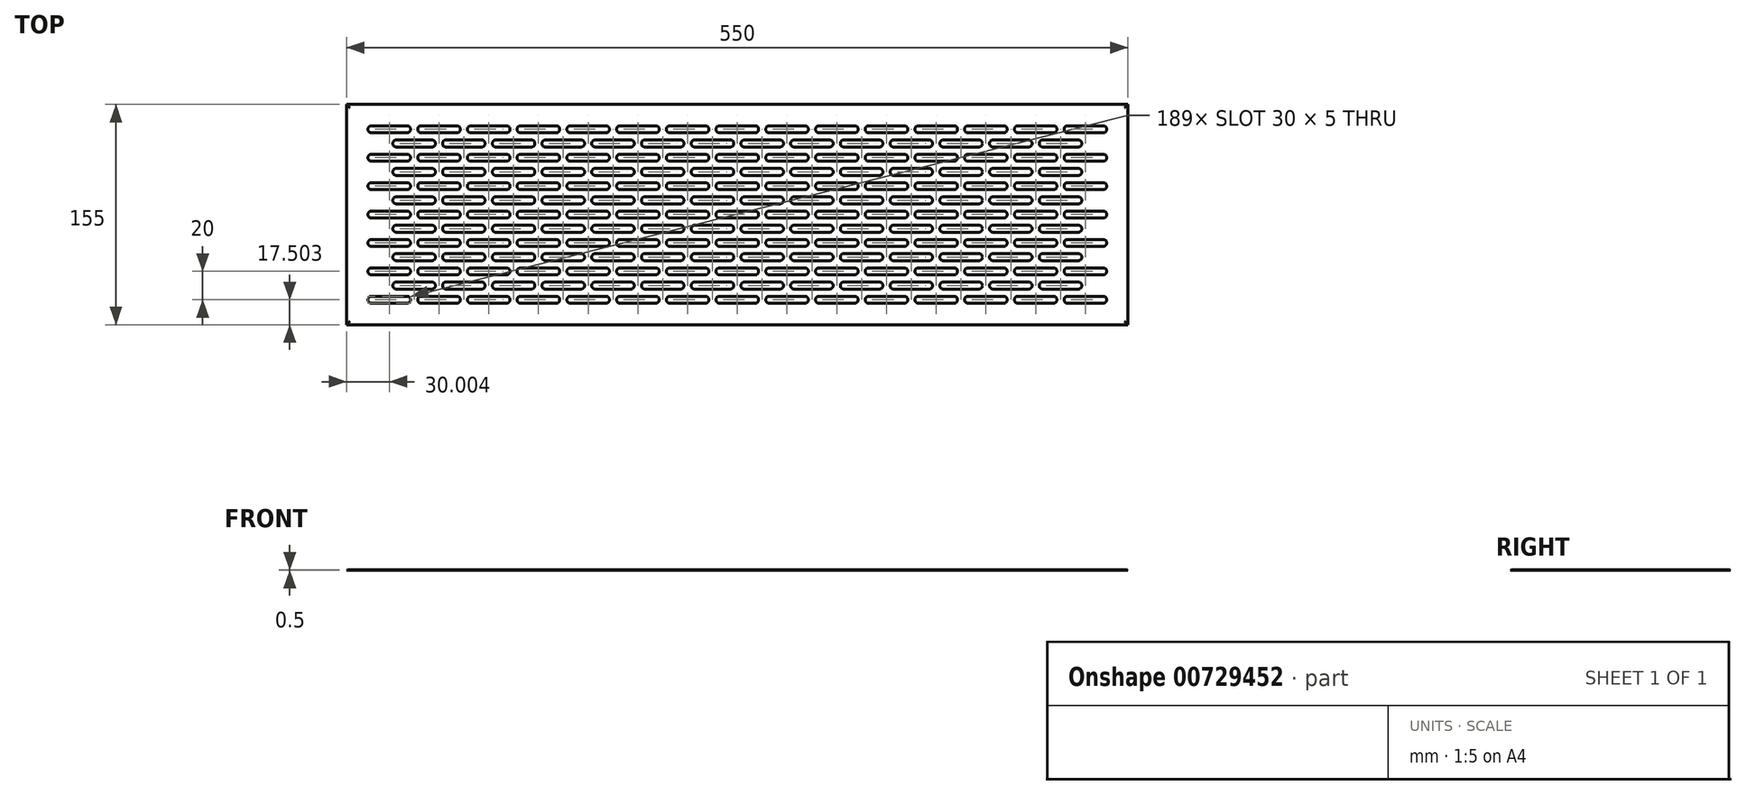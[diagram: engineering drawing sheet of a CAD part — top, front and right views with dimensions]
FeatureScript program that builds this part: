
annotation { "Feature Type Name" : "Feature", "Feature Type Description" : "" }
export const myFeature = defineFeature(function(context is Context, id is Id, definition is map)
    precondition{}
    {
        {
            var Q0;
            Q0=qCreatedBy(makeId("Top.planeOp"),FACE);
            var sketch = newSketch(context, id + "F0", { "sketchPlane" : qUnion([Q0])});
            skLineSegment(sketch, "E0.bottom", {"start": v(-229.5, 79.48) * mm, "end": v(320.5, 79.48) * mm});
            skLineSegment(sketch, "E0.top", {"start": v(-229.5, -75.52) * mm, "end": v(320.5, -75.52) * mm});
            skLineSegment(sketch, "E0.left", {"start": v(-229.5, 79.48) * mm, "end": v(-229.5, -75.52) * mm});
            skLineSegment(sketch, "E0.right", {"start": v(320.5, 79.48) * mm, "end": v(320.5, -75.52) * mm});
            skSolve(sketch);
        }
        {
            var Q0;
            Q0=makeQuery(id+"F0.imprint","IMPRINT",FACE,{"disambiguationData":[TD([[makeQuery(id+"F0.imprint","IMPRINT",EDGE,{"derivedFrom":sQuery(id+"F0.wireOp",EDGE,"E0.bottom")}),-1.0]])]});
            extrude(context, id + "F1", {"entities" : qUnion([Q0]), "depth" : 0.5 * mm, "offsetDistance" : 25 * mm});
        }
        {
            var Q0;
            Q0=makeQuery(id+"F1.opExtrude","CAP_FACE",FACE,{"disambiguationData":[OSD([sQuery(id+"F0.wireOp",EDGE,"E0.bottom"),sQuery(id+"F0.wireOp",EDGE,"E0.top"),sQuery(id+"F0.wireOp",EDGE,"E0.left"),sQuery(id+"F0.wireOp",EDGE,"E0.right")])],"isStart":false});
            var sketch = newSketch(context, id + "F2", { "sketchPlane" : qUnion([Q0])});
            skLineSegment(sketch, "E1.bottom", {"start": v(-212, -55.52) * mm, "end": v(-187, -55.52) * mm});
            skLineSegment(sketch, "E1.top", {"start": v(-212, -60.52) * mm, "end": v(-187, -60.52) * mm});
            skLineSegment(sketch, "E1.left", {"start": v(-214.5, -58.02) * mm, "end": v(-214.5, -58.02) * mm});
            skLineSegment(sketch, "E1.right", {"start": v(-184.5, -58.02) * mm, "end": v(-184.5, -58.02) * mm});
            skPoint(sketch, "E2.visualSharp", {"position": v(-214.5, -60.52) * mm});
            skArc(sketch, "E2.filletArc", {"start": v(-214.5, -58.02) * mm, "mid": v(-213.77, -59.78) * mm, "end": v(-212, -60.52) * mm});
            skPoint(sketch, "E3.visualSharp", {"position": v(-214.5, -55.52) * mm});
            skArc(sketch, "E3.filletArc", {"start": v(-212, -55.52) * mm, "mid": v(-213.77, -56.25) * mm, "end": v(-214.5, -58.02) * mm});
            skPoint(sketch, "E4.visualSharp", {"position": v(-184.5, -55.52) * mm});
            skArc(sketch, "E4.filletArc", {"start": v(-184.5, -58.02) * mm, "mid": v(-185.24, -56.25) * mm, "end": v(-187, -55.52) * mm});
            skPoint(sketch, "E5.visualSharp", {"position": v(-184.5, -60.52) * mm});
            skArc(sketch, "E5.filletArc", {"start": v(-187, -60.52) * mm, "mid": v(-185.24, -59.78) * mm, "end": v(-184.5, -58.02) * mm});
            skLineSegment(sketch, "E6.0.1.0", {"start": v(-212, -35.52) * mm, "end": v(-187, -35.52) * mm});
            skArc(sketch, "E6.0.1.1", {"start": v(-212, -35.52) * mm, "mid": v(-213.77, -36.25) * mm, "end": v(-214.5, -38.02) * mm});
            skArc(sketch, "E6.0.1.2", {"start": v(-214.5, -38.02) * mm, "mid": v(-213.77, -39.78) * mm, "end": v(-212, -40.52) * mm});
            skLineSegment(sketch, "E6.0.1.3", {"start": v(-212, -40.52) * mm, "end": v(-187, -40.52) * mm});
            skArc(sketch, "E6.0.1.4", {"start": v(-187, -40.52) * mm, "mid": v(-185.24, -39.78) * mm, "end": v(-184.5, -38.02) * mm});
            skArc(sketch, "E6.0.1.5", {"start": v(-184.5, -38.02) * mm, "mid": v(-185.24, -36.25) * mm, "end": v(-187, -35.52) * mm});
            skLineSegment(sketch, "E6.0.2.0", {"start": v(-212, -15.52) * mm, "end": v(-187, -15.52) * mm});
            skArc(sketch, "E6.0.2.1", {"start": v(-212, -15.52) * mm, "mid": v(-213.77, -16.25) * mm, "end": v(-214.5, -18.02) * mm});
            skArc(sketch, "E6.0.2.2", {"start": v(-214.5, -18.02) * mm, "mid": v(-213.77, -19.78) * mm, "end": v(-212, -20.52) * mm});
            skLineSegment(sketch, "E6.0.2.3", {"start": v(-212, -20.52) * mm, "end": v(-187, -20.52) * mm});
            skArc(sketch, "E6.0.2.4", {"start": v(-187, -20.52) * mm, "mid": v(-185.24, -19.78) * mm, "end": v(-184.5, -18.02) * mm});
            skArc(sketch, "E6.0.2.5", {"start": v(-184.5, -18.02) * mm, "mid": v(-185.24, -16.25) * mm, "end": v(-187, -15.52) * mm});
            skLineSegment(sketch, "E6.0.3.0", {"start": v(-212, 4.48) * mm, "end": v(-187, 4.48) * mm});
            skArc(sketch, "E6.0.3.1", {"start": v(-212, 4.48) * mm, "mid": v(-213.77, 3.75) * mm, "end": v(-214.5, 1.98) * mm});
            skArc(sketch, "E6.0.3.2", {"start": v(-214.5, 1.98) * mm, "mid": v(-213.77, 0.22) * mm, "end": v(-212, -0.52) * mm});
            skLineSegment(sketch, "E6.0.3.3", {"start": v(-212, -0.52) * mm, "end": v(-187, -0.52) * mm});
            skArc(sketch, "E6.0.3.4", {"start": v(-187, -0.52) * mm, "mid": v(-185.24, 0.22) * mm, "end": v(-184.5, 1.98) * mm});
            skArc(sketch, "E6.0.3.5", {"start": v(-184.5, 1.98) * mm, "mid": v(-185.24, 3.75) * mm, "end": v(-187, 4.48) * mm});
            skLineSegment(sketch, "E6.0.4.0", {"start": v(-212, 24.48) * mm, "end": v(-187, 24.48) * mm});
            skArc(sketch, "E6.0.4.1", {"start": v(-212, 24.48) * mm, "mid": v(-213.77, 23.75) * mm, "end": v(-214.5, 21.98) * mm});
            skArc(sketch, "E6.0.4.2", {"start": v(-214.5, 21.98) * mm, "mid": v(-213.77, 20.22) * mm, "end": v(-212, 19.48) * mm});
            skLineSegment(sketch, "E6.0.4.3", {"start": v(-212, 19.48) * mm, "end": v(-187, 19.48) * mm});
            skArc(sketch, "E6.0.4.4", {"start": v(-187, 19.48) * mm, "mid": v(-185.24, 20.22) * mm, "end": v(-184.5, 21.98) * mm});
            skArc(sketch, "E6.0.4.5", {"start": v(-184.5, 21.98) * mm, "mid": v(-185.24, 23.75) * mm, "end": v(-187, 24.48) * mm});
            skLineSegment(sketch, "E6.0.5.0", {"start": v(-212, 44.48) * mm, "end": v(-187, 44.48) * mm});
            skArc(sketch, "E6.0.5.1", {"start": v(-212, 44.48) * mm, "mid": v(-213.77, 43.75) * mm, "end": v(-214.5, 41.98) * mm});
            skArc(sketch, "E6.0.5.2", {"start": v(-214.5, 41.98) * mm, "mid": v(-213.77, 40.22) * mm, "end": v(-212, 39.48) * mm});
            skLineSegment(sketch, "E6.0.5.3", {"start": v(-212, 39.48) * mm, "end": v(-187, 39.48) * mm});
            skArc(sketch, "E6.0.5.4", {"start": v(-187, 39.48) * mm, "mid": v(-185.24, 40.22) * mm, "end": v(-184.5, 41.98) * mm});
            skArc(sketch, "E6.0.5.5", {"start": v(-184.5, 41.98) * mm, "mid": v(-185.24, 43.75) * mm, "end": v(-187, 44.48) * mm});
            skLineSegment(sketch, "E6.0.6.0", {"start": v(-212, 64.48) * mm, "end": v(-187, 64.48) * mm});
            skArc(sketch, "E6.0.6.1", {"start": v(-212, 64.48) * mm, "mid": v(-213.77, 63.75) * mm, "end": v(-214.5, 61.98) * mm});
            skArc(sketch, "E6.0.6.2", {"start": v(-214.5, 61.98) * mm, "mid": v(-213.77, 60.22) * mm, "end": v(-212, 59.48) * mm});
            skLineSegment(sketch, "E6.0.6.3", {"start": v(-212, 59.48) * mm, "end": v(-187, 59.48) * mm});
            skArc(sketch, "E6.0.6.4", {"start": v(-187, 59.48) * mm, "mid": v(-185.24, 60.22) * mm, "end": v(-184.5, 61.98) * mm});
            skArc(sketch, "E6.0.6.5", {"start": v(-184.5, 61.98) * mm, "mid": v(-185.24, 63.75) * mm, "end": v(-187, 64.48) * mm});
            skLineSegment(sketch, "E6.1.0.0", {"start": v(-177, -55.52) * mm, "end": v(-152, -55.52) * mm});
            skArc(sketch, "E6.1.0.1", {"start": v(-177, -55.52) * mm, "mid": v(-178.77, -56.25) * mm, "end": v(-179.5, -58.02) * mm});
            skArc(sketch, "E6.1.0.2", {"start": v(-179.5, -58.02) * mm, "mid": v(-178.77, -59.78) * mm, "end": v(-177, -60.52) * mm});
            skLineSegment(sketch, "E6.1.0.3", {"start": v(-177, -60.52) * mm, "end": v(-152, -60.52) * mm});
            skArc(sketch, "E6.1.0.4", {"start": v(-152, -60.52) * mm, "mid": v(-150.24, -59.78) * mm, "end": v(-149.5, -58.02) * mm});
            skArc(sketch, "E6.1.0.5", {"start": v(-149.5, -58.02) * mm, "mid": v(-150.24, -56.25) * mm, "end": v(-152, -55.52) * mm});
            skLineSegment(sketch, "E6.1.1.0", {"start": v(-177, -35.52) * mm, "end": v(-152, -35.52) * mm});
            skArc(sketch, "E6.1.1.1", {"start": v(-177, -35.52) * mm, "mid": v(-178.77, -36.25) * mm, "end": v(-179.5, -38.02) * mm});
            skArc(sketch, "E6.1.1.2", {"start": v(-179.5, -38.02) * mm, "mid": v(-178.77, -39.78) * mm, "end": v(-177, -40.52) * mm});
            skLineSegment(sketch, "E6.1.1.3", {"start": v(-177, -40.52) * mm, "end": v(-152, -40.52) * mm});
            skArc(sketch, "E6.1.1.4", {"start": v(-152, -40.52) * mm, "mid": v(-150.24, -39.78) * mm, "end": v(-149.5, -38.02) * mm});
            skArc(sketch, "E6.1.1.5", {"start": v(-149.5, -38.02) * mm, "mid": v(-150.24, -36.25) * mm, "end": v(-152, -35.52) * mm});
            skLineSegment(sketch, "E6.1.2.0", {"start": v(-177, -15.52) * mm, "end": v(-152, -15.52) * mm});
            skArc(sketch, "E6.1.2.1", {"start": v(-177, -15.52) * mm, "mid": v(-178.77, -16.25) * mm, "end": v(-179.5, -18.02) * mm});
            skArc(sketch, "E6.1.2.2", {"start": v(-179.5, -18.02) * mm, "mid": v(-178.77, -19.78) * mm, "end": v(-177, -20.52) * mm});
            skLineSegment(sketch, "E6.1.2.3", {"start": v(-177, -20.52) * mm, "end": v(-152, -20.52) * mm});
            skArc(sketch, "E6.1.2.4", {"start": v(-152, -20.52) * mm, "mid": v(-150.24, -19.78) * mm, "end": v(-149.5, -18.02) * mm});
            skArc(sketch, "E6.1.2.5", {"start": v(-149.5, -18.02) * mm, "mid": v(-150.24, -16.25) * mm, "end": v(-152, -15.52) * mm});
            skLineSegment(sketch, "E6.1.3.0", {"start": v(-177, 4.48) * mm, "end": v(-152, 4.48) * mm});
            skArc(sketch, "E6.1.3.1", {"start": v(-177, 4.48) * mm, "mid": v(-178.77, 3.75) * mm, "end": v(-179.5, 1.98) * mm});
            skArc(sketch, "E6.1.3.2", {"start": v(-179.5, 1.98) * mm, "mid": v(-178.77, 0.22) * mm, "end": v(-177, -0.52) * mm});
            skLineSegment(sketch, "E6.1.3.3", {"start": v(-177, -0.52) * mm, "end": v(-152, -0.52) * mm});
            skArc(sketch, "E6.1.3.4", {"start": v(-152, -0.52) * mm, "mid": v(-150.24, 0.22) * mm, "end": v(-149.5, 1.98) * mm});
            skArc(sketch, "E6.1.3.5", {"start": v(-149.5, 1.98) * mm, "mid": v(-150.24, 3.75) * mm, "end": v(-152, 4.48) * mm});
            skLineSegment(sketch, "E6.1.4.0", {"start": v(-177, 24.48) * mm, "end": v(-152, 24.48) * mm});
            skArc(sketch, "E6.1.4.1", {"start": v(-177, 24.48) * mm, "mid": v(-178.77, 23.75) * mm, "end": v(-179.5, 21.98) * mm});
            skArc(sketch, "E6.1.4.2", {"start": v(-179.5, 21.98) * mm, "mid": v(-178.77, 20.22) * mm, "end": v(-177, 19.48) * mm});
            skLineSegment(sketch, "E6.1.4.3", {"start": v(-177, 19.48) * mm, "end": v(-152, 19.48) * mm});
            skArc(sketch, "E6.1.4.4", {"start": v(-152, 19.48) * mm, "mid": v(-150.24, 20.22) * mm, "end": v(-149.5, 21.98) * mm});
            skArc(sketch, "E6.1.4.5", {"start": v(-149.5, 21.98) * mm, "mid": v(-150.24, 23.75) * mm, "end": v(-152, 24.48) * mm});
            skLineSegment(sketch, "E6.1.5.0", {"start": v(-177, 44.48) * mm, "end": v(-152, 44.48) * mm});
            skArc(sketch, "E6.1.5.1", {"start": v(-177, 44.48) * mm, "mid": v(-178.77, 43.75) * mm, "end": v(-179.5, 41.98) * mm});
            skArc(sketch, "E6.1.5.2", {"start": v(-179.5, 41.98) * mm, "mid": v(-178.77, 40.22) * mm, "end": v(-177, 39.48) * mm});
            skLineSegment(sketch, "E6.1.5.3", {"start": v(-177, 39.48) * mm, "end": v(-152, 39.48) * mm});
            skArc(sketch, "E6.1.5.4", {"start": v(-152, 39.48) * mm, "mid": v(-150.24, 40.22) * mm, "end": v(-149.5, 41.98) * mm});
            skArc(sketch, "E6.1.5.5", {"start": v(-149.5, 41.98) * mm, "mid": v(-150.24, 43.75) * mm, "end": v(-152, 44.48) * mm});
            skLineSegment(sketch, "E6.1.6.0", {"start": v(-177, 64.48) * mm, "end": v(-152, 64.48) * mm});
            skArc(sketch, "E6.1.6.1", {"start": v(-177, 64.48) * mm, "mid": v(-178.77, 63.75) * mm, "end": v(-179.5, 61.98) * mm});
            skArc(sketch, "E6.1.6.2", {"start": v(-179.5, 61.98) * mm, "mid": v(-178.77, 60.22) * mm, "end": v(-177, 59.48) * mm});
            skLineSegment(sketch, "E6.1.6.3", {"start": v(-177, 59.48) * mm, "end": v(-152, 59.48) * mm});
            skArc(sketch, "E6.1.6.4", {"start": v(-152, 59.48) * mm, "mid": v(-150.24, 60.22) * mm, "end": v(-149.5, 61.98) * mm});
            skArc(sketch, "E6.1.6.5", {"start": v(-149.5, 61.98) * mm, "mid": v(-150.24, 63.75) * mm, "end": v(-152, 64.48) * mm});
            skLineSegment(sketch, "E6.2.0.0", {"start": v(-142, -55.52) * mm, "end": v(-117, -55.52) * mm});
            skArc(sketch, "E6.2.0.1", {"start": v(-142, -55.52) * mm, "mid": v(-143.77, -56.25) * mm, "end": v(-144.5, -58.02) * mm});
            skArc(sketch, "E6.2.0.2", {"start": v(-144.5, -58.02) * mm, "mid": v(-143.77, -59.78) * mm, "end": v(-142, -60.52) * mm});
            skLineSegment(sketch, "E6.2.0.3", {"start": v(-142, -60.52) * mm, "end": v(-117, -60.52) * mm});
            skArc(sketch, "E6.2.0.4", {"start": v(-117, -60.52) * mm, "mid": v(-115.24, -59.78) * mm, "end": v(-114.5, -58.02) * mm});
            skArc(sketch, "E6.2.0.5", {"start": v(-114.5, -58.02) * mm, "mid": v(-115.24, -56.25) * mm, "end": v(-117, -55.52) * mm});
            skLineSegment(sketch, "E6.2.1.0", {"start": v(-142, -35.52) * mm, "end": v(-117, -35.52) * mm});
            skArc(sketch, "E6.2.1.1", {"start": v(-142, -35.52) * mm, "mid": v(-143.77, -36.25) * mm, "end": v(-144.5, -38.02) * mm});
            skArc(sketch, "E6.2.1.2", {"start": v(-144.5, -38.02) * mm, "mid": v(-143.77, -39.78) * mm, "end": v(-142, -40.52) * mm});
            skLineSegment(sketch, "E6.2.1.3", {"start": v(-142, -40.52) * mm, "end": v(-117, -40.52) * mm});
            skArc(sketch, "E6.2.1.4", {"start": v(-117, -40.52) * mm, "mid": v(-115.24, -39.78) * mm, "end": v(-114.5, -38.02) * mm});
            skArc(sketch, "E6.2.1.5", {"start": v(-114.5, -38.02) * mm, "mid": v(-115.24, -36.25) * mm, "end": v(-117, -35.52) * mm});
            skLineSegment(sketch, "E6.2.2.0", {"start": v(-142, -15.52) * mm, "end": v(-117, -15.52) * mm});
            skArc(sketch, "E6.2.2.1", {"start": v(-142, -15.52) * mm, "mid": v(-143.77, -16.25) * mm, "end": v(-144.5, -18.02) * mm});
            skArc(sketch, "E6.2.2.2", {"start": v(-144.5, -18.02) * mm, "mid": v(-143.77, -19.78) * mm, "end": v(-142, -20.52) * mm});
            skLineSegment(sketch, "E6.2.2.3", {"start": v(-142, -20.52) * mm, "end": v(-117, -20.52) * mm});
            skArc(sketch, "E6.2.2.4", {"start": v(-117, -20.52) * mm, "mid": v(-115.24, -19.78) * mm, "end": v(-114.5, -18.02) * mm});
            skArc(sketch, "E6.2.2.5", {"start": v(-114.5, -18.02) * mm, "mid": v(-115.24, -16.25) * mm, "end": v(-117, -15.52) * mm});
            skLineSegment(sketch, "E6.2.3.0", {"start": v(-142, 4.48) * mm, "end": v(-117, 4.48) * mm});
            skArc(sketch, "E6.2.3.1", {"start": v(-142, 4.48) * mm, "mid": v(-143.77, 3.75) * mm, "end": v(-144.5, 1.98) * mm});
            skArc(sketch, "E6.2.3.2", {"start": v(-144.5, 1.98) * mm, "mid": v(-143.77, 0.22) * mm, "end": v(-142, -0.52) * mm});
            skLineSegment(sketch, "E6.2.3.3", {"start": v(-142, -0.52) * mm, "end": v(-117, -0.52) * mm});
            skArc(sketch, "E6.2.3.4", {"start": v(-117, -0.52) * mm, "mid": v(-115.24, 0.22) * mm, "end": v(-114.5, 1.98) * mm});
            skArc(sketch, "E6.2.3.5", {"start": v(-114.5, 1.98) * mm, "mid": v(-115.24, 3.75) * mm, "end": v(-117, 4.48) * mm});
            skLineSegment(sketch, "E6.2.4.0", {"start": v(-142, 24.48) * mm, "end": v(-117, 24.48) * mm});
            skArc(sketch, "E6.2.4.1", {"start": v(-142, 24.48) * mm, "mid": v(-143.77, 23.75) * mm, "end": v(-144.5, 21.98) * mm});
            skArc(sketch, "E6.2.4.2", {"start": v(-144.5, 21.98) * mm, "mid": v(-143.77, 20.22) * mm, "end": v(-142, 19.48) * mm});
            skLineSegment(sketch, "E6.2.4.3", {"start": v(-142, 19.48) * mm, "end": v(-117, 19.48) * mm});
            skArc(sketch, "E6.2.4.4", {"start": v(-117, 19.48) * mm, "mid": v(-115.24, 20.22) * mm, "end": v(-114.5, 21.98) * mm});
            skArc(sketch, "E6.2.4.5", {"start": v(-114.5, 21.98) * mm, "mid": v(-115.24, 23.75) * mm, "end": v(-117, 24.48) * mm});
            skLineSegment(sketch, "E6.2.5.0", {"start": v(-142, 44.48) * mm, "end": v(-117, 44.48) * mm});
            skArc(sketch, "E6.2.5.1", {"start": v(-142, 44.48) * mm, "mid": v(-143.77, 43.75) * mm, "end": v(-144.5, 41.98) * mm});
            skArc(sketch, "E6.2.5.2", {"start": v(-144.5, 41.98) * mm, "mid": v(-143.77, 40.22) * mm, "end": v(-142, 39.48) * mm});
            skLineSegment(sketch, "E6.2.5.3", {"start": v(-142, 39.48) * mm, "end": v(-117, 39.48) * mm});
            skArc(sketch, "E6.2.5.4", {"start": v(-117, 39.48) * mm, "mid": v(-115.24, 40.22) * mm, "end": v(-114.5, 41.98) * mm});
            skArc(sketch, "E6.2.5.5", {"start": v(-114.5, 41.98) * mm, "mid": v(-115.24, 43.75) * mm, "end": v(-117, 44.48) * mm});
            skLineSegment(sketch, "E6.2.6.0", {"start": v(-142, 64.48) * mm, "end": v(-117, 64.48) * mm});
            skArc(sketch, "E6.2.6.1", {"start": v(-142, 64.48) * mm, "mid": v(-143.77, 63.75) * mm, "end": v(-144.5, 61.98) * mm});
            skArc(sketch, "E6.2.6.2", {"start": v(-144.5, 61.98) * mm, "mid": v(-143.77, 60.22) * mm, "end": v(-142, 59.48) * mm});
            skLineSegment(sketch, "E6.2.6.3", {"start": v(-142, 59.48) * mm, "end": v(-117, 59.48) * mm});
            skArc(sketch, "E6.2.6.4", {"start": v(-117, 59.48) * mm, "mid": v(-115.24, 60.22) * mm, "end": v(-114.5, 61.98) * mm});
            skArc(sketch, "E6.2.6.5", {"start": v(-114.5, 61.98) * mm, "mid": v(-115.24, 63.75) * mm, "end": v(-117, 64.48) * mm});
            skLineSegment(sketch, "E6.3.0.0", {"start": v(-107, -55.52) * mm, "end": v(-82, -55.52) * mm});
            skArc(sketch, "E6.3.0.1", {"start": v(-107, -55.52) * mm, "mid": v(-108.77, -56.25) * mm, "end": v(-109.5, -58.02) * mm});
            skArc(sketch, "E6.3.0.2", {"start": v(-109.5, -58.02) * mm, "mid": v(-108.77, -59.78) * mm, "end": v(-107, -60.52) * mm});
            skLineSegment(sketch, "E6.3.0.3", {"start": v(-107, -60.52) * mm, "end": v(-82, -60.52) * mm});
            skArc(sketch, "E6.3.0.4", {"start": v(-82, -60.52) * mm, "mid": v(-80.24, -59.78) * mm, "end": v(-79.5, -58.02) * mm});
            skArc(sketch, "E6.3.0.5", {"start": v(-79.5, -58.02) * mm, "mid": v(-80.24, -56.25) * mm, "end": v(-82, -55.52) * mm});
            skLineSegment(sketch, "E6.3.1.0", {"start": v(-107, -35.52) * mm, "end": v(-82, -35.52) * mm});
            skArc(sketch, "E6.3.1.1", {"start": v(-107, -35.52) * mm, "mid": v(-108.77, -36.25) * mm, "end": v(-109.5, -38.02) * mm});
            skArc(sketch, "E6.3.1.2", {"start": v(-109.5, -38.02) * mm, "mid": v(-108.77, -39.78) * mm, "end": v(-107, -40.52) * mm});
            skLineSegment(sketch, "E6.3.1.3", {"start": v(-107, -40.52) * mm, "end": v(-82, -40.52) * mm});
            skArc(sketch, "E6.3.1.4", {"start": v(-82, -40.52) * mm, "mid": v(-80.24, -39.78) * mm, "end": v(-79.5, -38.02) * mm});
            skArc(sketch, "E6.3.1.5", {"start": v(-79.5, -38.02) * mm, "mid": v(-80.24, -36.25) * mm, "end": v(-82, -35.52) * mm});
            skLineSegment(sketch, "E6.3.2.0", {"start": v(-107, -15.52) * mm, "end": v(-82, -15.52) * mm});
            skArc(sketch, "E6.3.2.1", {"start": v(-107, -15.52) * mm, "mid": v(-108.77, -16.25) * mm, "end": v(-109.5, -18.02) * mm});
            skArc(sketch, "E6.3.2.2", {"start": v(-109.5, -18.02) * mm, "mid": v(-108.77, -19.78) * mm, "end": v(-107, -20.52) * mm});
            skLineSegment(sketch, "E6.3.2.3", {"start": v(-107, -20.52) * mm, "end": v(-82, -20.52) * mm});
            skArc(sketch, "E6.3.2.4", {"start": v(-82, -20.52) * mm, "mid": v(-80.24, -19.78) * mm, "end": v(-79.5, -18.02) * mm});
            skArc(sketch, "E6.3.2.5", {"start": v(-79.5, -18.02) * mm, "mid": v(-80.24, -16.25) * mm, "end": v(-82, -15.52) * mm});
            skLineSegment(sketch, "E6.3.3.0", {"start": v(-107, 4.48) * mm, "end": v(-82, 4.48) * mm});
            skArc(sketch, "E6.3.3.1", {"start": v(-107, 4.48) * mm, "mid": v(-108.77, 3.75) * mm, "end": v(-109.5, 1.98) * mm});
            skArc(sketch, "E6.3.3.2", {"start": v(-109.5, 1.98) * mm, "mid": v(-108.77, 0.22) * mm, "end": v(-107, -0.52) * mm});
            skLineSegment(sketch, "E6.3.3.3", {"start": v(-107, -0.52) * mm, "end": v(-82, -0.52) * mm});
            skArc(sketch, "E6.3.3.4", {"start": v(-82, -0.52) * mm, "mid": v(-80.24, 0.22) * mm, "end": v(-79.5, 1.98) * mm});
            skArc(sketch, "E6.3.3.5", {"start": v(-79.5, 1.98) * mm, "mid": v(-80.24, 3.75) * mm, "end": v(-82, 4.48) * mm});
            skLineSegment(sketch, "E6.3.4.0", {"start": v(-107, 24.48) * mm, "end": v(-82, 24.48) * mm});
            skArc(sketch, "E6.3.4.1", {"start": v(-107, 24.48) * mm, "mid": v(-108.77, 23.75) * mm, "end": v(-109.5, 21.98) * mm});
            skArc(sketch, "E6.3.4.2", {"start": v(-109.5, 21.98) * mm, "mid": v(-108.77, 20.22) * mm, "end": v(-107, 19.48) * mm});
            skLineSegment(sketch, "E6.3.4.3", {"start": v(-107, 19.48) * mm, "end": v(-82, 19.48) * mm});
            skArc(sketch, "E6.3.4.4", {"start": v(-82, 19.48) * mm, "mid": v(-80.24, 20.22) * mm, "end": v(-79.5, 21.98) * mm});
            skArc(sketch, "E6.3.4.5", {"start": v(-79.5, 21.98) * mm, "mid": v(-80.24, 23.75) * mm, "end": v(-82, 24.48) * mm});
            skLineSegment(sketch, "E6.3.5.0", {"start": v(-107, 44.48) * mm, "end": v(-82, 44.48) * mm});
            skArc(sketch, "E6.3.5.1", {"start": v(-107, 44.48) * mm, "mid": v(-108.77, 43.75) * mm, "end": v(-109.5, 41.98) * mm});
            skArc(sketch, "E6.3.5.2", {"start": v(-109.5, 41.98) * mm, "mid": v(-108.77, 40.22) * mm, "end": v(-107, 39.48) * mm});
            skLineSegment(sketch, "E6.3.5.3", {"start": v(-107, 39.48) * mm, "end": v(-82, 39.48) * mm});
            skArc(sketch, "E6.3.5.4", {"start": v(-82, 39.48) * mm, "mid": v(-80.24, 40.22) * mm, "end": v(-79.5, 41.98) * mm});
            skArc(sketch, "E6.3.5.5", {"start": v(-79.5, 41.98) * mm, "mid": v(-80.24, 43.75) * mm, "end": v(-82, 44.48) * mm});
            skLineSegment(sketch, "E6.3.6.0", {"start": v(-107, 64.48) * mm, "end": v(-82, 64.48) * mm});
            skArc(sketch, "E6.3.6.1", {"start": v(-107, 64.48) * mm, "mid": v(-108.77, 63.75) * mm, "end": v(-109.5, 61.98) * mm});
            skArc(sketch, "E6.3.6.2", {"start": v(-109.5, 61.98) * mm, "mid": v(-108.77, 60.22) * mm, "end": v(-107, 59.48) * mm});
            skLineSegment(sketch, "E6.3.6.3", {"start": v(-107, 59.48) * mm, "end": v(-82, 59.48) * mm});
            skArc(sketch, "E6.3.6.4", {"start": v(-82, 59.48) * mm, "mid": v(-80.24, 60.22) * mm, "end": v(-79.5, 61.98) * mm});
            skArc(sketch, "E6.3.6.5", {"start": v(-79.5, 61.98) * mm, "mid": v(-80.24, 63.75) * mm, "end": v(-82, 64.48) * mm});
            skLineSegment(sketch, "E6.4.0.0", {"start": v(-72, -55.52) * mm, "end": v(-47, -55.52) * mm});
            skArc(sketch, "E6.4.0.1", {"start": v(-72, -55.52) * mm, "mid": v(-73.77, -56.25) * mm, "end": v(-74.5, -58.02) * mm});
            skArc(sketch, "E6.4.0.2", {"start": v(-74.5, -58.02) * mm, "mid": v(-73.77, -59.78) * mm, "end": v(-72, -60.52) * mm});
            skLineSegment(sketch, "E6.4.0.3", {"start": v(-72, -60.52) * mm, "end": v(-47, -60.52) * mm});
            skArc(sketch, "E6.4.0.4", {"start": v(-47, -60.52) * mm, "mid": v(-45.24, -59.78) * mm, "end": v(-44.5, -58.02) * mm});
            skArc(sketch, "E6.4.0.5", {"start": v(-44.5, -58.02) * mm, "mid": v(-45.24, -56.25) * mm, "end": v(-47, -55.52) * mm});
            skLineSegment(sketch, "E6.4.1.0", {"start": v(-72, -35.52) * mm, "end": v(-47, -35.52) * mm});
            skArc(sketch, "E6.4.1.1", {"start": v(-72, -35.52) * mm, "mid": v(-73.77, -36.25) * mm, "end": v(-74.5, -38.02) * mm});
            skArc(sketch, "E6.4.1.2", {"start": v(-74.5, -38.02) * mm, "mid": v(-73.77, -39.78) * mm, "end": v(-72, -40.52) * mm});
            skLineSegment(sketch, "E6.4.1.3", {"start": v(-72, -40.52) * mm, "end": v(-47, -40.52) * mm});
            skArc(sketch, "E6.4.1.4", {"start": v(-47, -40.52) * mm, "mid": v(-45.24, -39.78) * mm, "end": v(-44.5, -38.02) * mm});
            skArc(sketch, "E6.4.1.5", {"start": v(-44.5, -38.02) * mm, "mid": v(-45.24, -36.25) * mm, "end": v(-47, -35.52) * mm});
            skLineSegment(sketch, "E6.4.2.0", {"start": v(-72, -15.52) * mm, "end": v(-47, -15.52) * mm});
            skArc(sketch, "E6.4.2.1", {"start": v(-72, -15.52) * mm, "mid": v(-73.77, -16.25) * mm, "end": v(-74.5, -18.02) * mm});
            skArc(sketch, "E6.4.2.2", {"start": v(-74.5, -18.02) * mm, "mid": v(-73.77, -19.78) * mm, "end": v(-72, -20.52) * mm});
            skLineSegment(sketch, "E6.4.2.3", {"start": v(-72, -20.52) * mm, "end": v(-47, -20.52) * mm});
            skArc(sketch, "E6.4.2.4", {"start": v(-47, -20.52) * mm, "mid": v(-45.24, -19.78) * mm, "end": v(-44.5, -18.02) * mm});
            skArc(sketch, "E6.4.2.5", {"start": v(-44.5, -18.02) * mm, "mid": v(-45.24, -16.25) * mm, "end": v(-47, -15.52) * mm});
            skLineSegment(sketch, "E6.4.3.0", {"start": v(-72, 4.48) * mm, "end": v(-47, 4.48) * mm});
            skArc(sketch, "E6.4.3.1", {"start": v(-72, 4.48) * mm, "mid": v(-73.77, 3.75) * mm, "end": v(-74.5, 1.98) * mm});
            skArc(sketch, "E6.4.3.2", {"start": v(-74.5, 1.98) * mm, "mid": v(-73.77, 0.22) * mm, "end": v(-72, -0.52) * mm});
            skLineSegment(sketch, "E6.4.3.3", {"start": v(-72, -0.52) * mm, "end": v(-47, -0.52) * mm});
            skArc(sketch, "E6.4.3.4", {"start": v(-47, -0.52) * mm, "mid": v(-45.24, 0.22) * mm, "end": v(-44.5, 1.98) * mm});
            skArc(sketch, "E6.4.3.5", {"start": v(-44.5, 1.98) * mm, "mid": v(-45.24, 3.75) * mm, "end": v(-47, 4.48) * mm});
            skLineSegment(sketch, "E6.4.4.0", {"start": v(-72, 24.48) * mm, "end": v(-47, 24.48) * mm});
            skArc(sketch, "E6.4.4.1", {"start": v(-72, 24.48) * mm, "mid": v(-73.77, 23.75) * mm, "end": v(-74.5, 21.98) * mm});
            skArc(sketch, "E6.4.4.2", {"start": v(-74.5, 21.98) * mm, "mid": v(-73.77, 20.22) * mm, "end": v(-72, 19.48) * mm});
            skLineSegment(sketch, "E6.4.4.3", {"start": v(-72, 19.48) * mm, "end": v(-47, 19.48) * mm});
            skArc(sketch, "E6.4.4.4", {"start": v(-47, 19.48) * mm, "mid": v(-45.24, 20.22) * mm, "end": v(-44.5, 21.98) * mm});
            skArc(sketch, "E6.4.4.5", {"start": v(-44.5, 21.98) * mm, "mid": v(-45.24, 23.75) * mm, "end": v(-47, 24.48) * mm});
            skLineSegment(sketch, "E6.4.5.0", {"start": v(-72, 44.48) * mm, "end": v(-47, 44.48) * mm});
            skArc(sketch, "E6.4.5.1", {"start": v(-72, 44.48) * mm, "mid": v(-73.77, 43.75) * mm, "end": v(-74.5, 41.98) * mm});
            skArc(sketch, "E6.4.5.2", {"start": v(-74.5, 41.98) * mm, "mid": v(-73.77, 40.22) * mm, "end": v(-72, 39.48) * mm});
            skLineSegment(sketch, "E6.4.5.3", {"start": v(-72, 39.48) * mm, "end": v(-47, 39.48) * mm});
            skArc(sketch, "E6.4.5.4", {"start": v(-47, 39.48) * mm, "mid": v(-45.24, 40.22) * mm, "end": v(-44.5, 41.98) * mm});
            skArc(sketch, "E6.4.5.5", {"start": v(-44.5, 41.98) * mm, "mid": v(-45.24, 43.75) * mm, "end": v(-47, 44.48) * mm});
            skLineSegment(sketch, "E6.4.6.0", {"start": v(-72, 64.48) * mm, "end": v(-47, 64.48) * mm});
            skArc(sketch, "E6.4.6.1", {"start": v(-72, 64.48) * mm, "mid": v(-73.77, 63.75) * mm, "end": v(-74.5, 61.98) * mm});
            skArc(sketch, "E6.4.6.2", {"start": v(-74.5, 61.98) * mm, "mid": v(-73.77, 60.22) * mm, "end": v(-72, 59.48) * mm});
            skLineSegment(sketch, "E6.4.6.3", {"start": v(-72, 59.48) * mm, "end": v(-47, 59.48) * mm});
            skArc(sketch, "E6.4.6.4", {"start": v(-47, 59.48) * mm, "mid": v(-45.24, 60.22) * mm, "end": v(-44.5, 61.98) * mm});
            skArc(sketch, "E6.4.6.5", {"start": v(-44.5, 61.98) * mm, "mid": v(-45.24, 63.75) * mm, "end": v(-47, 64.48) * mm});
            skLineSegment(sketch, "E6.5.0.0", {"start": v(-37, -55.52) * mm, "end": v(-12, -55.52) * mm});
            skArc(sketch, "E6.5.0.1", {"start": v(-37, -55.52) * mm, "mid": v(-38.77, -56.25) * mm, "end": v(-39.5, -58.02) * mm});
            skArc(sketch, "E6.5.0.2", {"start": v(-39.5, -58.02) * mm, "mid": v(-38.77, -59.78) * mm, "end": v(-37, -60.52) * mm});
            skLineSegment(sketch, "E6.5.0.3", {"start": v(-37, -60.52) * mm, "end": v(-12, -60.52) * mm});
            skArc(sketch, "E6.5.0.4", {"start": v(-12, -60.52) * mm, "mid": v(-10.24, -59.78) * mm, "end": v(-9.5, -58.02) * mm});
            skArc(sketch, "E6.5.0.5", {"start": v(-9.5, -58.02) * mm, "mid": v(-10.24, -56.25) * mm, "end": v(-12, -55.52) * mm});
            skLineSegment(sketch, "E6.5.1.0", {"start": v(-37, -35.52) * mm, "end": v(-12, -35.52) * mm});
            skArc(sketch, "E6.5.1.1", {"start": v(-37, -35.52) * mm, "mid": v(-38.77, -36.25) * mm, "end": v(-39.5, -38.02) * mm});
            skArc(sketch, "E6.5.1.2", {"start": v(-39.5, -38.02) * mm, "mid": v(-38.77, -39.78) * mm, "end": v(-37, -40.52) * mm});
            skLineSegment(sketch, "E6.5.1.3", {"start": v(-37, -40.52) * mm, "end": v(-12, -40.52) * mm});
            skArc(sketch, "E6.5.1.4", {"start": v(-12, -40.52) * mm, "mid": v(-10.24, -39.78) * mm, "end": v(-9.5, -38.02) * mm});
            skArc(sketch, "E6.5.1.5", {"start": v(-9.5, -38.02) * mm, "mid": v(-10.24, -36.25) * mm, "end": v(-12, -35.52) * mm});
            skLineSegment(sketch, "E6.5.2.0", {"start": v(-37, -15.52) * mm, "end": v(-12, -15.52) * mm});
            skArc(sketch, "E6.5.2.1", {"start": v(-37, -15.52) * mm, "mid": v(-38.77, -16.25) * mm, "end": v(-39.5, -18.02) * mm});
            skArc(sketch, "E6.5.2.2", {"start": v(-39.5, -18.02) * mm, "mid": v(-38.77, -19.78) * mm, "end": v(-37, -20.52) * mm});
            skLineSegment(sketch, "E6.5.2.3", {"start": v(-37, -20.52) * mm, "end": v(-12, -20.52) * mm});
            skArc(sketch, "E6.5.2.4", {"start": v(-12, -20.52) * mm, "mid": v(-10.24, -19.78) * mm, "end": v(-9.5, -18.02) * mm});
            skArc(sketch, "E6.5.2.5", {"start": v(-9.5, -18.02) * mm, "mid": v(-10.24, -16.25) * mm, "end": v(-12, -15.52) * mm});
            skLineSegment(sketch, "E6.5.3.0", {"start": v(-37, 4.48) * mm, "end": v(-12, 4.48) * mm});
            skArc(sketch, "E6.5.3.1", {"start": v(-37, 4.48) * mm, "mid": v(-38.77, 3.75) * mm, "end": v(-39.5, 1.98) * mm});
            skArc(sketch, "E6.5.3.2", {"start": v(-39.5, 1.98) * mm, "mid": v(-38.77, 0.22) * mm, "end": v(-37, -0.52) * mm});
            skLineSegment(sketch, "E6.5.3.3", {"start": v(-37, -0.52) * mm, "end": v(-12, -0.52) * mm});
            skArc(sketch, "E6.5.3.4", {"start": v(-12, -0.52) * mm, "mid": v(-10.24, 0.22) * mm, "end": v(-9.5, 1.98) * mm});
            skArc(sketch, "E6.5.3.5", {"start": v(-9.5, 1.98) * mm, "mid": v(-10.24, 3.75) * mm, "end": v(-12, 4.48) * mm});
            skLineSegment(sketch, "E6.5.4.0", {"start": v(-37, 24.48) * mm, "end": v(-12, 24.48) * mm});
            skArc(sketch, "E6.5.4.1", {"start": v(-37, 24.48) * mm, "mid": v(-38.77, 23.75) * mm, "end": v(-39.5, 21.98) * mm});
            skArc(sketch, "E6.5.4.2", {"start": v(-39.5, 21.98) * mm, "mid": v(-38.77, 20.22) * mm, "end": v(-37, 19.48) * mm});
            skLineSegment(sketch, "E6.5.4.3", {"start": v(-37, 19.48) * mm, "end": v(-12, 19.48) * mm});
            skArc(sketch, "E6.5.4.4", {"start": v(-12, 19.48) * mm, "mid": v(-10.24, 20.22) * mm, "end": v(-9.5, 21.98) * mm});
            skArc(sketch, "E6.5.4.5", {"start": v(-9.5, 21.98) * mm, "mid": v(-10.24, 23.75) * mm, "end": v(-12, 24.48) * mm});
            skLineSegment(sketch, "E6.5.5.0", {"start": v(-37, 44.48) * mm, "end": v(-12, 44.48) * mm});
            skArc(sketch, "E6.5.5.1", {"start": v(-37, 44.48) * mm, "mid": v(-38.77, 43.75) * mm, "end": v(-39.5, 41.98) * mm});
            skArc(sketch, "E6.5.5.2", {"start": v(-39.5, 41.98) * mm, "mid": v(-38.77, 40.22) * mm, "end": v(-37, 39.48) * mm});
            skLineSegment(sketch, "E6.5.5.3", {"start": v(-37, 39.48) * mm, "end": v(-12, 39.48) * mm});
            skArc(sketch, "E6.5.5.4", {"start": v(-12, 39.48) * mm, "mid": v(-10.24, 40.22) * mm, "end": v(-9.5, 41.98) * mm});
            skArc(sketch, "E6.5.5.5", {"start": v(-9.5, 41.98) * mm, "mid": v(-10.24, 43.75) * mm, "end": v(-12, 44.48) * mm});
            skLineSegment(sketch, "E6.5.6.0", {"start": v(-37, 64.48) * mm, "end": v(-12, 64.48) * mm});
            skArc(sketch, "E6.5.6.1", {"start": v(-37, 64.48) * mm, "mid": v(-38.77, 63.75) * mm, "end": v(-39.5, 61.98) * mm});
            skArc(sketch, "E6.5.6.2", {"start": v(-39.5, 61.98) * mm, "mid": v(-38.77, 60.22) * mm, "end": v(-37, 59.48) * mm});
            skLineSegment(sketch, "E6.5.6.3", {"start": v(-37, 59.48) * mm, "end": v(-12, 59.48) * mm});
            skArc(sketch, "E6.5.6.4", {"start": v(-12, 59.48) * mm, "mid": v(-10.24, 60.22) * mm, "end": v(-9.5, 61.98) * mm});
            skArc(sketch, "E6.5.6.5", {"start": v(-9.5, 61.98) * mm, "mid": v(-10.24, 63.75) * mm, "end": v(-12, 64.48) * mm});
            skLineSegment(sketch, "E6.6.0.0", {"start": v(-2, -55.52) * mm, "end": v(23, -55.52) * mm});
            skArc(sketch, "E6.6.0.1", {"start": v(-2, -55.52) * mm, "mid": v(-3.77, -56.25) * mm, "end": v(-4.5, -58.02) * mm});
            skArc(sketch, "E6.6.0.2", {"start": v(-4.5, -58.02) * mm, "mid": v(-3.77, -59.78) * mm, "end": v(-2, -60.52) * mm});
            skLineSegment(sketch, "E6.6.0.3", {"start": v(-2, -60.52) * mm, "end": v(23, -60.52) * mm});
            skArc(sketch, "E6.6.0.4", {"start": v(23, -60.52) * mm, "mid": v(24.76, -59.78) * mm, "end": v(25.5, -58.02) * mm});
            skArc(sketch, "E6.6.0.5", {"start": v(25.5, -58.02) * mm, "mid": v(24.76, -56.25) * mm, "end": v(23, -55.52) * mm});
            skLineSegment(sketch, "E6.6.1.0", {"start": v(-2, -35.52) * mm, "end": v(23, -35.52) * mm});
            skArc(sketch, "E6.6.1.1", {"start": v(-2, -35.52) * mm, "mid": v(-3.77, -36.25) * mm, "end": v(-4.5, -38.02) * mm});
            skArc(sketch, "E6.6.1.2", {"start": v(-4.5, -38.02) * mm, "mid": v(-3.77, -39.78) * mm, "end": v(-2, -40.52) * mm});
            skLineSegment(sketch, "E6.6.1.3", {"start": v(-2, -40.52) * mm, "end": v(23, -40.52) * mm});
            skArc(sketch, "E6.6.1.4", {"start": v(23, -40.52) * mm, "mid": v(24.76, -39.78) * mm, "end": v(25.5, -38.02) * mm});
            skArc(sketch, "E6.6.1.5", {"start": v(25.5, -38.02) * mm, "mid": v(24.76, -36.25) * mm, "end": v(23, -35.52) * mm});
            skLineSegment(sketch, "E6.6.2.0", {"start": v(-2, -15.52) * mm, "end": v(23, -15.52) * mm});
            skArc(sketch, "E6.6.2.1", {"start": v(-2, -15.52) * mm, "mid": v(-3.77, -16.25) * mm, "end": v(-4.5, -18.02) * mm});
            skArc(sketch, "E6.6.2.2", {"start": v(-4.5, -18.02) * mm, "mid": v(-3.77, -19.78) * mm, "end": v(-2, -20.52) * mm});
            skLineSegment(sketch, "E6.6.2.3", {"start": v(-2, -20.52) * mm, "end": v(23, -20.52) * mm});
            skArc(sketch, "E6.6.2.4", {"start": v(23, -20.52) * mm, "mid": v(24.76, -19.78) * mm, "end": v(25.5, -18.02) * mm});
            skArc(sketch, "E6.6.2.5", {"start": v(25.5, -18.02) * mm, "mid": v(24.76, -16.25) * mm, "end": v(23, -15.52) * mm});
            skLineSegment(sketch, "E6.6.3.0", {"start": v(-2, 4.48) * mm, "end": v(23, 4.48) * mm});
            skArc(sketch, "E6.6.3.1", {"start": v(-2, 4.48) * mm, "mid": v(-3.77, 3.75) * mm, "end": v(-4.5, 1.98) * mm});
            skArc(sketch, "E6.6.3.2", {"start": v(-4.5, 1.98) * mm, "mid": v(-3.77, 0.22) * mm, "end": v(-2, -0.52) * mm});
            skLineSegment(sketch, "E6.6.3.3", {"start": v(-2, -0.52) * mm, "end": v(23, -0.52) * mm});
            skArc(sketch, "E6.6.3.4", {"start": v(23, -0.52) * mm, "mid": v(24.76, 0.22) * mm, "end": v(25.5, 1.98) * mm});
            skArc(sketch, "E6.6.3.5", {"start": v(25.5, 1.98) * mm, "mid": v(24.76, 3.75) * mm, "end": v(23, 4.48) * mm});
            skLineSegment(sketch, "E6.6.4.0", {"start": v(-2, 24.48) * mm, "end": v(23, 24.48) * mm});
            skArc(sketch, "E6.6.4.1", {"start": v(-2, 24.48) * mm, "mid": v(-3.77, 23.75) * mm, "end": v(-4.5, 21.98) * mm});
            skArc(sketch, "E6.6.4.2", {"start": v(-4.5, 21.98) * mm, "mid": v(-3.77, 20.22) * mm, "end": v(-2, 19.48) * mm});
            skLineSegment(sketch, "E6.6.4.3", {"start": v(-2, 19.48) * mm, "end": v(23, 19.48) * mm});
            skArc(sketch, "E6.6.4.4", {"start": v(23, 19.48) * mm, "mid": v(24.76, 20.22) * mm, "end": v(25.5, 21.98) * mm});
            skArc(sketch, "E6.6.4.5", {"start": v(25.5, 21.98) * mm, "mid": v(24.76, 23.75) * mm, "end": v(23, 24.48) * mm});
            skLineSegment(sketch, "E6.6.5.0", {"start": v(-2, 44.48) * mm, "end": v(23, 44.48) * mm});
            skArc(sketch, "E6.6.5.1", {"start": v(-2, 44.48) * mm, "mid": v(-3.77, 43.75) * mm, "end": v(-4.5, 41.98) * mm});
            skArc(sketch, "E6.6.5.2", {"start": v(-4.5, 41.98) * mm, "mid": v(-3.77, 40.22) * mm, "end": v(-2, 39.48) * mm});
            skLineSegment(sketch, "E6.6.5.3", {"start": v(-2, 39.48) * mm, "end": v(23, 39.48) * mm});
            skArc(sketch, "E6.6.5.4", {"start": v(23, 39.48) * mm, "mid": v(24.76, 40.22) * mm, "end": v(25.5, 41.98) * mm});
            skArc(sketch, "E6.6.5.5", {"start": v(25.5, 41.98) * mm, "mid": v(24.76, 43.75) * mm, "end": v(23, 44.48) * mm});
            skLineSegment(sketch, "E6.6.6.0", {"start": v(-2, 64.48) * mm, "end": v(23, 64.48) * mm});
            skArc(sketch, "E6.6.6.1", {"start": v(-2, 64.48) * mm, "mid": v(-3.77, 63.75) * mm, "end": v(-4.5, 61.98) * mm});
            skArc(sketch, "E6.6.6.2", {"start": v(-4.5, 61.98) * mm, "mid": v(-3.77, 60.22) * mm, "end": v(-2, 59.48) * mm});
            skLineSegment(sketch, "E6.6.6.3", {"start": v(-2, 59.48) * mm, "end": v(23, 59.48) * mm});
            skArc(sketch, "E6.6.6.4", {"start": v(23, 59.48) * mm, "mid": v(24.76, 60.22) * mm, "end": v(25.5, 61.98) * mm});
            skArc(sketch, "E6.6.6.5", {"start": v(25.5, 61.98) * mm, "mid": v(24.76, 63.75) * mm, "end": v(23, 64.48) * mm});
            skLineSegment(sketch, "E6.7.0.0", {"start": v(33, -55.52) * mm, "end": v(58, -55.52) * mm});
            skArc(sketch, "E6.7.0.1", {"start": v(33, -55.52) * mm, "mid": v(31.23, -56.25) * mm, "end": v(30.5, -58.02) * mm});
            skArc(sketch, "E6.7.0.2", {"start": v(30.5, -58.02) * mm, "mid": v(31.23, -59.78) * mm, "end": v(33, -60.52) * mm});
            skLineSegment(sketch, "E6.7.0.3", {"start": v(33, -60.52) * mm, "end": v(58, -60.52) * mm});
            skArc(sketch, "E6.7.0.4", {"start": v(58, -60.52) * mm, "mid": v(59.76, -59.78) * mm, "end": v(60.5, -58.02) * mm});
            skArc(sketch, "E6.7.0.5", {"start": v(60.5, -58.02) * mm, "mid": v(59.76, -56.25) * mm, "end": v(58, -55.52) * mm});
            skLineSegment(sketch, "E6.7.1.0", {"start": v(33, -35.52) * mm, "end": v(58, -35.52) * mm});
            skArc(sketch, "E6.7.1.1", {"start": v(33, -35.52) * mm, "mid": v(31.23, -36.25) * mm, "end": v(30.5, -38.02) * mm});
            skArc(sketch, "E6.7.1.2", {"start": v(30.5, -38.02) * mm, "mid": v(31.23, -39.78) * mm, "end": v(33, -40.52) * mm});
            skLineSegment(sketch, "E6.7.1.3", {"start": v(33, -40.52) * mm, "end": v(58, -40.52) * mm});
            skArc(sketch, "E6.7.1.4", {"start": v(58, -40.52) * mm, "mid": v(59.76, -39.78) * mm, "end": v(60.5, -38.02) * mm});
            skArc(sketch, "E6.7.1.5", {"start": v(60.5, -38.02) * mm, "mid": v(59.76, -36.25) * mm, "end": v(58, -35.52) * mm});
            skLineSegment(sketch, "E6.7.2.0", {"start": v(33, -15.52) * mm, "end": v(58, -15.52) * mm});
            skArc(sketch, "E6.7.2.1", {"start": v(33, -15.52) * mm, "mid": v(31.23, -16.25) * mm, "end": v(30.5, -18.02) * mm});
            skArc(sketch, "E6.7.2.2", {"start": v(30.5, -18.02) * mm, "mid": v(31.23, -19.78) * mm, "end": v(33, -20.52) * mm});
            skLineSegment(sketch, "E6.7.2.3", {"start": v(33, -20.52) * mm, "end": v(58, -20.52) * mm});
            skArc(sketch, "E6.7.2.4", {"start": v(58, -20.52) * mm, "mid": v(59.76, -19.78) * mm, "end": v(60.5, -18.02) * mm});
            skArc(sketch, "E6.7.2.5", {"start": v(60.5, -18.02) * mm, "mid": v(59.76, -16.25) * mm, "end": v(58, -15.52) * mm});
            skLineSegment(sketch, "E6.7.3.0", {"start": v(33, 4.48) * mm, "end": v(58, 4.48) * mm});
            skArc(sketch, "E6.7.3.1", {"start": v(33, 4.48) * mm, "mid": v(31.23, 3.75) * mm, "end": v(30.5, 1.98) * mm});
            skArc(sketch, "E6.7.3.2", {"start": v(30.5, 1.98) * mm, "mid": v(31.23, 0.22) * mm, "end": v(33, -0.52) * mm});
            skLineSegment(sketch, "E6.7.3.3", {"start": v(33, -0.52) * mm, "end": v(58, -0.52) * mm});
            skArc(sketch, "E6.7.3.4", {"start": v(58, -0.52) * mm, "mid": v(59.76, 0.22) * mm, "end": v(60.5, 1.98) * mm});
            skArc(sketch, "E6.7.3.5", {"start": v(60.5, 1.98) * mm, "mid": v(59.76, 3.75) * mm, "end": v(58, 4.48) * mm});
            skLineSegment(sketch, "E6.7.4.0", {"start": v(33, 24.48) * mm, "end": v(58, 24.48) * mm});
            skArc(sketch, "E6.7.4.1", {"start": v(33, 24.48) * mm, "mid": v(31.23, 23.75) * mm, "end": v(30.5, 21.98) * mm});
            skArc(sketch, "E6.7.4.2", {"start": v(30.5, 21.98) * mm, "mid": v(31.23, 20.22) * mm, "end": v(33, 19.48) * mm});
            skLineSegment(sketch, "E6.7.4.3", {"start": v(33, 19.48) * mm, "end": v(58, 19.48) * mm});
            skArc(sketch, "E6.7.4.4", {"start": v(58, 19.48) * mm, "mid": v(59.76, 20.22) * mm, "end": v(60.5, 21.98) * mm});
            skArc(sketch, "E6.7.4.5", {"start": v(60.5, 21.98) * mm, "mid": v(59.76, 23.75) * mm, "end": v(58, 24.48) * mm});
            skLineSegment(sketch, "E6.7.5.0", {"start": v(33, 44.48) * mm, "end": v(58, 44.48) * mm});
            skArc(sketch, "E6.7.5.1", {"start": v(33, 44.48) * mm, "mid": v(31.23, 43.75) * mm, "end": v(30.5, 41.98) * mm});
            skArc(sketch, "E6.7.5.2", {"start": v(30.5, 41.98) * mm, "mid": v(31.23, 40.22) * mm, "end": v(33, 39.48) * mm});
            skLineSegment(sketch, "E6.7.5.3", {"start": v(33, 39.48) * mm, "end": v(58, 39.48) * mm});
            skArc(sketch, "E6.7.5.4", {"start": v(58, 39.48) * mm, "mid": v(59.76, 40.22) * mm, "end": v(60.5, 41.98) * mm});
            skArc(sketch, "E6.7.5.5", {"start": v(60.5, 41.98) * mm, "mid": v(59.76, 43.75) * mm, "end": v(58, 44.48) * mm});
            skLineSegment(sketch, "E6.7.6.0", {"start": v(33, 64.48) * mm, "end": v(58, 64.48) * mm});
            skArc(sketch, "E6.7.6.1", {"start": v(33, 64.48) * mm, "mid": v(31.23, 63.75) * mm, "end": v(30.5, 61.98) * mm});
            skArc(sketch, "E6.7.6.2", {"start": v(30.5, 61.98) * mm, "mid": v(31.23, 60.22) * mm, "end": v(33, 59.48) * mm});
            skLineSegment(sketch, "E6.7.6.3", {"start": v(33, 59.48) * mm, "end": v(58, 59.48) * mm});
            skArc(sketch, "E6.7.6.4", {"start": v(58, 59.48) * mm, "mid": v(59.76, 60.22) * mm, "end": v(60.5, 61.98) * mm});
            skArc(sketch, "E6.7.6.5", {"start": v(60.5, 61.98) * mm, "mid": v(59.76, 63.75) * mm, "end": v(58, 64.48) * mm});
            skLineSegment(sketch, "E6.8.0.0", {"start": v(68, -55.52) * mm, "end": v(93, -55.52) * mm});
            skArc(sketch, "E6.8.0.1", {"start": v(68, -55.52) * mm, "mid": v(66.23, -56.25) * mm, "end": v(65.5, -58.02) * mm});
            skArc(sketch, "E6.8.0.2", {"start": v(65.5, -58.02) * mm, "mid": v(66.23, -59.78) * mm, "end": v(68, -60.52) * mm});
            skLineSegment(sketch, "E6.8.0.3", {"start": v(68, -60.52) * mm, "end": v(93, -60.52) * mm});
            skArc(sketch, "E6.8.0.4", {"start": v(93, -60.52) * mm, "mid": v(94.76, -59.78) * mm, "end": v(95.5, -58.02) * mm});
            skArc(sketch, "E6.8.0.5", {"start": v(95.5, -58.02) * mm, "mid": v(94.76, -56.25) * mm, "end": v(93, -55.52) * mm});
            skLineSegment(sketch, "E6.8.1.0", {"start": v(68, -35.52) * mm, "end": v(93, -35.52) * mm});
            skArc(sketch, "E6.8.1.1", {"start": v(68, -35.52) * mm, "mid": v(66.23, -36.25) * mm, "end": v(65.5, -38.02) * mm});
            skArc(sketch, "E6.8.1.2", {"start": v(65.5, -38.02) * mm, "mid": v(66.23, -39.78) * mm, "end": v(68, -40.52) * mm});
            skLineSegment(sketch, "E6.8.1.3", {"start": v(68, -40.52) * mm, "end": v(93, -40.52) * mm});
            skArc(sketch, "E6.8.1.4", {"start": v(93, -40.52) * mm, "mid": v(94.76, -39.78) * mm, "end": v(95.5, -38.02) * mm});
            skArc(sketch, "E6.8.1.5", {"start": v(95.5, -38.02) * mm, "mid": v(94.76, -36.25) * mm, "end": v(93, -35.52) * mm});
            skLineSegment(sketch, "E6.8.2.0", {"start": v(68, -15.52) * mm, "end": v(93, -15.52) * mm});
            skArc(sketch, "E6.8.2.1", {"start": v(68, -15.52) * mm, "mid": v(66.23, -16.25) * mm, "end": v(65.5, -18.02) * mm});
            skArc(sketch, "E6.8.2.2", {"start": v(65.5, -18.02) * mm, "mid": v(66.23, -19.78) * mm, "end": v(68, -20.52) * mm});
            skLineSegment(sketch, "E6.8.2.3", {"start": v(68, -20.52) * mm, "end": v(93, -20.52) * mm});
            skArc(sketch, "E6.8.2.4", {"start": v(93, -20.52) * mm, "mid": v(94.76, -19.78) * mm, "end": v(95.5, -18.02) * mm});
            skArc(sketch, "E6.8.2.5", {"start": v(95.5, -18.02) * mm, "mid": v(94.76, -16.25) * mm, "end": v(93, -15.52) * mm});
            skLineSegment(sketch, "E6.8.3.0", {"start": v(68, 4.48) * mm, "end": v(93, 4.48) * mm});
            skArc(sketch, "E6.8.3.1", {"start": v(68, 4.48) * mm, "mid": v(66.23, 3.75) * mm, "end": v(65.5, 1.98) * mm});
            skArc(sketch, "E6.8.3.2", {"start": v(65.5, 1.98) * mm, "mid": v(66.23, 0.22) * mm, "end": v(68, -0.52) * mm});
            skLineSegment(sketch, "E6.8.3.3", {"start": v(68, -0.52) * mm, "end": v(93, -0.52) * mm});
            skArc(sketch, "E6.8.3.4", {"start": v(93, -0.52) * mm, "mid": v(94.76, 0.22) * mm, "end": v(95.5, 1.98) * mm});
            skArc(sketch, "E6.8.3.5", {"start": v(95.5, 1.98) * mm, "mid": v(94.76, 3.75) * mm, "end": v(93, 4.48) * mm});
            skLineSegment(sketch, "E6.8.4.0", {"start": v(68, 24.48) * mm, "end": v(93, 24.48) * mm});
            skArc(sketch, "E6.8.4.1", {"start": v(68, 24.48) * mm, "mid": v(66.23, 23.75) * mm, "end": v(65.5, 21.98) * mm});
            skArc(sketch, "E6.8.4.2", {"start": v(65.5, 21.98) * mm, "mid": v(66.23, 20.22) * mm, "end": v(68, 19.48) * mm});
            skLineSegment(sketch, "E6.8.4.3", {"start": v(68, 19.48) * mm, "end": v(93, 19.48) * mm});
            skArc(sketch, "E6.8.4.4", {"start": v(93, 19.48) * mm, "mid": v(94.76, 20.22) * mm, "end": v(95.5, 21.98) * mm});
            skArc(sketch, "E6.8.4.5", {"start": v(95.5, 21.98) * mm, "mid": v(94.76, 23.75) * mm, "end": v(93, 24.48) * mm});
            skLineSegment(sketch, "E6.8.5.0", {"start": v(68, 44.48) * mm, "end": v(93, 44.48) * mm});
            skArc(sketch, "E6.8.5.1", {"start": v(68, 44.48) * mm, "mid": v(66.23, 43.75) * mm, "end": v(65.5, 41.98) * mm});
            skArc(sketch, "E6.8.5.2", {"start": v(65.5, 41.98) * mm, "mid": v(66.23, 40.22) * mm, "end": v(68, 39.48) * mm});
            skLineSegment(sketch, "E6.8.5.3", {"start": v(68, 39.48) * mm, "end": v(93, 39.48) * mm});
            skArc(sketch, "E6.8.5.4", {"start": v(93, 39.48) * mm, "mid": v(94.76, 40.22) * mm, "end": v(95.5, 41.98) * mm});
            skArc(sketch, "E6.8.5.5", {"start": v(95.5, 41.98) * mm, "mid": v(94.76, 43.75) * mm, "end": v(93, 44.48) * mm});
            skLineSegment(sketch, "E6.8.6.0", {"start": v(68, 64.48) * mm, "end": v(93, 64.48) * mm});
            skArc(sketch, "E6.8.6.1", {"start": v(68, 64.48) * mm, "mid": v(66.23, 63.75) * mm, "end": v(65.5, 61.98) * mm});
            skArc(sketch, "E6.8.6.2", {"start": v(65.5, 61.98) * mm, "mid": v(66.23, 60.22) * mm, "end": v(68, 59.48) * mm});
            skLineSegment(sketch, "E6.8.6.3", {"start": v(68, 59.48) * mm, "end": v(93, 59.48) * mm});
            skArc(sketch, "E6.8.6.4", {"start": v(93, 59.48) * mm, "mid": v(94.76, 60.22) * mm, "end": v(95.5, 61.98) * mm});
            skArc(sketch, "E6.8.6.5", {"start": v(95.5, 61.98) * mm, "mid": v(94.76, 63.75) * mm, "end": v(93, 64.48) * mm});
            skLineSegment(sketch, "E6.9.0.0", {"start": v(103, -55.52) * mm, "end": v(128, -55.52) * mm});
            skArc(sketch, "E6.9.0.1", {"start": v(103, -55.52) * mm, "mid": v(101.23, -56.25) * mm, "end": v(100.5, -58.02) * mm});
            skArc(sketch, "E6.9.0.2", {"start": v(100.5, -58.02) * mm, "mid": v(101.23, -59.78) * mm, "end": v(103, -60.52) * mm});
            skLineSegment(sketch, "E6.9.0.3", {"start": v(103, -60.52) * mm, "end": v(128, -60.52) * mm});
            skArc(sketch, "E6.9.0.4", {"start": v(128, -60.52) * mm, "mid": v(129.76, -59.78) * mm, "end": v(130.5, -58.02) * mm});
            skArc(sketch, "E6.9.0.5", {"start": v(130.5, -58.02) * mm, "mid": v(129.76, -56.25) * mm, "end": v(128, -55.52) * mm});
            skLineSegment(sketch, "E6.9.1.0", {"start": v(103, -35.52) * mm, "end": v(128, -35.52) * mm});
            skArc(sketch, "E6.9.1.1", {"start": v(103, -35.52) * mm, "mid": v(101.23, -36.25) * mm, "end": v(100.5, -38.02) * mm});
            skArc(sketch, "E6.9.1.2", {"start": v(100.5, -38.02) * mm, "mid": v(101.23, -39.78) * mm, "end": v(103, -40.52) * mm});
            skLineSegment(sketch, "E6.9.1.3", {"start": v(103, -40.52) * mm, "end": v(128, -40.52) * mm});
            skArc(sketch, "E6.9.1.4", {"start": v(128, -40.52) * mm, "mid": v(129.76, -39.78) * mm, "end": v(130.5, -38.02) * mm});
            skArc(sketch, "E6.9.1.5", {"start": v(130.5, -38.02) * mm, "mid": v(129.76, -36.25) * mm, "end": v(128, -35.52) * mm});
            skLineSegment(sketch, "E6.9.2.0", {"start": v(103, -15.52) * mm, "end": v(128, -15.52) * mm});
            skArc(sketch, "E6.9.2.1", {"start": v(103, -15.52) * mm, "mid": v(101.23, -16.25) * mm, "end": v(100.5, -18.02) * mm});
            skArc(sketch, "E6.9.2.2", {"start": v(100.5, -18.02) * mm, "mid": v(101.23, -19.78) * mm, "end": v(103, -20.52) * mm});
            skLineSegment(sketch, "E6.9.2.3", {"start": v(103, -20.52) * mm, "end": v(128, -20.52) * mm});
            skArc(sketch, "E6.9.2.4", {"start": v(128, -20.52) * mm, "mid": v(129.76, -19.78) * mm, "end": v(130.5, -18.02) * mm});
            skArc(sketch, "E6.9.2.5", {"start": v(130.5, -18.02) * mm, "mid": v(129.76, -16.25) * mm, "end": v(128, -15.52) * mm});
            skLineSegment(sketch, "E6.9.3.0", {"start": v(103, 4.48) * mm, "end": v(128, 4.48) * mm});
            skArc(sketch, "E6.9.3.1", {"start": v(103, 4.48) * mm, "mid": v(101.23, 3.75) * mm, "end": v(100.5, 1.98) * mm});
            skArc(sketch, "E6.9.3.2", {"start": v(100.5, 1.98) * mm, "mid": v(101.23, 0.22) * mm, "end": v(103, -0.52) * mm});
            skLineSegment(sketch, "E6.9.3.3", {"start": v(103, -0.52) * mm, "end": v(128, -0.52) * mm});
            skArc(sketch, "E6.9.3.4", {"start": v(128, -0.52) * mm, "mid": v(129.76, 0.22) * mm, "end": v(130.5, 1.98) * mm});
            skArc(sketch, "E6.9.3.5", {"start": v(130.5, 1.98) * mm, "mid": v(129.76, 3.75) * mm, "end": v(128, 4.48) * mm});
            skLineSegment(sketch, "E6.9.4.0", {"start": v(103, 24.48) * mm, "end": v(128, 24.48) * mm});
            skArc(sketch, "E6.9.4.1", {"start": v(103, 24.48) * mm, "mid": v(101.23, 23.75) * mm, "end": v(100.5, 21.98) * mm});
            skArc(sketch, "E6.9.4.2", {"start": v(100.5, 21.98) * mm, "mid": v(101.23, 20.22) * mm, "end": v(103, 19.48) * mm});
            skLineSegment(sketch, "E6.9.4.3", {"start": v(103, 19.48) * mm, "end": v(128, 19.48) * mm});
            skArc(sketch, "E6.9.4.4", {"start": v(128, 19.48) * mm, "mid": v(129.76, 20.22) * mm, "end": v(130.5, 21.98) * mm});
            skArc(sketch, "E6.9.4.5", {"start": v(130.5, 21.98) * mm, "mid": v(129.76, 23.75) * mm, "end": v(128, 24.48) * mm});
            skLineSegment(sketch, "E6.9.5.0", {"start": v(103, 44.48) * mm, "end": v(128, 44.48) * mm});
            skArc(sketch, "E6.9.5.1", {"start": v(103, 44.48) * mm, "mid": v(101.23, 43.75) * mm, "end": v(100.5, 41.98) * mm});
            skArc(sketch, "E6.9.5.2", {"start": v(100.5, 41.98) * mm, "mid": v(101.23, 40.22) * mm, "end": v(103, 39.48) * mm});
            skLineSegment(sketch, "E6.9.5.3", {"start": v(103, 39.48) * mm, "end": v(128, 39.48) * mm});
            skArc(sketch, "E6.9.5.4", {"start": v(128, 39.48) * mm, "mid": v(129.76, 40.22) * mm, "end": v(130.5, 41.98) * mm});
            skArc(sketch, "E6.9.5.5", {"start": v(130.5, 41.98) * mm, "mid": v(129.76, 43.75) * mm, "end": v(128, 44.48) * mm});
            skLineSegment(sketch, "E6.9.6.0", {"start": v(103, 64.48) * mm, "end": v(128, 64.48) * mm});
            skArc(sketch, "E6.9.6.1", {"start": v(103, 64.48) * mm, "mid": v(101.23, 63.75) * mm, "end": v(100.5, 61.98) * mm});
            skArc(sketch, "E6.9.6.2", {"start": v(100.5, 61.98) * mm, "mid": v(101.23, 60.22) * mm, "end": v(103, 59.48) * mm});
            skLineSegment(sketch, "E6.9.6.3", {"start": v(103, 59.48) * mm, "end": v(128, 59.48) * mm});
            skArc(sketch, "E6.9.6.4", {"start": v(128, 59.48) * mm, "mid": v(129.76, 60.22) * mm, "end": v(130.5, 61.98) * mm});
            skArc(sketch, "E6.9.6.5", {"start": v(130.5, 61.98) * mm, "mid": v(129.76, 63.75) * mm, "end": v(128, 64.48) * mm});
            skLineSegment(sketch, "E6.10.0.0", {"start": v(138, -55.52) * mm, "end": v(163, -55.52) * mm});
            skArc(sketch, "E6.10.0.1", {"start": v(138, -55.52) * mm, "mid": v(136.23, -56.25) * mm, "end": v(135.5, -58.02) * mm});
            skArc(sketch, "E6.10.0.2", {"start": v(135.5, -58.02) * mm, "mid": v(136.23, -59.78) * mm, "end": v(138, -60.52) * mm});
            skLineSegment(sketch, "E6.10.0.3", {"start": v(138, -60.52) * mm, "end": v(163, -60.52) * mm});
            skArc(sketch, "E6.10.0.4", {"start": v(163, -60.52) * mm, "mid": v(164.76, -59.78) * mm, "end": v(165.5, -58.02) * mm});
            skArc(sketch, "E6.10.0.5", {"start": v(165.5, -58.02) * mm, "mid": v(164.76, -56.25) * mm, "end": v(163, -55.52) * mm});
            skLineSegment(sketch, "E6.10.1.0", {"start": v(138, -35.52) * mm, "end": v(163, -35.52) * mm});
            skArc(sketch, "E6.10.1.1", {"start": v(138, -35.52) * mm, "mid": v(136.23, -36.25) * mm, "end": v(135.5, -38.02) * mm});
            skArc(sketch, "E6.10.1.2", {"start": v(135.5, -38.02) * mm, "mid": v(136.23, -39.78) * mm, "end": v(138, -40.52) * mm});
            skLineSegment(sketch, "E6.10.1.3", {"start": v(138, -40.52) * mm, "end": v(163, -40.52) * mm});
            skArc(sketch, "E6.10.1.4", {"start": v(163, -40.52) * mm, "mid": v(164.76, -39.78) * mm, "end": v(165.5, -38.02) * mm});
            skArc(sketch, "E6.10.1.5", {"start": v(165.5, -38.02) * mm, "mid": v(164.76, -36.25) * mm, "end": v(163, -35.52) * mm});
            skLineSegment(sketch, "E6.10.2.0", {"start": v(138, -15.52) * mm, "end": v(163, -15.52) * mm});
            skArc(sketch, "E6.10.2.1", {"start": v(138, -15.52) * mm, "mid": v(136.23, -16.25) * mm, "end": v(135.5, -18.02) * mm});
            skArc(sketch, "E6.10.2.2", {"start": v(135.5, -18.02) * mm, "mid": v(136.23, -19.78) * mm, "end": v(138, -20.52) * mm});
            skLineSegment(sketch, "E6.10.2.3", {"start": v(138, -20.52) * mm, "end": v(163, -20.52) * mm});
            skArc(sketch, "E6.10.2.4", {"start": v(163, -20.52) * mm, "mid": v(164.76, -19.78) * mm, "end": v(165.5, -18.02) * mm});
            skArc(sketch, "E6.10.2.5", {"start": v(165.5, -18.02) * mm, "mid": v(164.76, -16.25) * mm, "end": v(163, -15.52) * mm});
            skLineSegment(sketch, "E6.10.3.0", {"start": v(138, 4.48) * mm, "end": v(163, 4.48) * mm});
            skArc(sketch, "E6.10.3.1", {"start": v(138, 4.48) * mm, "mid": v(136.23, 3.75) * mm, "end": v(135.5, 1.98) * mm});
            skArc(sketch, "E6.10.3.2", {"start": v(135.5, 1.98) * mm, "mid": v(136.23, 0.22) * mm, "end": v(138, -0.52) * mm});
            skLineSegment(sketch, "E6.10.3.3", {"start": v(138, -0.52) * mm, "end": v(163, -0.52) * mm});
            skArc(sketch, "E6.10.3.4", {"start": v(163, -0.52) * mm, "mid": v(164.76, 0.22) * mm, "end": v(165.5, 1.98) * mm});
            skArc(sketch, "E6.10.3.5", {"start": v(165.5, 1.98) * mm, "mid": v(164.76, 3.75) * mm, "end": v(163, 4.48) * mm});
            skLineSegment(sketch, "E6.10.4.0", {"start": v(138, 24.48) * mm, "end": v(163, 24.48) * mm});
            skArc(sketch, "E6.10.4.1", {"start": v(138, 24.48) * mm, "mid": v(136.23, 23.75) * mm, "end": v(135.5, 21.98) * mm});
            skArc(sketch, "E6.10.4.2", {"start": v(135.5, 21.98) * mm, "mid": v(136.23, 20.22) * mm, "end": v(138, 19.48) * mm});
            skLineSegment(sketch, "E6.10.4.3", {"start": v(138, 19.48) * mm, "end": v(163, 19.48) * mm});
            skArc(sketch, "E6.10.4.4", {"start": v(163, 19.48) * mm, "mid": v(164.76, 20.22) * mm, "end": v(165.5, 21.98) * mm});
            skArc(sketch, "E6.10.4.5", {"start": v(165.5, 21.98) * mm, "mid": v(164.76, 23.75) * mm, "end": v(163, 24.48) * mm});
            skLineSegment(sketch, "E6.10.5.0", {"start": v(138, 44.48) * mm, "end": v(163, 44.48) * mm});
            skArc(sketch, "E6.10.5.1", {"start": v(138, 44.48) * mm, "mid": v(136.23, 43.75) * mm, "end": v(135.5, 41.98) * mm});
            skArc(sketch, "E6.10.5.2", {"start": v(135.5, 41.98) * mm, "mid": v(136.23, 40.22) * mm, "end": v(138, 39.48) * mm});
            skLineSegment(sketch, "E6.10.5.3", {"start": v(138, 39.48) * mm, "end": v(163, 39.48) * mm});
            skArc(sketch, "E6.10.5.4", {"start": v(163, 39.48) * mm, "mid": v(164.76, 40.22) * mm, "end": v(165.5, 41.98) * mm});
            skArc(sketch, "E6.10.5.5", {"start": v(165.5, 41.98) * mm, "mid": v(164.76, 43.75) * mm, "end": v(163, 44.48) * mm});
            skLineSegment(sketch, "E6.10.6.0", {"start": v(138, 64.48) * mm, "end": v(163, 64.48) * mm});
            skArc(sketch, "E6.10.6.1", {"start": v(138, 64.48) * mm, "mid": v(136.23, 63.75) * mm, "end": v(135.5, 61.98) * mm});
            skArc(sketch, "E6.10.6.2", {"start": v(135.5, 61.98) * mm, "mid": v(136.23, 60.22) * mm, "end": v(138, 59.48) * mm});
            skLineSegment(sketch, "E6.10.6.3", {"start": v(138, 59.48) * mm, "end": v(163, 59.48) * mm});
            skArc(sketch, "E6.10.6.4", {"start": v(163, 59.48) * mm, "mid": v(164.76, 60.22) * mm, "end": v(165.5, 61.98) * mm});
            skArc(sketch, "E6.10.6.5", {"start": v(165.5, 61.98) * mm, "mid": v(164.76, 63.75) * mm, "end": v(163, 64.48) * mm});
            skLineSegment(sketch, "E6.11.0.0", {"start": v(173, -55.52) * mm, "end": v(198, -55.52) * mm});
            skArc(sketch, "E6.11.0.1", {"start": v(173, -55.52) * mm, "mid": v(171.23, -56.25) * mm, "end": v(170.5, -58.02) * mm});
            skArc(sketch, "E6.11.0.2", {"start": v(170.5, -58.02) * mm, "mid": v(171.23, -59.78) * mm, "end": v(173, -60.52) * mm});
            skLineSegment(sketch, "E6.11.0.3", {"start": v(173, -60.52) * mm, "end": v(198, -60.52) * mm});
            skArc(sketch, "E6.11.0.4", {"start": v(198, -60.52) * mm, "mid": v(199.76, -59.78) * mm, "end": v(200.5, -58.02) * mm});
            skArc(sketch, "E6.11.0.5", {"start": v(200.5, -58.02) * mm, "mid": v(199.76, -56.25) * mm, "end": v(198, -55.52) * mm});
            skLineSegment(sketch, "E6.11.1.0", {"start": v(173, -35.52) * mm, "end": v(198, -35.52) * mm});
            skArc(sketch, "E6.11.1.1", {"start": v(173, -35.52) * mm, "mid": v(171.23, -36.25) * mm, "end": v(170.5, -38.02) * mm});
            skArc(sketch, "E6.11.1.2", {"start": v(170.5, -38.02) * mm, "mid": v(171.23, -39.78) * mm, "end": v(173, -40.52) * mm});
            skLineSegment(sketch, "E6.11.1.3", {"start": v(173, -40.52) * mm, "end": v(198, -40.52) * mm});
            skArc(sketch, "E6.11.1.4", {"start": v(198, -40.52) * mm, "mid": v(199.76, -39.78) * mm, "end": v(200.5, -38.02) * mm});
            skArc(sketch, "E6.11.1.5", {"start": v(200.5, -38.02) * mm, "mid": v(199.76, -36.25) * mm, "end": v(198, -35.52) * mm});
            skLineSegment(sketch, "E6.11.2.0", {"start": v(173, -15.52) * mm, "end": v(198, -15.52) * mm});
            skArc(sketch, "E6.11.2.1", {"start": v(173, -15.52) * mm, "mid": v(171.23, -16.25) * mm, "end": v(170.5, -18.02) * mm});
            skArc(sketch, "E6.11.2.2", {"start": v(170.5, -18.02) * mm, "mid": v(171.23, -19.78) * mm, "end": v(173, -20.52) * mm});
            skLineSegment(sketch, "E6.11.2.3", {"start": v(173, -20.52) * mm, "end": v(198, -20.52) * mm});
            skArc(sketch, "E6.11.2.4", {"start": v(198, -20.52) * mm, "mid": v(199.76, -19.78) * mm, "end": v(200.5, -18.02) * mm});
            skArc(sketch, "E6.11.2.5", {"start": v(200.5, -18.02) * mm, "mid": v(199.76, -16.25) * mm, "end": v(198, -15.52) * mm});
            skLineSegment(sketch, "E6.11.3.0", {"start": v(173, 4.48) * mm, "end": v(198, 4.48) * mm});
            skArc(sketch, "E6.11.3.1", {"start": v(173, 4.48) * mm, "mid": v(171.23, 3.75) * mm, "end": v(170.5, 1.98) * mm});
            skArc(sketch, "E6.11.3.2", {"start": v(170.5, 1.98) * mm, "mid": v(171.23, 0.22) * mm, "end": v(173, -0.52) * mm});
            skLineSegment(sketch, "E6.11.3.3", {"start": v(173, -0.52) * mm, "end": v(198, -0.52) * mm});
            skArc(sketch, "E6.11.3.4", {"start": v(198, -0.52) * mm, "mid": v(199.76, 0.22) * mm, "end": v(200.5, 1.98) * mm});
            skArc(sketch, "E6.11.3.5", {"start": v(200.5, 1.98) * mm, "mid": v(199.76, 3.75) * mm, "end": v(198, 4.48) * mm});
            skLineSegment(sketch, "E6.11.4.0", {"start": v(173, 24.48) * mm, "end": v(198, 24.48) * mm});
            skArc(sketch, "E6.11.4.1", {"start": v(173, 24.48) * mm, "mid": v(171.23, 23.75) * mm, "end": v(170.5, 21.98) * mm});
            skArc(sketch, "E6.11.4.2", {"start": v(170.5, 21.98) * mm, "mid": v(171.23, 20.22) * mm, "end": v(173, 19.48) * mm});
            skLineSegment(sketch, "E6.11.4.3", {"start": v(173, 19.48) * mm, "end": v(198, 19.48) * mm});
            skArc(sketch, "E6.11.4.4", {"start": v(198, 19.48) * mm, "mid": v(199.76, 20.22) * mm, "end": v(200.5, 21.98) * mm});
            skArc(sketch, "E6.11.4.5", {"start": v(200.5, 21.98) * mm, "mid": v(199.76, 23.75) * mm, "end": v(198, 24.48) * mm});
            skLineSegment(sketch, "E6.11.5.0", {"start": v(173, 44.48) * mm, "end": v(198, 44.48) * mm});
            skArc(sketch, "E6.11.5.1", {"start": v(173, 44.48) * mm, "mid": v(171.23, 43.75) * mm, "end": v(170.5, 41.98) * mm});
            skArc(sketch, "E6.11.5.2", {"start": v(170.5, 41.98) * mm, "mid": v(171.23, 40.22) * mm, "end": v(173, 39.48) * mm});
            skLineSegment(sketch, "E6.11.5.3", {"start": v(173, 39.48) * mm, "end": v(198, 39.48) * mm});
            skArc(sketch, "E6.11.5.4", {"start": v(198, 39.48) * mm, "mid": v(199.76, 40.22) * mm, "end": v(200.5, 41.98) * mm});
            skArc(sketch, "E6.11.5.5", {"start": v(200.5, 41.98) * mm, "mid": v(199.76, 43.75) * mm, "end": v(198, 44.48) * mm});
            skLineSegment(sketch, "E6.11.6.0", {"start": v(173, 64.48) * mm, "end": v(198, 64.48) * mm});
            skArc(sketch, "E6.11.6.1", {"start": v(173, 64.48) * mm, "mid": v(171.23, 63.75) * mm, "end": v(170.5, 61.98) * mm});
            skArc(sketch, "E6.11.6.2", {"start": v(170.5, 61.98) * mm, "mid": v(171.23, 60.22) * mm, "end": v(173, 59.48) * mm});
            skLineSegment(sketch, "E6.11.6.3", {"start": v(173, 59.48) * mm, "end": v(198, 59.48) * mm});
            skArc(sketch, "E6.11.6.4", {"start": v(198, 59.48) * mm, "mid": v(199.76, 60.22) * mm, "end": v(200.5, 61.98) * mm});
            skArc(sketch, "E6.11.6.5", {"start": v(200.5, 61.98) * mm, "mid": v(199.76, 63.75) * mm, "end": v(198, 64.48) * mm});
            skLineSegment(sketch, "E6.12.0.0", {"start": v(208, -55.52) * mm, "end": v(233, -55.52) * mm});
            skArc(sketch, "E6.12.0.1", {"start": v(208, -55.52) * mm, "mid": v(206.23, -56.25) * mm, "end": v(205.5, -58.02) * mm});
            skArc(sketch, "E6.12.0.2", {"start": v(205.5, -58.02) * mm, "mid": v(206.23, -59.78) * mm, "end": v(208, -60.52) * mm});
            skLineSegment(sketch, "E6.12.0.3", {"start": v(208, -60.52) * mm, "end": v(233, -60.52) * mm});
            skArc(sketch, "E6.12.0.4", {"start": v(233, -60.52) * mm, "mid": v(234.76, -59.78) * mm, "end": v(235.5, -58.02) * mm});
            skArc(sketch, "E6.12.0.5", {"start": v(235.5, -58.02) * mm, "mid": v(234.76, -56.25) * mm, "end": v(233, -55.52) * mm});
            skLineSegment(sketch, "E6.12.1.0", {"start": v(208, -35.52) * mm, "end": v(233, -35.52) * mm});
            skArc(sketch, "E6.12.1.1", {"start": v(208, -35.52) * mm, "mid": v(206.23, -36.25) * mm, "end": v(205.5, -38.02) * mm});
            skArc(sketch, "E6.12.1.2", {"start": v(205.5, -38.02) * mm, "mid": v(206.23, -39.78) * mm, "end": v(208, -40.52) * mm});
            skLineSegment(sketch, "E6.12.1.3", {"start": v(208, -40.52) * mm, "end": v(233, -40.52) * mm});
            skArc(sketch, "E6.12.1.4", {"start": v(233, -40.52) * mm, "mid": v(234.76, -39.78) * mm, "end": v(235.5, -38.02) * mm});
            skArc(sketch, "E6.12.1.5", {"start": v(235.5, -38.02) * mm, "mid": v(234.76, -36.25) * mm, "end": v(233, -35.52) * mm});
            skLineSegment(sketch, "E6.12.2.0", {"start": v(208, -15.52) * mm, "end": v(233, -15.52) * mm});
            skArc(sketch, "E6.12.2.1", {"start": v(208, -15.52) * mm, "mid": v(206.23, -16.25) * mm, "end": v(205.5, -18.02) * mm});
            skArc(sketch, "E6.12.2.2", {"start": v(205.5, -18.02) * mm, "mid": v(206.23, -19.78) * mm, "end": v(208, -20.52) * mm});
            skLineSegment(sketch, "E6.12.2.3", {"start": v(208, -20.52) * mm, "end": v(233, -20.52) * mm});
            skArc(sketch, "E6.12.2.4", {"start": v(233, -20.52) * mm, "mid": v(234.76, -19.78) * mm, "end": v(235.5, -18.02) * mm});
            skArc(sketch, "E6.12.2.5", {"start": v(235.5, -18.02) * mm, "mid": v(234.76, -16.25) * mm, "end": v(233, -15.52) * mm});
            skLineSegment(sketch, "E6.12.3.0", {"start": v(208, 4.48) * mm, "end": v(233, 4.48) * mm});
            skArc(sketch, "E6.12.3.1", {"start": v(208, 4.48) * mm, "mid": v(206.23, 3.75) * mm, "end": v(205.5, 1.98) * mm});
            skArc(sketch, "E6.12.3.2", {"start": v(205.5, 1.98) * mm, "mid": v(206.23, 0.22) * mm, "end": v(208, -0.52) * mm});
            skLineSegment(sketch, "E6.12.3.3", {"start": v(208, -0.52) * mm, "end": v(233, -0.52) * mm});
            skArc(sketch, "E6.12.3.4", {"start": v(233, -0.52) * mm, "mid": v(234.76, 0.22) * mm, "end": v(235.5, 1.98) * mm});
            skArc(sketch, "E6.12.3.5", {"start": v(235.5, 1.98) * mm, "mid": v(234.76, 3.75) * mm, "end": v(233, 4.48) * mm});
            skLineSegment(sketch, "E6.12.4.0", {"start": v(208, 24.48) * mm, "end": v(233, 24.48) * mm});
            skArc(sketch, "E6.12.4.1", {"start": v(208, 24.48) * mm, "mid": v(206.23, 23.75) * mm, "end": v(205.5, 21.98) * mm});
            skArc(sketch, "E6.12.4.2", {"start": v(205.5, 21.98) * mm, "mid": v(206.23, 20.22) * mm, "end": v(208, 19.48) * mm});
            skLineSegment(sketch, "E6.12.4.3", {"start": v(208, 19.48) * mm, "end": v(233, 19.48) * mm});
            skArc(sketch, "E6.12.4.4", {"start": v(233, 19.48) * mm, "mid": v(234.76, 20.22) * mm, "end": v(235.5, 21.98) * mm});
            skArc(sketch, "E6.12.4.5", {"start": v(235.5, 21.98) * mm, "mid": v(234.76, 23.75) * mm, "end": v(233, 24.48) * mm});
            skLineSegment(sketch, "E6.12.5.0", {"start": v(208, 44.48) * mm, "end": v(233, 44.48) * mm});
            skArc(sketch, "E6.12.5.1", {"start": v(208, 44.48) * mm, "mid": v(206.23, 43.75) * mm, "end": v(205.5, 41.98) * mm});
            skArc(sketch, "E6.12.5.2", {"start": v(205.5, 41.98) * mm, "mid": v(206.23, 40.22) * mm, "end": v(208, 39.48) * mm});
            skLineSegment(sketch, "E6.12.5.3", {"start": v(208, 39.48) * mm, "end": v(233, 39.48) * mm});
            skArc(sketch, "E6.12.5.4", {"start": v(233, 39.48) * mm, "mid": v(234.76, 40.22) * mm, "end": v(235.5, 41.98) * mm});
            skArc(sketch, "E6.12.5.5", {"start": v(235.5, 41.98) * mm, "mid": v(234.76, 43.75) * mm, "end": v(233, 44.48) * mm});
            skLineSegment(sketch, "E6.12.6.0", {"start": v(208, 64.48) * mm, "end": v(233, 64.48) * mm});
            skArc(sketch, "E6.12.6.1", {"start": v(208, 64.48) * mm, "mid": v(206.23, 63.75) * mm, "end": v(205.5, 61.98) * mm});
            skArc(sketch, "E6.12.6.2", {"start": v(205.5, 61.98) * mm, "mid": v(206.23, 60.22) * mm, "end": v(208, 59.48) * mm});
            skLineSegment(sketch, "E6.12.6.3", {"start": v(208, 59.48) * mm, "end": v(233, 59.48) * mm});
            skArc(sketch, "E6.12.6.4", {"start": v(233, 59.48) * mm, "mid": v(234.76, 60.22) * mm, "end": v(235.5, 61.98) * mm});
            skArc(sketch, "E6.12.6.5", {"start": v(235.5, 61.98) * mm, "mid": v(234.76, 63.75) * mm, "end": v(233, 64.48) * mm});
            skLineSegment(sketch, "E6.13.0.0", {"start": v(243, -55.52) * mm, "end": v(268, -55.52) * mm});
            skArc(sketch, "E6.13.0.1", {"start": v(243, -55.52) * mm, "mid": v(241.23, -56.25) * mm, "end": v(240.5, -58.02) * mm});
            skArc(sketch, "E6.13.0.2", {"start": v(240.5, -58.02) * mm, "mid": v(241.23, -59.78) * mm, "end": v(243, -60.52) * mm});
            skLineSegment(sketch, "E6.13.0.3", {"start": v(243, -60.52) * mm, "end": v(268, -60.52) * mm});
            skArc(sketch, "E6.13.0.4", {"start": v(268, -60.52) * mm, "mid": v(269.76, -59.78) * mm, "end": v(270.5, -58.02) * mm});
            skArc(sketch, "E6.13.0.5", {"start": v(270.5, -58.02) * mm, "mid": v(269.76, -56.25) * mm, "end": v(268, -55.52) * mm});
            skLineSegment(sketch, "E6.13.1.0", {"start": v(243, -35.52) * mm, "end": v(268, -35.52) * mm});
            skArc(sketch, "E6.13.1.1", {"start": v(243, -35.52) * mm, "mid": v(241.23, -36.25) * mm, "end": v(240.5, -38.02) * mm});
            skArc(sketch, "E6.13.1.2", {"start": v(240.5, -38.02) * mm, "mid": v(241.23, -39.78) * mm, "end": v(243, -40.52) * mm});
            skLineSegment(sketch, "E6.13.1.3", {"start": v(243, -40.52) * mm, "end": v(268, -40.52) * mm});
            skArc(sketch, "E6.13.1.4", {"start": v(268, -40.52) * mm, "mid": v(269.76, -39.78) * mm, "end": v(270.5, -38.02) * mm});
            skArc(sketch, "E6.13.1.5", {"start": v(270.5, -38.02) * mm, "mid": v(269.76, -36.25) * mm, "end": v(268, -35.52) * mm});
            skLineSegment(sketch, "E6.13.2.0", {"start": v(243, -15.52) * mm, "end": v(268, -15.52) * mm});
            skArc(sketch, "E6.13.2.1", {"start": v(243, -15.52) * mm, "mid": v(241.23, -16.25) * mm, "end": v(240.5, -18.02) * mm});
            skArc(sketch, "E6.13.2.2", {"start": v(240.5, -18.02) * mm, "mid": v(241.23, -19.78) * mm, "end": v(243, -20.52) * mm});
            skLineSegment(sketch, "E6.13.2.3", {"start": v(243, -20.52) * mm, "end": v(268, -20.52) * mm});
            skArc(sketch, "E6.13.2.4", {"start": v(268, -20.52) * mm, "mid": v(269.76, -19.78) * mm, "end": v(270.5, -18.02) * mm});
            skArc(sketch, "E6.13.2.5", {"start": v(270.5, -18.02) * mm, "mid": v(269.76, -16.25) * mm, "end": v(268, -15.52) * mm});
            skLineSegment(sketch, "E6.13.3.0", {"start": v(243, 4.48) * mm, "end": v(268, 4.48) * mm});
            skArc(sketch, "E6.13.3.1", {"start": v(243, 4.48) * mm, "mid": v(241.23, 3.75) * mm, "end": v(240.5, 1.98) * mm});
            skArc(sketch, "E6.13.3.2", {"start": v(240.5, 1.98) * mm, "mid": v(241.23, 0.22) * mm, "end": v(243, -0.52) * mm});
            skLineSegment(sketch, "E6.13.3.3", {"start": v(243, -0.52) * mm, "end": v(268, -0.52) * mm});
            skArc(sketch, "E6.13.3.4", {"start": v(268, -0.52) * mm, "mid": v(269.76, 0.22) * mm, "end": v(270.5, 1.98) * mm});
            skArc(sketch, "E6.13.3.5", {"start": v(270.5, 1.98) * mm, "mid": v(269.76, 3.75) * mm, "end": v(268, 4.48) * mm});
            skLineSegment(sketch, "E6.13.4.0", {"start": v(243, 24.48) * mm, "end": v(268, 24.48) * mm});
            skArc(sketch, "E6.13.4.1", {"start": v(243, 24.48) * mm, "mid": v(241.23, 23.75) * mm, "end": v(240.5, 21.98) * mm});
            skArc(sketch, "E6.13.4.2", {"start": v(240.5, 21.98) * mm, "mid": v(241.23, 20.22) * mm, "end": v(243, 19.48) * mm});
            skLineSegment(sketch, "E6.13.4.3", {"start": v(243, 19.48) * mm, "end": v(268, 19.48) * mm});
            skArc(sketch, "E6.13.4.4", {"start": v(268, 19.48) * mm, "mid": v(269.76, 20.22) * mm, "end": v(270.5, 21.98) * mm});
            skArc(sketch, "E6.13.4.5", {"start": v(270.5, 21.98) * mm, "mid": v(269.76, 23.75) * mm, "end": v(268, 24.48) * mm});
            skLineSegment(sketch, "E6.13.5.0", {"start": v(243, 44.48) * mm, "end": v(268, 44.48) * mm});
            skArc(sketch, "E6.13.5.1", {"start": v(243, 44.48) * mm, "mid": v(241.23, 43.75) * mm, "end": v(240.5, 41.98) * mm});
            skArc(sketch, "E6.13.5.2", {"start": v(240.5, 41.98) * mm, "mid": v(241.23, 40.22) * mm, "end": v(243, 39.48) * mm});
            skLineSegment(sketch, "E6.13.5.3", {"start": v(243, 39.48) * mm, "end": v(268, 39.48) * mm});
            skArc(sketch, "E6.13.5.4", {"start": v(268, 39.48) * mm, "mid": v(269.76, 40.22) * mm, "end": v(270.5, 41.98) * mm});
            skArc(sketch, "E6.13.5.5", {"start": v(270.5, 41.98) * mm, "mid": v(269.76, 43.75) * mm, "end": v(268, 44.48) * mm});
            skLineSegment(sketch, "E6.13.6.0", {"start": v(243, 64.48) * mm, "end": v(268, 64.48) * mm});
            skArc(sketch, "E6.13.6.1", {"start": v(243, 64.48) * mm, "mid": v(241.23, 63.75) * mm, "end": v(240.5, 61.98) * mm});
            skArc(sketch, "E6.13.6.2", {"start": v(240.5, 61.98) * mm, "mid": v(241.23, 60.22) * mm, "end": v(243, 59.48) * mm});
            skLineSegment(sketch, "E6.13.6.3", {"start": v(243, 59.48) * mm, "end": v(268, 59.48) * mm});
            skArc(sketch, "E6.13.6.4", {"start": v(268, 59.48) * mm, "mid": v(269.76, 60.22) * mm, "end": v(270.5, 61.98) * mm});
            skArc(sketch, "E6.13.6.5", {"start": v(270.5, 61.98) * mm, "mid": v(269.76, 63.75) * mm, "end": v(268, 64.48) * mm});
            skLineSegment(sketch, "E6.14.0.0", {"start": v(278, -55.52) * mm, "end": v(303, -55.52) * mm});
            skArc(sketch, "E6.14.0.1", {"start": v(278, -55.52) * mm, "mid": v(276.23, -56.25) * mm, "end": v(275.5, -58.02) * mm});
            skArc(sketch, "E6.14.0.2", {"start": v(275.5, -58.02) * mm, "mid": v(276.23, -59.78) * mm, "end": v(278, -60.52) * mm});
            skLineSegment(sketch, "E6.14.0.3", {"start": v(278, -60.52) * mm, "end": v(303, -60.52) * mm});
            skArc(sketch, "E6.14.0.4", {"start": v(303, -60.52) * mm, "mid": v(304.76, -59.78) * mm, "end": v(305.5, -58.02) * mm});
            skArc(sketch, "E6.14.0.5", {"start": v(305.5, -58.02) * mm, "mid": v(304.76, -56.25) * mm, "end": v(303, -55.52) * mm});
            skLineSegment(sketch, "E6.14.1.0", {"start": v(278, -35.52) * mm, "end": v(303, -35.52) * mm});
            skArc(sketch, "E6.14.1.1", {"start": v(278, -35.52) * mm, "mid": v(276.23, -36.25) * mm, "end": v(275.5, -38.02) * mm});
            skArc(sketch, "E6.14.1.2", {"start": v(275.5, -38.02) * mm, "mid": v(276.23, -39.78) * mm, "end": v(278, -40.52) * mm});
            skLineSegment(sketch, "E6.14.1.3", {"start": v(278, -40.52) * mm, "end": v(303, -40.52) * mm});
            skArc(sketch, "E6.14.1.4", {"start": v(303, -40.52) * mm, "mid": v(304.76, -39.78) * mm, "end": v(305.5, -38.02) * mm});
            skArc(sketch, "E6.14.1.5", {"start": v(305.5, -38.02) * mm, "mid": v(304.76, -36.25) * mm, "end": v(303, -35.52) * mm});
            skLineSegment(sketch, "E6.14.2.0", {"start": v(278, -15.52) * mm, "end": v(303, -15.52) * mm});
            skArc(sketch, "E6.14.2.1", {"start": v(278, -15.52) * mm, "mid": v(276.23, -16.25) * mm, "end": v(275.5, -18.02) * mm});
            skArc(sketch, "E6.14.2.2", {"start": v(275.5, -18.02) * mm, "mid": v(276.23, -19.78) * mm, "end": v(278, -20.52) * mm});
            skLineSegment(sketch, "E6.14.2.3", {"start": v(278, -20.52) * mm, "end": v(303, -20.52) * mm});
            skArc(sketch, "E6.14.2.4", {"start": v(303, -20.52) * mm, "mid": v(304.76, -19.78) * mm, "end": v(305.5, -18.02) * mm});
            skArc(sketch, "E6.14.2.5", {"start": v(305.5, -18.02) * mm, "mid": v(304.76, -16.25) * mm, "end": v(303, -15.52) * mm});
            skLineSegment(sketch, "E6.14.3.0", {"start": v(278, 4.48) * mm, "end": v(303, 4.48) * mm});
            skArc(sketch, "E6.14.3.1", {"start": v(278, 4.48) * mm, "mid": v(276.23, 3.75) * mm, "end": v(275.5, 1.98) * mm});
            skArc(sketch, "E6.14.3.2", {"start": v(275.5, 1.98) * mm, "mid": v(276.23, 0.22) * mm, "end": v(278, -0.52) * mm});
            skLineSegment(sketch, "E6.14.3.3", {"start": v(278, -0.52) * mm, "end": v(303, -0.52) * mm});
            skArc(sketch, "E6.14.3.4", {"start": v(303, -0.52) * mm, "mid": v(304.76, 0.22) * mm, "end": v(305.5, 1.98) * mm});
            skArc(sketch, "E6.14.3.5", {"start": v(305.5, 1.98) * mm, "mid": v(304.76, 3.75) * mm, "end": v(303, 4.48) * mm});
            skLineSegment(sketch, "E6.14.4.0", {"start": v(278, 24.48) * mm, "end": v(303, 24.48) * mm});
            skArc(sketch, "E6.14.4.1", {"start": v(278, 24.48) * mm, "mid": v(276.23, 23.75) * mm, "end": v(275.5, 21.98) * mm});
            skArc(sketch, "E6.14.4.2", {"start": v(275.5, 21.98) * mm, "mid": v(276.23, 20.22) * mm, "end": v(278, 19.48) * mm});
            skLineSegment(sketch, "E6.14.4.3", {"start": v(278, 19.48) * mm, "end": v(303, 19.48) * mm});
            skArc(sketch, "E6.14.4.4", {"start": v(303, 19.48) * mm, "mid": v(304.76, 20.22) * mm, "end": v(305.5, 21.98) * mm});
            skArc(sketch, "E6.14.4.5", {"start": v(305.5, 21.98) * mm, "mid": v(304.76, 23.75) * mm, "end": v(303, 24.48) * mm});
            skLineSegment(sketch, "E6.14.5.0", {"start": v(278, 44.48) * mm, "end": v(303, 44.48) * mm});
            skArc(sketch, "E6.14.5.1", {"start": v(278, 44.48) * mm, "mid": v(276.23, 43.75) * mm, "end": v(275.5, 41.98) * mm});
            skArc(sketch, "E6.14.5.2", {"start": v(275.5, 41.98) * mm, "mid": v(276.23, 40.22) * mm, "end": v(278, 39.48) * mm});
            skLineSegment(sketch, "E6.14.5.3", {"start": v(278, 39.48) * mm, "end": v(303, 39.48) * mm});
            skArc(sketch, "E6.14.5.4", {"start": v(303, 39.48) * mm, "mid": v(304.76, 40.22) * mm, "end": v(305.5, 41.98) * mm});
            skArc(sketch, "E6.14.5.5", {"start": v(305.5, 41.98) * mm, "mid": v(304.76, 43.75) * mm, "end": v(303, 44.48) * mm});
            skLineSegment(sketch, "E6.14.6.0", {"start": v(278, 64.48) * mm, "end": v(303, 64.48) * mm});
            skArc(sketch, "E6.14.6.1", {"start": v(278, 64.48) * mm, "mid": v(276.23, 63.75) * mm, "end": v(275.5, 61.98) * mm});
            skArc(sketch, "E6.14.6.2", {"start": v(275.5, 61.98) * mm, "mid": v(276.23, 60.22) * mm, "end": v(278, 59.48) * mm});
            skLineSegment(sketch, "E6.14.6.3", {"start": v(278, 59.48) * mm, "end": v(303, 59.48) * mm});
            skArc(sketch, "E6.14.6.4", {"start": v(303, 59.48) * mm, "mid": v(304.76, 60.22) * mm, "end": v(305.5, 61.98) * mm});
            skArc(sketch, "E6.14.6.5", {"start": v(305.5, 61.98) * mm, "mid": v(304.76, 63.75) * mm, "end": v(303, 64.48) * mm});
            skLineSegment(sketch, "E6.direction1", {"start": v(-212, -55.52) * mm, "end": v(-177, -55.52) * mm, "construction": true});
            skLineSegment(sketch, "E6.direction2", {"start": v(-212, -55.52) * mm, "end": v(-212, -35.52) * mm, "construction": true});
            skSolve(sketch);
        }
        {
            var Q0;
            Q0=makeQuery(id+"F2.imprint","IMPRINT",FACE,{"disambiguationData":[TD([[makeQuery(id+"F2.imprint","IMPRINT",EDGE,{"derivedFrom":sQuery(id+"F2.wireOp",EDGE,"E6.0.5.0")}),-1.0]])]});
            var Q1;
            Q1=makeQuery(id+"F2.imprint","IMPRINT",FACE,{"disambiguationData":[TD([[makeQuery(id+"F2.imprint","IMPRINT",EDGE,{"derivedFrom":sQuery(id+"F2.wireOp",EDGE,"E6.0.6.0")}),-1.0]])]});
            var Q2;
            Q2=makeQuery(id+"F2.imprint","IMPRINT",FACE,{"disambiguationData":[TD([[makeQuery(id+"F2.imprint","IMPRINT",EDGE,{"derivedFrom":sQuery(id+"F2.wireOp",EDGE,"E6.1.0.0")}),-1.0]])]});
            var Q3;
            Q3=makeQuery(id+"F2.imprint","IMPRINT",FACE,{"disambiguationData":[TD([[makeQuery(id+"F2.imprint","IMPRINT",EDGE,{"derivedFrom":sQuery(id+"F2.wireOp",EDGE,"E6.1.2.0")}),-1.0]])]});
            var Q4;
            Q4=makeQuery(id+"F2.imprint","IMPRINT",FACE,{"disambiguationData":[TD([[makeQuery(id+"F2.imprint","IMPRINT",EDGE,{"derivedFrom":sQuery(id+"F2.wireOp",EDGE,"E6.1.4.0")}),-1.0]])]});
            var Q5;
            Q5=makeQuery(id+"F2.imprint","IMPRINT",FACE,{"disambiguationData":[TD([[makeQuery(id+"F2.imprint","IMPRINT",EDGE,{"derivedFrom":sQuery(id+"F2.wireOp",EDGE,"E6.1.3.0")}),-1.0]])]});
            var Q6;
            Q6=makeQuery(id+"F2.imprint","IMPRINT",FACE,{"disambiguationData":[TD([[makeQuery(id+"F2.imprint","IMPRINT",EDGE,{"derivedFrom":sQuery(id+"F2.wireOp",EDGE,"E6.1.5.0")}),-1.0]])]});
            var Q7;
            Q7=makeQuery(id+"F2.imprint","IMPRINT",FACE,{"disambiguationData":[TD([[makeQuery(id+"F2.imprint","IMPRINT",EDGE,{"derivedFrom":sQuery(id+"F2.wireOp",EDGE,"E6.0.4.0")}),-1.0]])]});
            var Q8;
            Q8=makeQuery(id+"F2.imprint","IMPRINT",FACE,{"disambiguationData":[TD([[makeQuery(id+"F2.imprint","IMPRINT",EDGE,{"derivedFrom":sQuery(id+"F2.wireOp",EDGE,"E6.0.3.0")}),-1.0]])]});
            var Q9;
            Q9=makeQuery(id+"F2.imprint","IMPRINT",FACE,{"disambiguationData":[TD([[makeQuery(id+"F2.imprint","IMPRINT",EDGE,{"derivedFrom":sQuery(id+"F2.wireOp",EDGE,"E6.0.2.0")}),-1.0]])]});
            var Q10;
            Q10=makeQuery(id+"F2.imprint","IMPRINT",FACE,{"disambiguationData":[TD([[makeQuery(id+"F2.imprint","IMPRINT",EDGE,{"derivedFrom":sQuery(id+"F2.wireOp",EDGE,"E6.0.1.0")}),-1.0]])]});
            var Q11;
            Q11=makeQuery(id+"F2.imprint","IMPRINT",FACE,{"disambiguationData":[TD([[makeQuery(id+"F2.imprint","IMPRINT",EDGE,{"derivedFrom":sQuery(id+"F2.wireOp",EDGE,"E1.bottom")}),-1.0]])]});
            var Q12;
            Q12=makeQuery(id+"F2.imprint","IMPRINT",FACE,{"disambiguationData":[TD([[makeQuery(id+"F2.imprint","IMPRINT",EDGE,{"derivedFrom":sQuery(id+"F2.wireOp",EDGE,"E6.2.0.0")}),-1.0]])]});
            var Q13;
            Q13=makeQuery(id+"F2.imprint","IMPRINT",FACE,{"disambiguationData":[TD([[makeQuery(id+"F2.imprint","IMPRINT",EDGE,{"derivedFrom":sQuery(id+"F2.wireOp",EDGE,"E6.1.6.0")}),-1.0]])]});
            var Q14;
            Q14=makeQuery(id+"F2.imprint","IMPRINT",FACE,{"disambiguationData":[TD([[makeQuery(id+"F2.imprint","IMPRINT",EDGE,{"derivedFrom":sQuery(id+"F2.wireOp",EDGE,"E6.2.1.0")}),-1.0]])]});
            var Q15;
            Q15=makeQuery(id+"F2.imprint","IMPRINT",FACE,{"disambiguationData":[TD([[makeQuery(id+"F2.imprint","IMPRINT",EDGE,{"derivedFrom":sQuery(id+"F2.wireOp",EDGE,"E6.1.1.0")}),-1.0]])]});
            var Q16;
            Q16=makeQuery(id+"F2.imprint","IMPRINT",FACE,{"disambiguationData":[TD([[makeQuery(id+"F2.imprint","IMPRINT",EDGE,{"derivedFrom":sQuery(id+"F2.wireOp",EDGE,"E6.13.1.0")}),-1.0]])]});
            var Q17;
            Q17=makeQuery(id+"F2.imprint","IMPRINT",FACE,{"disambiguationData":[TD([[makeQuery(id+"F2.imprint","IMPRINT",EDGE,{"derivedFrom":sQuery(id+"F2.wireOp",EDGE,"E6.4.0.0")}),-1.0]])]});
            var Q18;
            Q18=makeQuery(id+"F2.imprint","IMPRINT",FACE,{"disambiguationData":[TD([[makeQuery(id+"F2.imprint","IMPRINT",EDGE,{"derivedFrom":sQuery(id+"F2.wireOp",EDGE,"E6.6.2.0")}),-1.0]])]});
            var Q19;
            Q19=makeQuery(id+"F2.imprint","IMPRINT",FACE,{"disambiguationData":[TD([[makeQuery(id+"F2.imprint","IMPRINT",EDGE,{"derivedFrom":sQuery(id+"F2.wireOp",EDGE,"E6.8.4.0")}),-1.0]])]});
            var Q20;
            Q20=makeQuery(id+"F2.imprint","IMPRINT",FACE,{"disambiguationData":[TD([[makeQuery(id+"F2.imprint","IMPRINT",EDGE,{"derivedFrom":sQuery(id+"F2.wireOp",EDGE,"E6.10.6.0")}),-1.0]])]});
            var Q21;
            Q21=makeQuery(id+"F2.imprint","IMPRINT",FACE,{"disambiguationData":[TD([[makeQuery(id+"F2.imprint","IMPRINT",EDGE,{"derivedFrom":sQuery(id+"F2.wireOp",EDGE,"E6.13.0.0")}),-1.0]])]});
            var Q22;
            Q22=makeQuery(id+"F2.imprint","IMPRINT",FACE,{"disambiguationData":[TD([[makeQuery(id+"F2.imprint","IMPRINT",EDGE,{"derivedFrom":sQuery(id+"F2.wireOp",EDGE,"E6.3.6.0")}),-1.0]])]});
            var Q23;
            Q23=makeQuery(id+"F2.imprint","IMPRINT",FACE,{"disambiguationData":[TD([[makeQuery(id+"F2.imprint","IMPRINT",EDGE,{"derivedFrom":sQuery(id+"F2.wireOp",EDGE,"E6.6.1.0")}),-1.0]])]});
            var Q24;
            Q24=makeQuery(id+"F2.imprint","IMPRINT",FACE,{"disambiguationData":[TD([[makeQuery(id+"F2.imprint","IMPRINT",EDGE,{"derivedFrom":sQuery(id+"F2.wireOp",EDGE,"E6.8.3.0")}),-1.0]])]});
            var Q25;
            Q25=makeQuery(id+"F2.imprint","IMPRINT",FACE,{"disambiguationData":[TD([[makeQuery(id+"F2.imprint","IMPRINT",EDGE,{"derivedFrom":sQuery(id+"F2.wireOp",EDGE,"E6.10.5.0")}),-1.0]])]});
            var Q26;
            Q26=makeQuery(id+"F2.imprint","IMPRINT",FACE,{"disambiguationData":[TD([[makeQuery(id+"F2.imprint","IMPRINT",EDGE,{"derivedFrom":sQuery(id+"F2.wireOp",EDGE,"E6.12.6.0")}),-1.0]])]});
            var Q27;
            Q27=makeQuery(id+"F2.imprint","IMPRINT",FACE,{"disambiguationData":[TD([[makeQuery(id+"F2.imprint","IMPRINT",EDGE,{"derivedFrom":sQuery(id+"F2.wireOp",EDGE,"E6.3.5.0")}),-1.0]])]});
            var Q28;
            Q28=makeQuery(id+"F2.imprint","IMPRINT",FACE,{"disambiguationData":[TD([[makeQuery(id+"F2.imprint","IMPRINT",EDGE,{"derivedFrom":sQuery(id+"F2.wireOp",EDGE,"E6.6.0.0")}),-1.0]])]});
            var Q29;
            Q29=makeQuery(id+"F2.imprint","IMPRINT",FACE,{"disambiguationData":[TD([[makeQuery(id+"F2.imprint","IMPRINT",EDGE,{"derivedFrom":sQuery(id+"F2.wireOp",EDGE,"E6.8.2.0")}),-1.0]])]});
            var Q30;
            Q30=makeQuery(id+"F2.imprint","IMPRINT",FACE,{"disambiguationData":[TD([[makeQuery(id+"F2.imprint","IMPRINT",EDGE,{"derivedFrom":sQuery(id+"F2.wireOp",EDGE,"E6.10.4.0")}),-1.0]])]});
            var Q31;
            Q31=makeQuery(id+"F2.imprint","IMPRINT",FACE,{"disambiguationData":[TD([[makeQuery(id+"F2.imprint","IMPRINT",EDGE,{"derivedFrom":sQuery(id+"F2.wireOp",EDGE,"E6.12.5.0")}),-1.0]])]});
            var Q32;
            Q32=makeQuery(id+"F2.imprint","IMPRINT",FACE,{"disambiguationData":[TD([[makeQuery(id+"F2.imprint","IMPRINT",EDGE,{"derivedFrom":sQuery(id+"F2.wireOp",EDGE,"E6.3.4.0")}),-1.0]])]});
            var Q33;
            Q33=makeQuery(id+"F2.imprint","IMPRINT",FACE,{"disambiguationData":[TD([[makeQuery(id+"F2.imprint","IMPRINT",EDGE,{"derivedFrom":sQuery(id+"F2.wireOp",EDGE,"E6.5.6.0")}),-1.0]])]});
            var Q34;
            Q34=makeQuery(id+"F2.imprint","IMPRINT",FACE,{"disambiguationData":[TD([[makeQuery(id+"F2.imprint","IMPRINT",EDGE,{"derivedFrom":sQuery(id+"F2.wireOp",EDGE,"E6.8.1.0")}),-1.0]])]});
            var Q35;
            Q35=makeQuery(id+"F2.imprint","IMPRINT",FACE,{"disambiguationData":[TD([[makeQuery(id+"F2.imprint","IMPRINT",EDGE,{"derivedFrom":sQuery(id+"F2.wireOp",EDGE,"E6.10.3.0")}),-1.0]])]});
            var Q36;
            Q36=makeQuery(id+"F2.imprint","IMPRINT",FACE,{"disambiguationData":[TD([[makeQuery(id+"F2.imprint","IMPRINT",EDGE,{"derivedFrom":sQuery(id+"F2.wireOp",EDGE,"E6.12.4.0")}),-1.0]])]});
            var Q37;
            Q37=makeQuery(id+"F2.imprint","IMPRINT",FACE,{"disambiguationData":[TD([[makeQuery(id+"F2.imprint","IMPRINT",EDGE,{"derivedFrom":sQuery(id+"F2.wireOp",EDGE,"E6.14.6.0")}),-1.0]])]});
            var Q38;
            Q38=makeQuery(id+"F2.imprint","IMPRINT",FACE,{"disambiguationData":[TD([[makeQuery(id+"F2.imprint","IMPRINT",EDGE,{"derivedFrom":sQuery(id+"F2.wireOp",EDGE,"E6.3.3.0")}),-1.0]])]});
            var Q39;
            Q39=makeQuery(id+"F2.imprint","IMPRINT",FACE,{"disambiguationData":[TD([[makeQuery(id+"F2.imprint","IMPRINT",EDGE,{"derivedFrom":sQuery(id+"F2.wireOp",EDGE,"E6.5.5.0")}),-1.0]])]});
            var Q40;
            Q40=makeQuery(id+"F2.imprint","IMPRINT",FACE,{"disambiguationData":[TD([[makeQuery(id+"F2.imprint","IMPRINT",EDGE,{"derivedFrom":sQuery(id+"F2.wireOp",EDGE,"E6.8.0.0")}),-1.0]])]});
            var Q41;
            Q41=makeQuery(id+"F2.imprint","IMPRINT",FACE,{"disambiguationData":[TD([[makeQuery(id+"F2.imprint","IMPRINT",EDGE,{"derivedFrom":sQuery(id+"F2.wireOp",EDGE,"E6.10.2.0")}),-1.0]])]});
            var Q42;
            Q42=makeQuery(id+"F2.imprint","IMPRINT",FACE,{"disambiguationData":[TD([[makeQuery(id+"F2.imprint","IMPRINT",EDGE,{"derivedFrom":sQuery(id+"F2.wireOp",EDGE,"E6.3.2.0")}),-1.0]])]});
            var Q43;
            Q43=makeQuery(id+"F2.imprint","IMPRINT",FACE,{"disambiguationData":[TD([[makeQuery(id+"F2.imprint","IMPRINT",EDGE,{"derivedFrom":sQuery(id+"F2.wireOp",EDGE,"E6.5.4.0")}),-1.0]])]});
            var Q44;
            Q44=makeQuery(id+"F2.imprint","IMPRINT",FACE,{"disambiguationData":[TD([[makeQuery(id+"F2.imprint","IMPRINT",EDGE,{"derivedFrom":sQuery(id+"F2.wireOp",EDGE,"E6.7.6.0")}),-1.0]])]});
            var Q45;
            Q45=makeQuery(id+"F2.imprint","IMPRINT",FACE,{"disambiguationData":[TD([[makeQuery(id+"F2.imprint","IMPRINT",EDGE,{"derivedFrom":sQuery(id+"F2.wireOp",EDGE,"E6.10.1.0")}),-1.0]])]});
            var Q46;
            Q46=makeQuery(id+"F2.imprint","IMPRINT",FACE,{"disambiguationData":[TD([[makeQuery(id+"F2.imprint","IMPRINT",EDGE,{"derivedFrom":sQuery(id+"F2.wireOp",EDGE,"E6.12.3.0")}),-1.0]])]});
            var Q47;
            Q47=makeQuery(id+"F2.imprint","IMPRINT",FACE,{"disambiguationData":[TD([[makeQuery(id+"F2.imprint","IMPRINT",EDGE,{"derivedFrom":sQuery(id+"F2.wireOp",EDGE,"E6.14.5.0")}),-1.0]])]});
            var Q48;
            Q48=makeQuery(id+"F2.imprint","IMPRINT",FACE,{"disambiguationData":[TD([[makeQuery(id+"F2.imprint","IMPRINT",EDGE,{"derivedFrom":sQuery(id+"F2.wireOp",EDGE,"E6.12.2.0")}),-1.0]])]});
            var Q49;
            Q49=makeQuery(id+"F2.imprint","IMPRINT",FACE,{"disambiguationData":[TD([[makeQuery(id+"F2.imprint","IMPRINT",EDGE,{"derivedFrom":sQuery(id+"F2.wireOp",EDGE,"E6.14.4.0")}),-1.0]])]});
            var Q50;
            Q50=makeQuery(id+"F2.imprint","IMPRINT",FACE,{"disambiguationData":[TD([[makeQuery(id+"F2.imprint","IMPRINT",EDGE,{"derivedFrom":sQuery(id+"F2.wireOp",EDGE,"E6.3.1.0")}),-1.0]])]});
            var Q51;
            Q51=makeQuery(id+"F2.imprint","IMPRINT",FACE,{"disambiguationData":[TD([[makeQuery(id+"F2.imprint","IMPRINT",EDGE,{"derivedFrom":sQuery(id+"F2.wireOp",EDGE,"E6.5.3.0")}),-1.0]])]});
            var Q52;
            Q52=makeQuery(id+"F2.imprint","IMPRINT",FACE,{"disambiguationData":[TD([[makeQuery(id+"F2.imprint","IMPRINT",EDGE,{"derivedFrom":sQuery(id+"F2.wireOp",EDGE,"E6.7.5.0")}),-1.0]])]});
            var Q53;
            Q53=makeQuery(id+"F2.imprint","IMPRINT",FACE,{"disambiguationData":[TD([[makeQuery(id+"F2.imprint","IMPRINT",EDGE,{"derivedFrom":sQuery(id+"F2.wireOp",EDGE,"E6.10.0.0")}),-1.0]])]});
            var Q54;
            Q54=makeQuery(id+"F2.imprint","IMPRINT",FACE,{"disambiguationData":[TD([[makeQuery(id+"F2.imprint","IMPRINT",EDGE,{"derivedFrom":sQuery(id+"F2.wireOp",EDGE,"E6.7.4.0")}),-1.0]])]});
            var Q55;
            Q55=makeQuery(id+"F2.imprint","IMPRINT",FACE,{"disambiguationData":[TD([[makeQuery(id+"F2.imprint","IMPRINT",EDGE,{"derivedFrom":sQuery(id+"F2.wireOp",EDGE,"E6.9.6.0")}),-1.0]])]});
            var Q56;
            Q56=makeQuery(id+"F2.imprint","IMPRINT",FACE,{"disambiguationData":[TD([[makeQuery(id+"F2.imprint","IMPRINT",EDGE,{"derivedFrom":sQuery(id+"F2.wireOp",EDGE,"E6.12.1.0")}),-1.0]])]});
            var Q57;
            Q57=makeQuery(id+"F2.imprint","IMPRINT",FACE,{"disambiguationData":[TD([[makeQuery(id+"F2.imprint","IMPRINT",EDGE,{"derivedFrom":sQuery(id+"F2.wireOp",EDGE,"E6.14.3.0")}),-1.0]])]});
            var Q58;
            Q58=makeQuery(id+"F2.imprint","IMPRINT",FACE,{"disambiguationData":[TD([[makeQuery(id+"F2.imprint","IMPRINT",EDGE,{"derivedFrom":sQuery(id+"F2.wireOp",EDGE,"E6.3.0.0")}),-1.0]])]});
            var Q59;
            Q59=makeQuery(id+"F2.imprint","IMPRINT",FACE,{"disambiguationData":[TD([[makeQuery(id+"F2.imprint","IMPRINT",EDGE,{"derivedFrom":sQuery(id+"F2.wireOp",EDGE,"E6.5.2.0")}),-1.0]])]});
            var Q60;
            Q60=makeQuery(id+"F2.imprint","IMPRINT",FACE,{"disambiguationData":[TD([[makeQuery(id+"F2.imprint","IMPRINT",EDGE,{"derivedFrom":sQuery(id+"F2.wireOp",EDGE,"E6.7.3.0")}),-1.0]])]});
            var Q61;
            Q61=makeQuery(id+"F2.imprint","IMPRINT",FACE,{"disambiguationData":[TD([[makeQuery(id+"F2.imprint","IMPRINT",EDGE,{"derivedFrom":sQuery(id+"F2.wireOp",EDGE,"E6.9.5.0")}),-1.0]])]});
            var Q62;
            Q62=makeQuery(id+"F2.imprint","IMPRINT",FACE,{"disambiguationData":[TD([[makeQuery(id+"F2.imprint","IMPRINT",EDGE,{"derivedFrom":sQuery(id+"F2.wireOp",EDGE,"E6.12.0.0")}),-1.0]])]});
            var Q63;
            Q63=makeQuery(id+"F2.imprint","IMPRINT",FACE,{"disambiguationData":[TD([[makeQuery(id+"F2.imprint","IMPRINT",EDGE,{"derivedFrom":sQuery(id+"F2.wireOp",EDGE,"E6.14.2.0")}),-1.0]])]});
            var Q64;
            Q64=makeQuery(id+"F2.imprint","IMPRINT",FACE,{"disambiguationData":[TD([[makeQuery(id+"F2.imprint","IMPRINT",EDGE,{"derivedFrom":sQuery(id+"F2.wireOp",EDGE,"E6.2.6.0")}),-1.0]])]});
            var Q65;
            Q65=makeQuery(id+"F2.imprint","IMPRINT",FACE,{"disambiguationData":[TD([[makeQuery(id+"F2.imprint","IMPRINT",EDGE,{"derivedFrom":sQuery(id+"F2.wireOp",EDGE,"E6.5.1.0")}),-1.0]])]});
            var Q66;
            Q66=makeQuery(id+"F2.imprint","IMPRINT",FACE,{"disambiguationData":[TD([[makeQuery(id+"F2.imprint","IMPRINT",EDGE,{"derivedFrom":sQuery(id+"F2.wireOp",EDGE,"E6.7.2.0")}),-1.0]])]});
            var Q67;
            Q67=makeQuery(id+"F2.imprint","IMPRINT",FACE,{"disambiguationData":[TD([[makeQuery(id+"F2.imprint","IMPRINT",EDGE,{"derivedFrom":sQuery(id+"F2.wireOp",EDGE,"E6.9.4.0")}),-1.0]])]});
            var Q68;
            Q68=makeQuery(id+"F2.imprint","IMPRINT",FACE,{"disambiguationData":[TD([[makeQuery(id+"F2.imprint","IMPRINT",EDGE,{"derivedFrom":sQuery(id+"F2.wireOp",EDGE,"E6.11.6.0")}),-1.0]])]});
            var Q69;
            Q69=makeQuery(id+"F2.imprint","IMPRINT",FACE,{"disambiguationData":[TD([[makeQuery(id+"F2.imprint","IMPRINT",EDGE,{"derivedFrom":sQuery(id+"F2.wireOp",EDGE,"E6.14.1.0")}),-1.0]])]});
            var Q70;
            Q70=makeQuery(id+"F2.imprint","IMPRINT",FACE,{"disambiguationData":[TD([[makeQuery(id+"F2.imprint","IMPRINT",EDGE,{"derivedFrom":sQuery(id+"F2.wireOp",EDGE,"E6.2.5.0")}),-1.0]])]});
            var Q71;
            Q71=makeQuery(id+"F2.imprint","IMPRINT",FACE,{"disambiguationData":[TD([[makeQuery(id+"F2.imprint","IMPRINT",EDGE,{"derivedFrom":sQuery(id+"F2.wireOp",EDGE,"E6.5.0.0")}),-1.0]])]});
            var Q72;
            Q72=makeQuery(id+"F2.imprint","IMPRINT",FACE,{"disambiguationData":[TD([[makeQuery(id+"F2.imprint","IMPRINT",EDGE,{"derivedFrom":sQuery(id+"F2.wireOp",EDGE,"E6.7.1.0")}),-1.0]])]});
            var Q73;
            Q73=makeQuery(id+"F2.imprint","IMPRINT",FACE,{"disambiguationData":[TD([[makeQuery(id+"F2.imprint","IMPRINT",EDGE,{"derivedFrom":sQuery(id+"F2.wireOp",EDGE,"E6.9.3.0")}),-1.0]])]});
            var Q74;
            Q74=makeQuery(id+"F2.imprint","IMPRINT",FACE,{"disambiguationData":[TD([[makeQuery(id+"F2.imprint","IMPRINT",EDGE,{"derivedFrom":sQuery(id+"F2.wireOp",EDGE,"E6.11.5.0")}),-1.0]])]});
            var Q75;
            Q75=makeQuery(id+"F2.imprint","IMPRINT",FACE,{"disambiguationData":[TD([[makeQuery(id+"F2.imprint","IMPRINT",EDGE,{"derivedFrom":sQuery(id+"F2.wireOp",EDGE,"E6.14.0.0")}),-1.0]])]});
            var Q76;
            Q76=makeQuery(id+"F2.imprint","IMPRINT",FACE,{"disambiguationData":[TD([[makeQuery(id+"F2.imprint","IMPRINT",EDGE,{"derivedFrom":sQuery(id+"F2.wireOp",EDGE,"E6.2.4.0")}),-1.0]])]});
            var Q77;
            Q77=makeQuery(id+"F2.imprint","IMPRINT",FACE,{"disambiguationData":[TD([[makeQuery(id+"F2.imprint","IMPRINT",EDGE,{"derivedFrom":sQuery(id+"F2.wireOp",EDGE,"E6.4.6.0")}),-1.0]])]});
            var Q78;
            Q78=makeQuery(id+"F2.imprint","IMPRINT",FACE,{"disambiguationData":[TD([[makeQuery(id+"F2.imprint","IMPRINT",EDGE,{"derivedFrom":sQuery(id+"F2.wireOp",EDGE,"E6.7.0.0")}),-1.0]])]});
            var Q79;
            Q79=makeQuery(id+"F2.imprint","IMPRINT",FACE,{"disambiguationData":[TD([[makeQuery(id+"F2.imprint","IMPRINT",EDGE,{"derivedFrom":sQuery(id+"F2.wireOp",EDGE,"E6.9.2.0")}),-1.0]])]});
            var Q80;
            Q80=makeQuery(id+"F2.imprint","IMPRINT",FACE,{"disambiguationData":[TD([[makeQuery(id+"F2.imprint","IMPRINT",EDGE,{"derivedFrom":sQuery(id+"F2.wireOp",EDGE,"E6.11.4.0")}),-1.0]])]});
            var Q81;
            Q81=makeQuery(id+"F2.imprint","IMPRINT",FACE,{"disambiguationData":[TD([[makeQuery(id+"F2.imprint","IMPRINT",EDGE,{"derivedFrom":sQuery(id+"F2.wireOp",EDGE,"E6.13.6.0")}),-1.0]])]});
            var Q82;
            Q82=makeQuery(id+"F2.imprint","IMPRINT",FACE,{"disambiguationData":[TD([[makeQuery(id+"F2.imprint","IMPRINT",EDGE,{"derivedFrom":sQuery(id+"F2.wireOp",EDGE,"E6.2.3.0")}),-1.0]])]});
            var Q83;
            Q83=makeQuery(id+"F2.imprint","IMPRINT",FACE,{"disambiguationData":[TD([[makeQuery(id+"F2.imprint","IMPRINT",EDGE,{"derivedFrom":sQuery(id+"F2.wireOp",EDGE,"E6.4.5.0")}),-1.0]])]});
            var Q84;
            Q84=makeQuery(id+"F2.imprint","IMPRINT",FACE,{"disambiguationData":[TD([[makeQuery(id+"F2.imprint","IMPRINT",EDGE,{"derivedFrom":sQuery(id+"F2.wireOp",EDGE,"E6.6.6.0")}),-1.0]])]});
            var Q85;
            Q85=makeQuery(id+"F2.imprint","IMPRINT",FACE,{"disambiguationData":[TD([[makeQuery(id+"F2.imprint","IMPRINT",EDGE,{"derivedFrom":sQuery(id+"F2.wireOp",EDGE,"E6.11.3.0")}),-1.0]])]});
            var Q86;
            Q86=makeQuery(id+"F2.imprint","IMPRINT",FACE,{"disambiguationData":[TD([[makeQuery(id+"F2.imprint","IMPRINT",EDGE,{"derivedFrom":sQuery(id+"F2.wireOp",EDGE,"E6.9.1.0")}),-1.0]])]});
            var Q87;
            Q87=makeQuery(id+"F2.imprint","IMPRINT",FACE,{"disambiguationData":[TD([[makeQuery(id+"F2.imprint","IMPRINT",EDGE,{"derivedFrom":sQuery(id+"F2.wireOp",EDGE,"E6.13.5.0")}),-1.0]])]});
            var Q88;
            Q88=makeQuery(id+"F2.imprint","IMPRINT",FACE,{"disambiguationData":[TD([[makeQuery(id+"F2.imprint","IMPRINT",EDGE,{"derivedFrom":sQuery(id+"F2.wireOp",EDGE,"E6.2.2.0")}),-1.0]])]});
            var Q89;
            Q89=makeQuery(id+"F2.imprint","IMPRINT",FACE,{"disambiguationData":[TD([[makeQuery(id+"F2.imprint","IMPRINT",EDGE,{"derivedFrom":sQuery(id+"F2.wireOp",EDGE,"E6.4.4.0")}),-1.0]])]});
            var Q90;
            Q90=makeQuery(id+"F2.imprint","IMPRINT",FACE,{"disambiguationData":[TD([[makeQuery(id+"F2.imprint","IMPRINT",EDGE,{"derivedFrom":sQuery(id+"F2.wireOp",EDGE,"E6.6.4.0")}),-1.0]])]});
            var Q91;
            Q91=makeQuery(id+"F2.imprint","IMPRINT",FACE,{"disambiguationData":[TD([[makeQuery(id+"F2.imprint","IMPRINT",EDGE,{"derivedFrom":sQuery(id+"F2.wireOp",EDGE,"E6.8.6.0")}),-1.0]])]});
            var Q92;
            Q92=makeQuery(id+"F2.imprint","IMPRINT",FACE,{"disambiguationData":[TD([[makeQuery(id+"F2.imprint","IMPRINT",EDGE,{"derivedFrom":sQuery(id+"F2.wireOp",EDGE,"E6.11.1.0")}),-1.0]])]});
            var Q93;
            Q93=makeQuery(id+"F2.imprint","IMPRINT",FACE,{"disambiguationData":[TD([[makeQuery(id+"F2.imprint","IMPRINT",EDGE,{"derivedFrom":sQuery(id+"F2.wireOp",EDGE,"E6.13.3.0")}),-1.0]])]});
            var Q94;
            Q94=makeQuery(id+"F2.imprint","IMPRINT",FACE,{"disambiguationData":[TD([[makeQuery(id+"F2.imprint","IMPRINT",EDGE,{"derivedFrom":sQuery(id+"F2.wireOp",EDGE,"E6.4.2.0")}),-1.0]])]});
            var Q95;
            Q95=makeQuery(id+"F2.imprint","IMPRINT",FACE,{"disambiguationData":[TD([[makeQuery(id+"F2.imprint","IMPRINT",EDGE,{"derivedFrom":sQuery(id+"F2.wireOp",EDGE,"E6.6.3.0")}),-1.0]])]});
            var Q96;
            Q96=makeQuery(id+"F2.imprint","IMPRINT",FACE,{"disambiguationData":[TD([[makeQuery(id+"F2.imprint","IMPRINT",EDGE,{"derivedFrom":sQuery(id+"F2.wireOp",EDGE,"E6.8.5.0")}),-1.0]])]});
            var Q97;
            Q97=makeQuery(id+"F2.imprint","IMPRINT",FACE,{"disambiguationData":[TD([[makeQuery(id+"F2.imprint","IMPRINT",EDGE,{"derivedFrom":sQuery(id+"F2.wireOp",EDGE,"E6.11.0.0")}),-1.0]])]});
            var Q98;
            Q98=makeQuery(id+"F2.imprint","IMPRINT",FACE,{"disambiguationData":[TD([[makeQuery(id+"F2.imprint","IMPRINT",EDGE,{"derivedFrom":sQuery(id+"F2.wireOp",EDGE,"E6.13.2.0")}),-1.0]])]});
            var Q99;
            Q99=makeQuery(id+"F2.imprint","IMPRINT",FACE,{"disambiguationData":[TD([[makeQuery(id+"F2.imprint","IMPRINT",EDGE,{"derivedFrom":sQuery(id+"F2.wireOp",EDGE,"E6.4.1.0")}),-1.0]])]});
            var Q100;
            Q100=makeQuery(id+"F2.imprint","IMPRINT",FACE,{"disambiguationData":[TD([[makeQuery(id+"F2.imprint","IMPRINT",EDGE,{"derivedFrom":sQuery(id+"F2.wireOp",EDGE,"E6.9.0.0")}),-1.0]])]});
            var Q101;
            Q101=makeQuery(id+"F2.imprint","IMPRINT",FACE,{"disambiguationData":[TD([[makeQuery(id+"F2.imprint","IMPRINT",EDGE,{"derivedFrom":sQuery(id+"F2.wireOp",EDGE,"E6.11.2.0")}),-1.0]])]});
            var Q102;
            Q102=makeQuery(id+"F2.imprint","IMPRINT",FACE,{"disambiguationData":[TD([[makeQuery(id+"F2.imprint","IMPRINT",EDGE,{"derivedFrom":sQuery(id+"F2.wireOp",EDGE,"E6.13.4.0")}),-1.0]])]});
            var Q103;
            Q103=makeQuery(id+"F2.imprint","IMPRINT",FACE,{"disambiguationData":[TD([[makeQuery(id+"F2.imprint","IMPRINT",EDGE,{"derivedFrom":sQuery(id+"F2.wireOp",EDGE,"E6.4.3.0")}),-1.0]])]});
            var Q104;
            Q104=makeQuery(id+"F2.imprint","IMPRINT",FACE,{"disambiguationData":[TD([[makeQuery(id+"F2.imprint","IMPRINT",EDGE,{"derivedFrom":sQuery(id+"F2.wireOp",EDGE,"E6.6.5.0")}),-1.0]])]});
            extrude(context, id + "F3", {"entities" : qUnion([Q0, Q1, Q2, Q3, Q4, Q5, Q6, Q7, Q8, Q9, Q10, Q11, Q12, Q13, Q14, Q15, Q16, Q17, Q18, Q19, Q20, Q21, Q22, Q23, Q24, Q25, Q26, Q27, Q28, Q29, Q30, Q31, Q32, Q33, Q34, Q35, Q36, Q37, Q38, Q39, Q40, Q41, Q42, Q43, Q44, Q45, Q46, Q47, Q48, Q49, Q50, Q51, Q52, Q53, Q54, Q55, Q56, Q57, Q58, Q59, Q60, Q61, Q62, Q63, Q64, Q65, Q66, Q67, Q68, Q69, Q70, Q71, Q72, Q73, Q74, Q75, Q76, Q77, Q78, Q79, Q80, Q81, Q82, Q83, Q84, Q85, Q86, Q87, Q88, Q89, Q90, Q91, Q92, Q93, Q94, Q95, Q96, Q97, Q98, Q99, Q100, Q101, Q102, Q103, Q104]), "operationType" : NewBodyOperationType.REMOVE, "oppositeDirection" : true, "depth" : 0.5 * mm, "offsetDistance" : 25 * mm});
        }
        {
            var Q0;
            Q0=makeQuery(id+"F1.opExtrude","CAP_FACE",FACE,{"disambiguationData":[OSD([sQuery(id+"F0.wireOp",EDGE,"E0.bottom"),sQuery(id+"F0.wireOp",EDGE,"E0.top"),sQuery(id+"F0.wireOp",EDGE,"E0.left"),sQuery(id+"F0.wireOp",EDGE,"E0.right")])],"isStart":false});
            var sketch = newSketch(context, id + "F4", { "sketchPlane" : qUnion([Q0])});
            skLineSegment(sketch, "E7.bottom", {"start": v(-194.5, -45.52) * mm, "end": v(-169.5, -45.52) * mm});
            skLineSegment(sketch, "E7.top", {"start": v(-194.5, -50.52) * mm, "end": v(-169.5, -50.52) * mm});
            skLineSegment(sketch, "E7.left", {"start": v(-197, -48.02) * mm, "end": v(-197, -48.02) * mm});
            skLineSegment(sketch, "E7.right", {"start": v(-167, -48.02) * mm, "end": v(-167, -48.02) * mm});
            skPoint(sketch, "E8.visualSharp", {"position": v(-197, -45.52) * mm});
            skArc(sketch, "E8.filletArc", {"start": v(-194.5, -45.52) * mm, "mid": v(-196.27, -46.25) * mm, "end": v(-197, -48.02) * mm});
            skPoint(sketch, "E9.visualSharp", {"position": v(-167, -45.52) * mm});
            skArc(sketch, "E9.filletArc", {"start": v(-167, -48.02) * mm, "mid": v(-167.74, -46.25) * mm, "end": v(-169.5, -45.52) * mm});
            skPoint(sketch, "E10.visualSharp", {"position": v(-167, -50.52) * mm});
            skArc(sketch, "E10.filletArc", {"start": v(-169.5, -50.52) * mm, "mid": v(-167.74, -49.78) * mm, "end": v(-167, -48.02) * mm});
            skPoint(sketch, "E11.visualSharp", {"position": v(-197, -50.52) * mm});
            skArc(sketch, "E11.filletArc", {"start": v(-197, -48.02) * mm, "mid": v(-196.27, -49.78) * mm, "end": v(-194.5, -50.52) * mm});
            skLineSegment(sketch, "E12.0.1.0", {"start": v(-194.5, -30.52) * mm, "end": v(-169.5, -30.52) * mm});
            skPoint(sketch, "E12.0.1.1", {"position": v(-197, -30.52) * mm});
            skPoint(sketch, "E12.0.1.2", {"position": v(-197, -25.52) * mm});
            skLineSegment(sketch, "E12.0.1.3", {"start": v(-194.5, -25.52) * mm, "end": v(-169.5, -25.52) * mm});
            skPoint(sketch, "E12.0.1.4", {"position": v(-167, -25.52) * mm});
            skPoint(sketch, "E12.0.1.5", {"position": v(-167, -30.52) * mm});
            skArc(sketch, "E12.0.1.6", {"start": v(-197, -28.02) * mm, "mid": v(-196.27, -29.78) * mm, "end": v(-194.5, -30.52) * mm});
            skArc(sketch, "E12.0.1.7", {"start": v(-169.5, -30.52) * mm, "mid": v(-167.74, -29.78) * mm, "end": v(-167, -28.02) * mm});
            skArc(sketch, "E12.0.1.8", {"start": v(-194.5, -25.52) * mm, "mid": v(-196.27, -26.25) * mm, "end": v(-197, -28.02) * mm});
            skArc(sketch, "E12.0.1.9", {"start": v(-167, -28.02) * mm, "mid": v(-167.74, -26.25) * mm, "end": v(-169.5, -25.52) * mm});
            skLineSegment(sketch, "E12.0.2.0", {"start": v(-194.5, -10.52) * mm, "end": v(-169.5, -10.52) * mm});
            skPoint(sketch, "E12.0.2.1", {"position": v(-197, -10.52) * mm});
            skPoint(sketch, "E12.0.2.2", {"position": v(-197, -5.52) * mm});
            skLineSegment(sketch, "E12.0.2.3", {"start": v(-194.5, -5.52) * mm, "end": v(-169.5, -5.52) * mm});
            skPoint(sketch, "E12.0.2.4", {"position": v(-167, -5.52) * mm});
            skPoint(sketch, "E12.0.2.5", {"position": v(-167, -10.52) * mm});
            skArc(sketch, "E12.0.2.6", {"start": v(-197, -8.02) * mm, "mid": v(-196.27, -9.78) * mm, "end": v(-194.5, -10.52) * mm});
            skArc(sketch, "E12.0.2.7", {"start": v(-169.5, -10.52) * mm, "mid": v(-167.74, -9.78) * mm, "end": v(-167, -8.02) * mm});
            skArc(sketch, "E12.0.2.8", {"start": v(-194.5, -5.52) * mm, "mid": v(-196.27, -6.25) * mm, "end": v(-197, -8.02) * mm});
            skArc(sketch, "E12.0.2.9", {"start": v(-167, -8.02) * mm, "mid": v(-167.74, -6.25) * mm, "end": v(-169.5, -5.52) * mm});
            skLineSegment(sketch, "E12.0.3.0", {"start": v(-194.5, 9.48) * mm, "end": v(-169.5, 9.48) * mm});
            skPoint(sketch, "E12.0.3.1", {"position": v(-197, 9.48) * mm});
            skPoint(sketch, "E12.0.3.2", {"position": v(-197, 14.48) * mm});
            skLineSegment(sketch, "E12.0.3.3", {"start": v(-194.5, 14.48) * mm, "end": v(-169.5, 14.48) * mm});
            skPoint(sketch, "E12.0.3.4", {"position": v(-167, 14.48) * mm});
            skPoint(sketch, "E12.0.3.5", {"position": v(-167, 9.48) * mm});
            skArc(sketch, "E12.0.3.6", {"start": v(-197, 11.98) * mm, "mid": v(-196.27, 10.22) * mm, "end": v(-194.5, 9.48) * mm});
            skArc(sketch, "E12.0.3.7", {"start": v(-169.5, 9.48) * mm, "mid": v(-167.74, 10.22) * mm, "end": v(-167, 11.98) * mm});
            skArc(sketch, "E12.0.3.8", {"start": v(-194.5, 14.48) * mm, "mid": v(-196.27, 13.75) * mm, "end": v(-197, 11.98) * mm});
            skArc(sketch, "E12.0.3.9", {"start": v(-167, 11.98) * mm, "mid": v(-167.74, 13.75) * mm, "end": v(-169.5, 14.48) * mm});
            skLineSegment(sketch, "E12.0.4.0", {"start": v(-194.5, 29.48) * mm, "end": v(-169.5, 29.48) * mm});
            skPoint(sketch, "E12.0.4.1", {"position": v(-197, 29.48) * mm});
            skPoint(sketch, "E12.0.4.2", {"position": v(-197, 34.48) * mm});
            skLineSegment(sketch, "E12.0.4.3", {"start": v(-194.5, 34.48) * mm, "end": v(-169.5, 34.48) * mm});
            skPoint(sketch, "E12.0.4.4", {"position": v(-167, 34.48) * mm});
            skPoint(sketch, "E12.0.4.5", {"position": v(-167, 29.48) * mm});
            skArc(sketch, "E12.0.4.6", {"start": v(-197, 31.98) * mm, "mid": v(-196.27, 30.22) * mm, "end": v(-194.5, 29.48) * mm});
            skArc(sketch, "E12.0.4.7", {"start": v(-169.5, 29.48) * mm, "mid": v(-167.74, 30.22) * mm, "end": v(-167, 31.98) * mm});
            skArc(sketch, "E12.0.4.8", {"start": v(-194.5, 34.48) * mm, "mid": v(-196.27, 33.75) * mm, "end": v(-197, 31.98) * mm});
            skArc(sketch, "E12.0.4.9", {"start": v(-167, 31.98) * mm, "mid": v(-167.74, 33.75) * mm, "end": v(-169.5, 34.48) * mm});
            skLineSegment(sketch, "E12.0.5.0", {"start": v(-194.5, 49.48) * mm, "end": v(-169.5, 49.48) * mm});
            skPoint(sketch, "E12.0.5.1", {"position": v(-197, 49.48) * mm});
            skPoint(sketch, "E12.0.5.2", {"position": v(-197, 54.48) * mm});
            skLineSegment(sketch, "E12.0.5.3", {"start": v(-194.5, 54.48) * mm, "end": v(-169.5, 54.48) * mm});
            skPoint(sketch, "E12.0.5.4", {"position": v(-167, 54.48) * mm});
            skPoint(sketch, "E12.0.5.5", {"position": v(-167, 49.48) * mm});
            skArc(sketch, "E12.0.5.6", {"start": v(-197, 51.98) * mm, "mid": v(-196.27, 50.22) * mm, "end": v(-194.5, 49.48) * mm});
            skArc(sketch, "E12.0.5.7", {"start": v(-169.5, 49.48) * mm, "mid": v(-167.74, 50.22) * mm, "end": v(-167, 51.98) * mm});
            skArc(sketch, "E12.0.5.8", {"start": v(-194.5, 54.48) * mm, "mid": v(-196.27, 53.75) * mm, "end": v(-197, 51.98) * mm});
            skArc(sketch, "E12.0.5.9", {"start": v(-167, 51.98) * mm, "mid": v(-167.74, 53.75) * mm, "end": v(-169.5, 54.48) * mm});
            skLineSegment(sketch, "E12.1.0.0", {"start": v(-159.5, -50.52) * mm, "end": v(-134.5, -50.52) * mm});
            skPoint(sketch, "E12.1.0.1", {"position": v(-162, -50.52) * mm});
            skPoint(sketch, "E12.1.0.2", {"position": v(-162, -45.52) * mm});
            skLineSegment(sketch, "E12.1.0.3", {"start": v(-159.5, -45.52) * mm, "end": v(-134.5, -45.52) * mm});
            skPoint(sketch, "E12.1.0.4", {"position": v(-132, -45.52) * mm});
            skPoint(sketch, "E12.1.0.5", {"position": v(-132, -50.52) * mm});
            skArc(sketch, "E12.1.0.6", {"start": v(-162, -48.02) * mm, "mid": v(-161.27, -49.78) * mm, "end": v(-159.5, -50.52) * mm});
            skArc(sketch, "E12.1.0.7", {"start": v(-134.5, -50.52) * mm, "mid": v(-132.74, -49.78) * mm, "end": v(-132, -48.02) * mm});
            skArc(sketch, "E12.1.0.8", {"start": v(-159.5, -45.52) * mm, "mid": v(-161.27, -46.25) * mm, "end": v(-162, -48.02) * mm});
            skArc(sketch, "E12.1.0.9", {"start": v(-132, -48.02) * mm, "mid": v(-132.74, -46.25) * mm, "end": v(-134.5, -45.52) * mm});
            skLineSegment(sketch, "E12.1.1.0", {"start": v(-159.5, -30.52) * mm, "end": v(-134.5, -30.52) * mm});
            skPoint(sketch, "E12.1.1.1", {"position": v(-162, -30.52) * mm});
            skPoint(sketch, "E12.1.1.2", {"position": v(-162, -25.52) * mm});
            skLineSegment(sketch, "E12.1.1.3", {"start": v(-159.5, -25.52) * mm, "end": v(-134.5, -25.52) * mm});
            skPoint(sketch, "E12.1.1.4", {"position": v(-132, -25.52) * mm});
            skPoint(sketch, "E12.1.1.5", {"position": v(-132, -30.52) * mm});
            skArc(sketch, "E12.1.1.6", {"start": v(-162, -28.02) * mm, "mid": v(-161.27, -29.78) * mm, "end": v(-159.5, -30.52) * mm});
            skArc(sketch, "E12.1.1.7", {"start": v(-134.5, -30.52) * mm, "mid": v(-132.74, -29.78) * mm, "end": v(-132, -28.02) * mm});
            skArc(sketch, "E12.1.1.8", {"start": v(-159.5, -25.52) * mm, "mid": v(-161.27, -26.25) * mm, "end": v(-162, -28.02) * mm});
            skArc(sketch, "E12.1.1.9", {"start": v(-132, -28.02) * mm, "mid": v(-132.74, -26.25) * mm, "end": v(-134.5, -25.52) * mm});
            skLineSegment(sketch, "E12.1.2.0", {"start": v(-159.5, -10.52) * mm, "end": v(-134.5, -10.52) * mm});
            skPoint(sketch, "E12.1.2.1", {"position": v(-162, -10.52) * mm});
            skPoint(sketch, "E12.1.2.2", {"position": v(-162, -5.52) * mm});
            skLineSegment(sketch, "E12.1.2.3", {"start": v(-159.5, -5.52) * mm, "end": v(-134.5, -5.52) * mm});
            skPoint(sketch, "E12.1.2.4", {"position": v(-132, -5.52) * mm});
            skPoint(sketch, "E12.1.2.5", {"position": v(-132, -10.52) * mm});
            skArc(sketch, "E12.1.2.6", {"start": v(-162, -8.02) * mm, "mid": v(-161.27, -9.78) * mm, "end": v(-159.5, -10.52) * mm});
            skArc(sketch, "E12.1.2.7", {"start": v(-134.5, -10.52) * mm, "mid": v(-132.74, -9.78) * mm, "end": v(-132, -8.02) * mm});
            skArc(sketch, "E12.1.2.8", {"start": v(-159.5, -5.52) * mm, "mid": v(-161.27, -6.25) * mm, "end": v(-162, -8.02) * mm});
            skArc(sketch, "E12.1.2.9", {"start": v(-132, -8.02) * mm, "mid": v(-132.74, -6.25) * mm, "end": v(-134.5, -5.52) * mm});
            skLineSegment(sketch, "E12.1.3.0", {"start": v(-159.5, 9.48) * mm, "end": v(-134.5, 9.48) * mm});
            skPoint(sketch, "E12.1.3.1", {"position": v(-162, 9.48) * mm});
            skPoint(sketch, "E12.1.3.2", {"position": v(-162, 14.48) * mm});
            skLineSegment(sketch, "E12.1.3.3", {"start": v(-159.5, 14.48) * mm, "end": v(-134.5, 14.48) * mm});
            skPoint(sketch, "E12.1.3.4", {"position": v(-132, 14.48) * mm});
            skPoint(sketch, "E12.1.3.5", {"position": v(-132, 9.48) * mm});
            skArc(sketch, "E12.1.3.6", {"start": v(-162, 11.98) * mm, "mid": v(-161.27, 10.22) * mm, "end": v(-159.5, 9.48) * mm});
            skArc(sketch, "E12.1.3.7", {"start": v(-134.5, 9.48) * mm, "mid": v(-132.74, 10.22) * mm, "end": v(-132, 11.98) * mm});
            skArc(sketch, "E12.1.3.8", {"start": v(-159.5, 14.48) * mm, "mid": v(-161.27, 13.75) * mm, "end": v(-162, 11.98) * mm});
            skArc(sketch, "E12.1.3.9", {"start": v(-132, 11.98) * mm, "mid": v(-132.74, 13.75) * mm, "end": v(-134.5, 14.48) * mm});
            skLineSegment(sketch, "E12.1.4.0", {"start": v(-159.5, 29.48) * mm, "end": v(-134.5, 29.48) * mm});
            skPoint(sketch, "E12.1.4.1", {"position": v(-162, 29.48) * mm});
            skPoint(sketch, "E12.1.4.2", {"position": v(-162, 34.48) * mm});
            skLineSegment(sketch, "E12.1.4.3", {"start": v(-159.5, 34.48) * mm, "end": v(-134.5, 34.48) * mm});
            skPoint(sketch, "E12.1.4.4", {"position": v(-132, 34.48) * mm});
            skPoint(sketch, "E12.1.4.5", {"position": v(-132, 29.48) * mm});
            skArc(sketch, "E12.1.4.6", {"start": v(-162, 31.98) * mm, "mid": v(-161.27, 30.22) * mm, "end": v(-159.5, 29.48) * mm});
            skArc(sketch, "E12.1.4.7", {"start": v(-134.5, 29.48) * mm, "mid": v(-132.74, 30.22) * mm, "end": v(-132, 31.98) * mm});
            skArc(sketch, "E12.1.4.8", {"start": v(-159.5, 34.48) * mm, "mid": v(-161.27, 33.75) * mm, "end": v(-162, 31.98) * mm});
            skArc(sketch, "E12.1.4.9", {"start": v(-132, 31.98) * mm, "mid": v(-132.74, 33.75) * mm, "end": v(-134.5, 34.48) * mm});
            skLineSegment(sketch, "E12.1.5.0", {"start": v(-159.5, 49.48) * mm, "end": v(-134.5, 49.48) * mm});
            skPoint(sketch, "E12.1.5.1", {"position": v(-162, 49.48) * mm});
            skPoint(sketch, "E12.1.5.2", {"position": v(-162, 54.48) * mm});
            skLineSegment(sketch, "E12.1.5.3", {"start": v(-159.5, 54.48) * mm, "end": v(-134.5, 54.48) * mm});
            skPoint(sketch, "E12.1.5.4", {"position": v(-132, 54.48) * mm});
            skPoint(sketch, "E12.1.5.5", {"position": v(-132, 49.48) * mm});
            skArc(sketch, "E12.1.5.6", {"start": v(-162, 51.98) * mm, "mid": v(-161.27, 50.22) * mm, "end": v(-159.5, 49.48) * mm});
            skArc(sketch, "E12.1.5.7", {"start": v(-134.5, 49.48) * mm, "mid": v(-132.74, 50.22) * mm, "end": v(-132, 51.98) * mm});
            skArc(sketch, "E12.1.5.8", {"start": v(-159.5, 54.48) * mm, "mid": v(-161.27, 53.75) * mm, "end": v(-162, 51.98) * mm});
            skArc(sketch, "E12.1.5.9", {"start": v(-132, 51.98) * mm, "mid": v(-132.74, 53.75) * mm, "end": v(-134.5, 54.48) * mm});
            skLineSegment(sketch, "E12.2.0.0", {"start": v(-124.5, -50.52) * mm, "end": v(-99.5, -50.52) * mm});
            skPoint(sketch, "E12.2.0.1", {"position": v(-127, -50.52) * mm});
            skPoint(sketch, "E12.2.0.2", {"position": v(-127, -45.52) * mm});
            skLineSegment(sketch, "E12.2.0.3", {"start": v(-124.5, -45.52) * mm, "end": v(-99.5, -45.52) * mm});
            skPoint(sketch, "E12.2.0.4", {"position": v(-97, -45.52) * mm});
            skPoint(sketch, "E12.2.0.5", {"position": v(-97, -50.52) * mm});
            skArc(sketch, "E12.2.0.6", {"start": v(-127, -48.02) * mm, "mid": v(-126.27, -49.78) * mm, "end": v(-124.5, -50.52) * mm});
            skArc(sketch, "E12.2.0.7", {"start": v(-99.5, -50.52) * mm, "mid": v(-97.74, -49.78) * mm, "end": v(-97, -48.02) * mm});
            skArc(sketch, "E12.2.0.8", {"start": v(-124.5, -45.52) * mm, "mid": v(-126.27, -46.25) * mm, "end": v(-127, -48.02) * mm});
            skArc(sketch, "E12.2.0.9", {"start": v(-97, -48.02) * mm, "mid": v(-97.74, -46.25) * mm, "end": v(-99.5, -45.52) * mm});
            skLineSegment(sketch, "E12.2.1.0", {"start": v(-124.5, -30.52) * mm, "end": v(-99.5, -30.52) * mm});
            skPoint(sketch, "E12.2.1.1", {"position": v(-127, -30.52) * mm});
            skPoint(sketch, "E12.2.1.2", {"position": v(-127, -25.52) * mm});
            skLineSegment(sketch, "E12.2.1.3", {"start": v(-124.5, -25.52) * mm, "end": v(-99.5, -25.52) * mm});
            skPoint(sketch, "E12.2.1.4", {"position": v(-97, -25.52) * mm});
            skPoint(sketch, "E12.2.1.5", {"position": v(-97, -30.52) * mm});
            skArc(sketch, "E12.2.1.6", {"start": v(-127, -28.02) * mm, "mid": v(-126.27, -29.78) * mm, "end": v(-124.5, -30.52) * mm});
            skArc(sketch, "E12.2.1.7", {"start": v(-99.5, -30.52) * mm, "mid": v(-97.74, -29.78) * mm, "end": v(-97, -28.02) * mm});
            skArc(sketch, "E12.2.1.8", {"start": v(-124.5, -25.52) * mm, "mid": v(-126.27, -26.25) * mm, "end": v(-127, -28.02) * mm});
            skArc(sketch, "E12.2.1.9", {"start": v(-97, -28.02) * mm, "mid": v(-97.74, -26.25) * mm, "end": v(-99.5, -25.52) * mm});
            skLineSegment(sketch, "E12.2.2.0", {"start": v(-124.5, -10.52) * mm, "end": v(-99.5, -10.52) * mm});
            skPoint(sketch, "E12.2.2.1", {"position": v(-127, -10.52) * mm});
            skPoint(sketch, "E12.2.2.2", {"position": v(-127, -5.52) * mm});
            skLineSegment(sketch, "E12.2.2.3", {"start": v(-124.5, -5.52) * mm, "end": v(-99.5, -5.52) * mm});
            skPoint(sketch, "E12.2.2.4", {"position": v(-97, -5.52) * mm});
            skPoint(sketch, "E12.2.2.5", {"position": v(-97, -10.52) * mm});
            skArc(sketch, "E12.2.2.6", {"start": v(-127, -8.02) * mm, "mid": v(-126.27, -9.78) * mm, "end": v(-124.5, -10.52) * mm});
            skArc(sketch, "E12.2.2.7", {"start": v(-99.5, -10.52) * mm, "mid": v(-97.74, -9.78) * mm, "end": v(-97, -8.02) * mm});
            skArc(sketch, "E12.2.2.8", {"start": v(-124.5, -5.52) * mm, "mid": v(-126.27, -6.25) * mm, "end": v(-127, -8.02) * mm});
            skArc(sketch, "E12.2.2.9", {"start": v(-97, -8.02) * mm, "mid": v(-97.74, -6.25) * mm, "end": v(-99.5, -5.52) * mm});
            skLineSegment(sketch, "E12.2.3.0", {"start": v(-124.5, 9.48) * mm, "end": v(-99.5, 9.48) * mm});
            skPoint(sketch, "E12.2.3.1", {"position": v(-127, 9.48) * mm});
            skPoint(sketch, "E12.2.3.2", {"position": v(-127, 14.48) * mm});
            skLineSegment(sketch, "E12.2.3.3", {"start": v(-124.5, 14.48) * mm, "end": v(-99.5, 14.48) * mm});
            skPoint(sketch, "E12.2.3.4", {"position": v(-97, 14.48) * mm});
            skPoint(sketch, "E12.2.3.5", {"position": v(-97, 9.48) * mm});
            skArc(sketch, "E12.2.3.6", {"start": v(-127, 11.98) * mm, "mid": v(-126.27, 10.22) * mm, "end": v(-124.5, 9.48) * mm});
            skArc(sketch, "E12.2.3.7", {"start": v(-99.5, 9.48) * mm, "mid": v(-97.74, 10.22) * mm, "end": v(-97, 11.98) * mm});
            skArc(sketch, "E12.2.3.8", {"start": v(-124.5, 14.48) * mm, "mid": v(-126.27, 13.75) * mm, "end": v(-127, 11.98) * mm});
            skArc(sketch, "E12.2.3.9", {"start": v(-97, 11.98) * mm, "mid": v(-97.74, 13.75) * mm, "end": v(-99.5, 14.48) * mm});
            skLineSegment(sketch, "E12.2.4.0", {"start": v(-124.5, 29.48) * mm, "end": v(-99.5, 29.48) * mm});
            skPoint(sketch, "E12.2.4.1", {"position": v(-127, 29.48) * mm});
            skPoint(sketch, "E12.2.4.2", {"position": v(-127, 34.48) * mm});
            skLineSegment(sketch, "E12.2.4.3", {"start": v(-124.5, 34.48) * mm, "end": v(-99.5, 34.48) * mm});
            skPoint(sketch, "E12.2.4.4", {"position": v(-97, 34.48) * mm});
            skPoint(sketch, "E12.2.4.5", {"position": v(-97, 29.48) * mm});
            skArc(sketch, "E12.2.4.6", {"start": v(-127, 31.98) * mm, "mid": v(-126.27, 30.22) * mm, "end": v(-124.5, 29.48) * mm});
            skArc(sketch, "E12.2.4.7", {"start": v(-99.5, 29.48) * mm, "mid": v(-97.74, 30.22) * mm, "end": v(-97, 31.98) * mm});
            skArc(sketch, "E12.2.4.8", {"start": v(-124.5, 34.48) * mm, "mid": v(-126.27, 33.75) * mm, "end": v(-127, 31.98) * mm});
            skArc(sketch, "E12.2.4.9", {"start": v(-97, 31.98) * mm, "mid": v(-97.74, 33.75) * mm, "end": v(-99.5, 34.48) * mm});
            skLineSegment(sketch, "E12.2.5.0", {"start": v(-124.5, 49.48) * mm, "end": v(-99.5, 49.48) * mm});
            skPoint(sketch, "E12.2.5.1", {"position": v(-127, 49.48) * mm});
            skPoint(sketch, "E12.2.5.2", {"position": v(-127, 54.48) * mm});
            skLineSegment(sketch, "E12.2.5.3", {"start": v(-124.5, 54.48) * mm, "end": v(-99.5, 54.48) * mm});
            skPoint(sketch, "E12.2.5.4", {"position": v(-97, 54.48) * mm});
            skPoint(sketch, "E12.2.5.5", {"position": v(-97, 49.48) * mm});
            skArc(sketch, "E12.2.5.6", {"start": v(-127, 51.98) * mm, "mid": v(-126.27, 50.22) * mm, "end": v(-124.5, 49.48) * mm});
            skArc(sketch, "E12.2.5.7", {"start": v(-99.5, 49.48) * mm, "mid": v(-97.74, 50.22) * mm, "end": v(-97, 51.98) * mm});
            skArc(sketch, "E12.2.5.8", {"start": v(-124.5, 54.48) * mm, "mid": v(-126.27, 53.75) * mm, "end": v(-127, 51.98) * mm});
            skArc(sketch, "E12.2.5.9", {"start": v(-97, 51.98) * mm, "mid": v(-97.74, 53.75) * mm, "end": v(-99.5, 54.48) * mm});
            skLineSegment(sketch, "E12.3.0.0", {"start": v(-89.5, -50.52) * mm, "end": v(-64.5, -50.52) * mm});
            skPoint(sketch, "E12.3.0.1", {"position": v(-92, -50.52) * mm});
            skPoint(sketch, "E12.3.0.2", {"position": v(-92, -45.52) * mm});
            skLineSegment(sketch, "E12.3.0.3", {"start": v(-89.5, -45.52) * mm, "end": v(-64.5, -45.52) * mm});
            skPoint(sketch, "E12.3.0.4", {"position": v(-62, -45.52) * mm});
            skPoint(sketch, "E12.3.0.5", {"position": v(-62, -50.52) * mm});
            skArc(sketch, "E12.3.0.6", {"start": v(-92, -48.02) * mm, "mid": v(-91.27, -49.78) * mm, "end": v(-89.5, -50.52) * mm});
            skArc(sketch, "E12.3.0.7", {"start": v(-64.5, -50.52) * mm, "mid": v(-62.74, -49.78) * mm, "end": v(-62, -48.02) * mm});
            skArc(sketch, "E12.3.0.8", {"start": v(-89.5, -45.52) * mm, "mid": v(-91.27, -46.25) * mm, "end": v(-92, -48.02) * mm});
            skArc(sketch, "E12.3.0.9", {"start": v(-62, -48.02) * mm, "mid": v(-62.74, -46.25) * mm, "end": v(-64.5, -45.52) * mm});
            skLineSegment(sketch, "E12.3.1.0", {"start": v(-89.5, -30.52) * mm, "end": v(-64.5, -30.52) * mm});
            skPoint(sketch, "E12.3.1.1", {"position": v(-92, -30.52) * mm});
            skPoint(sketch, "E12.3.1.2", {"position": v(-92, -25.52) * mm});
            skLineSegment(sketch, "E12.3.1.3", {"start": v(-89.5, -25.52) * mm, "end": v(-64.5, -25.52) * mm});
            skPoint(sketch, "E12.3.1.4", {"position": v(-62, -25.52) * mm});
            skPoint(sketch, "E12.3.1.5", {"position": v(-62, -30.52) * mm});
            skArc(sketch, "E12.3.1.6", {"start": v(-92, -28.02) * mm, "mid": v(-91.27, -29.78) * mm, "end": v(-89.5, -30.52) * mm});
            skArc(sketch, "E12.3.1.7", {"start": v(-64.5, -30.52) * mm, "mid": v(-62.74, -29.78) * mm, "end": v(-62, -28.02) * mm});
            skArc(sketch, "E12.3.1.8", {"start": v(-89.5, -25.52) * mm, "mid": v(-91.27, -26.25) * mm, "end": v(-92, -28.02) * mm});
            skArc(sketch, "E12.3.1.9", {"start": v(-62, -28.02) * mm, "mid": v(-62.74, -26.25) * mm, "end": v(-64.5, -25.52) * mm});
            skLineSegment(sketch, "E12.3.2.0", {"start": v(-89.5, -10.52) * mm, "end": v(-64.5, -10.52) * mm});
            skPoint(sketch, "E12.3.2.1", {"position": v(-92, -10.52) * mm});
            skPoint(sketch, "E12.3.2.2", {"position": v(-92, -5.52) * mm});
            skLineSegment(sketch, "E12.3.2.3", {"start": v(-89.5, -5.52) * mm, "end": v(-64.5, -5.52) * mm});
            skPoint(sketch, "E12.3.2.4", {"position": v(-62, -5.52) * mm});
            skPoint(sketch, "E12.3.2.5", {"position": v(-62, -10.52) * mm});
            skArc(sketch, "E12.3.2.6", {"start": v(-92, -8.02) * mm, "mid": v(-91.27, -9.78) * mm, "end": v(-89.5, -10.52) * mm});
            skArc(sketch, "E12.3.2.7", {"start": v(-64.5, -10.52) * mm, "mid": v(-62.74, -9.78) * mm, "end": v(-62, -8.02) * mm});
            skArc(sketch, "E12.3.2.8", {"start": v(-89.5, -5.52) * mm, "mid": v(-91.27, -6.25) * mm, "end": v(-92, -8.02) * mm});
            skArc(sketch, "E12.3.2.9", {"start": v(-62, -8.02) * mm, "mid": v(-62.74, -6.25) * mm, "end": v(-64.5, -5.52) * mm});
            skLineSegment(sketch, "E12.3.3.0", {"start": v(-89.5, 9.48) * mm, "end": v(-64.5, 9.48) * mm});
            skPoint(sketch, "E12.3.3.1", {"position": v(-92, 9.48) * mm});
            skPoint(sketch, "E12.3.3.2", {"position": v(-92, 14.48) * mm});
            skLineSegment(sketch, "E12.3.3.3", {"start": v(-89.5, 14.48) * mm, "end": v(-64.5, 14.48) * mm});
            skPoint(sketch, "E12.3.3.4", {"position": v(-62, 14.48) * mm});
            skPoint(sketch, "E12.3.3.5", {"position": v(-62, 9.48) * mm});
            skArc(sketch, "E12.3.3.6", {"start": v(-92, 11.98) * mm, "mid": v(-91.27, 10.22) * mm, "end": v(-89.5, 9.48) * mm});
            skArc(sketch, "E12.3.3.7", {"start": v(-64.5, 9.48) * mm, "mid": v(-62.74, 10.22) * mm, "end": v(-62, 11.98) * mm});
            skArc(sketch, "E12.3.3.8", {"start": v(-89.5, 14.48) * mm, "mid": v(-91.27, 13.75) * mm, "end": v(-92, 11.98) * mm});
            skArc(sketch, "E12.3.3.9", {"start": v(-62, 11.98) * mm, "mid": v(-62.74, 13.75) * mm, "end": v(-64.5, 14.48) * mm});
            skLineSegment(sketch, "E12.3.4.0", {"start": v(-89.5, 29.48) * mm, "end": v(-64.5, 29.48) * mm});
            skPoint(sketch, "E12.3.4.1", {"position": v(-92, 29.48) * mm});
            skPoint(sketch, "E12.3.4.2", {"position": v(-92, 34.48) * mm});
            skLineSegment(sketch, "E12.3.4.3", {"start": v(-89.5, 34.48) * mm, "end": v(-64.5, 34.48) * mm});
            skPoint(sketch, "E12.3.4.4", {"position": v(-62, 34.48) * mm});
            skPoint(sketch, "E12.3.4.5", {"position": v(-62, 29.48) * mm});
            skArc(sketch, "E12.3.4.6", {"start": v(-92, 31.98) * mm, "mid": v(-91.27, 30.22) * mm, "end": v(-89.5, 29.48) * mm});
            skArc(sketch, "E12.3.4.7", {"start": v(-64.5, 29.48) * mm, "mid": v(-62.74, 30.22) * mm, "end": v(-62, 31.98) * mm});
            skArc(sketch, "E12.3.4.8", {"start": v(-89.5, 34.48) * mm, "mid": v(-91.27, 33.75) * mm, "end": v(-92, 31.98) * mm});
            skArc(sketch, "E12.3.4.9", {"start": v(-62, 31.98) * mm, "mid": v(-62.74, 33.75) * mm, "end": v(-64.5, 34.48) * mm});
            skLineSegment(sketch, "E12.3.5.0", {"start": v(-89.5, 49.48) * mm, "end": v(-64.5, 49.48) * mm});
            skPoint(sketch, "E12.3.5.1", {"position": v(-92, 49.48) * mm});
            skPoint(sketch, "E12.3.5.2", {"position": v(-92, 54.48) * mm});
            skLineSegment(sketch, "E12.3.5.3", {"start": v(-89.5, 54.48) * mm, "end": v(-64.5, 54.48) * mm});
            skPoint(sketch, "E12.3.5.4", {"position": v(-62, 54.48) * mm});
            skPoint(sketch, "E12.3.5.5", {"position": v(-62, 49.48) * mm});
            skArc(sketch, "E12.3.5.6", {"start": v(-92, 51.98) * mm, "mid": v(-91.27, 50.22) * mm, "end": v(-89.5, 49.48) * mm});
            skArc(sketch, "E12.3.5.7", {"start": v(-64.5, 49.48) * mm, "mid": v(-62.74, 50.22) * mm, "end": v(-62, 51.98) * mm});
            skArc(sketch, "E12.3.5.8", {"start": v(-89.5, 54.48) * mm, "mid": v(-91.27, 53.75) * mm, "end": v(-92, 51.98) * mm});
            skArc(sketch, "E12.3.5.9", {"start": v(-62, 51.98) * mm, "mid": v(-62.74, 53.75) * mm, "end": v(-64.5, 54.48) * mm});
            skLineSegment(sketch, "E12.4.0.0", {"start": v(-54.5, -50.52) * mm, "end": v(-29.5, -50.52) * mm});
            skPoint(sketch, "E12.4.0.1", {"position": v(-57, -50.52) * mm});
            skPoint(sketch, "E12.4.0.2", {"position": v(-57, -45.52) * mm});
            skLineSegment(sketch, "E12.4.0.3", {"start": v(-54.5, -45.52) * mm, "end": v(-29.5, -45.52) * mm});
            skPoint(sketch, "E12.4.0.4", {"position": v(-27, -45.52) * mm});
            skPoint(sketch, "E12.4.0.5", {"position": v(-27, -50.52) * mm});
            skArc(sketch, "E12.4.0.6", {"start": v(-57, -48.02) * mm, "mid": v(-56.27, -49.78) * mm, "end": v(-54.5, -50.52) * mm});
            skArc(sketch, "E12.4.0.7", {"start": v(-29.5, -50.52) * mm, "mid": v(-27.74, -49.78) * mm, "end": v(-27, -48.02) * mm});
            skArc(sketch, "E12.4.0.8", {"start": v(-54.5, -45.52) * mm, "mid": v(-56.27, -46.25) * mm, "end": v(-57, -48.02) * mm});
            skArc(sketch, "E12.4.0.9", {"start": v(-27, -48.02) * mm, "mid": v(-27.74, -46.25) * mm, "end": v(-29.5, -45.52) * mm});
            skLineSegment(sketch, "E12.4.1.0", {"start": v(-54.5, -30.52) * mm, "end": v(-29.5, -30.52) * mm});
            skPoint(sketch, "E12.4.1.1", {"position": v(-57, -30.52) * mm});
            skPoint(sketch, "E12.4.1.2", {"position": v(-57, -25.52) * mm});
            skLineSegment(sketch, "E12.4.1.3", {"start": v(-54.5, -25.52) * mm, "end": v(-29.5, -25.52) * mm});
            skPoint(sketch, "E12.4.1.4", {"position": v(-27, -25.52) * mm});
            skPoint(sketch, "E12.4.1.5", {"position": v(-27, -30.52) * mm});
            skArc(sketch, "E12.4.1.6", {"start": v(-57, -28.02) * mm, "mid": v(-56.27, -29.78) * mm, "end": v(-54.5, -30.52) * mm});
            skArc(sketch, "E12.4.1.7", {"start": v(-29.5, -30.52) * mm, "mid": v(-27.74, -29.78) * mm, "end": v(-27, -28.02) * mm});
            skArc(sketch, "E12.4.1.8", {"start": v(-54.5, -25.52) * mm, "mid": v(-56.27, -26.25) * mm, "end": v(-57, -28.02) * mm});
            skArc(sketch, "E12.4.1.9", {"start": v(-27, -28.02) * mm, "mid": v(-27.74, -26.25) * mm, "end": v(-29.5, -25.52) * mm});
            skLineSegment(sketch, "E12.4.2.0", {"start": v(-54.5, -10.52) * mm, "end": v(-29.5, -10.52) * mm});
            skPoint(sketch, "E12.4.2.1", {"position": v(-57, -10.52) * mm});
            skPoint(sketch, "E12.4.2.2", {"position": v(-57, -5.52) * mm});
            skLineSegment(sketch, "E12.4.2.3", {"start": v(-54.5, -5.52) * mm, "end": v(-29.5, -5.52) * mm});
            skPoint(sketch, "E12.4.2.4", {"position": v(-27, -5.52) * mm});
            skPoint(sketch, "E12.4.2.5", {"position": v(-27, -10.52) * mm});
            skArc(sketch, "E12.4.2.6", {"start": v(-57, -8.02) * mm, "mid": v(-56.27, -9.78) * mm, "end": v(-54.5, -10.52) * mm});
            skArc(sketch, "E12.4.2.7", {"start": v(-29.5, -10.52) * mm, "mid": v(-27.74, -9.78) * mm, "end": v(-27, -8.02) * mm});
            skArc(sketch, "E12.4.2.8", {"start": v(-54.5, -5.52) * mm, "mid": v(-56.27, -6.25) * mm, "end": v(-57, -8.02) * mm});
            skArc(sketch, "E12.4.2.9", {"start": v(-27, -8.02) * mm, "mid": v(-27.74, -6.25) * mm, "end": v(-29.5, -5.52) * mm});
            skLineSegment(sketch, "E12.4.3.0", {"start": v(-54.5, 9.48) * mm, "end": v(-29.5, 9.48) * mm});
            skPoint(sketch, "E12.4.3.1", {"position": v(-57, 9.48) * mm});
            skPoint(sketch, "E12.4.3.2", {"position": v(-57, 14.48) * mm});
            skLineSegment(sketch, "E12.4.3.3", {"start": v(-54.5, 14.48) * mm, "end": v(-29.5, 14.48) * mm});
            skPoint(sketch, "E12.4.3.4", {"position": v(-27, 14.48) * mm});
            skPoint(sketch, "E12.4.3.5", {"position": v(-27, 9.48) * mm});
            skArc(sketch, "E12.4.3.6", {"start": v(-57, 11.98) * mm, "mid": v(-56.27, 10.22) * mm, "end": v(-54.5, 9.48) * mm});
            skArc(sketch, "E12.4.3.7", {"start": v(-29.5, 9.48) * mm, "mid": v(-27.74, 10.22) * mm, "end": v(-27, 11.98) * mm});
            skArc(sketch, "E12.4.3.8", {"start": v(-54.5, 14.48) * mm, "mid": v(-56.27, 13.75) * mm, "end": v(-57, 11.98) * mm});
            skArc(sketch, "E12.4.3.9", {"start": v(-27, 11.98) * mm, "mid": v(-27.74, 13.75) * mm, "end": v(-29.5, 14.48) * mm});
            skLineSegment(sketch, "E12.4.4.0", {"start": v(-54.5, 29.48) * mm, "end": v(-29.5, 29.48) * mm});
            skPoint(sketch, "E12.4.4.1", {"position": v(-57, 29.48) * mm});
            skPoint(sketch, "E12.4.4.2", {"position": v(-57, 34.48) * mm});
            skLineSegment(sketch, "E12.4.4.3", {"start": v(-54.5, 34.48) * mm, "end": v(-29.5, 34.48) * mm});
            skPoint(sketch, "E12.4.4.4", {"position": v(-27, 34.48) * mm});
            skPoint(sketch, "E12.4.4.5", {"position": v(-27, 29.48) * mm});
            skArc(sketch, "E12.4.4.6", {"start": v(-57, 31.98) * mm, "mid": v(-56.27, 30.22) * mm, "end": v(-54.5, 29.48) * mm});
            skArc(sketch, "E12.4.4.7", {"start": v(-29.5, 29.48) * mm, "mid": v(-27.74, 30.22) * mm, "end": v(-27, 31.98) * mm});
            skArc(sketch, "E12.4.4.8", {"start": v(-54.5, 34.48) * mm, "mid": v(-56.27, 33.75) * mm, "end": v(-57, 31.98) * mm});
            skArc(sketch, "E12.4.4.9", {"start": v(-27, 31.98) * mm, "mid": v(-27.74, 33.75) * mm, "end": v(-29.5, 34.48) * mm});
            skLineSegment(sketch, "E12.4.5.0", {"start": v(-54.5, 49.48) * mm, "end": v(-29.5, 49.48) * mm});
            skPoint(sketch, "E12.4.5.1", {"position": v(-57, 49.48) * mm});
            skPoint(sketch, "E12.4.5.2", {"position": v(-57, 54.48) * mm});
            skLineSegment(sketch, "E12.4.5.3", {"start": v(-54.5, 54.48) * mm, "end": v(-29.5, 54.48) * mm});
            skPoint(sketch, "E12.4.5.4", {"position": v(-27, 54.48) * mm});
            skPoint(sketch, "E12.4.5.5", {"position": v(-27, 49.48) * mm});
            skArc(sketch, "E12.4.5.6", {"start": v(-57, 51.98) * mm, "mid": v(-56.27, 50.22) * mm, "end": v(-54.5, 49.48) * mm});
            skArc(sketch, "E12.4.5.7", {"start": v(-29.5, 49.48) * mm, "mid": v(-27.74, 50.22) * mm, "end": v(-27, 51.98) * mm});
            skArc(sketch, "E12.4.5.8", {"start": v(-54.5, 54.48) * mm, "mid": v(-56.27, 53.75) * mm, "end": v(-57, 51.98) * mm});
            skArc(sketch, "E12.4.5.9", {"start": v(-27, 51.98) * mm, "mid": v(-27.74, 53.75) * mm, "end": v(-29.5, 54.48) * mm});
            skLineSegment(sketch, "E12.5.0.0", {"start": v(-19.5, -50.52) * mm, "end": v(5.5, -50.52) * mm});
            skPoint(sketch, "E12.5.0.1", {"position": v(-22, -50.52) * mm});
            skPoint(sketch, "E12.5.0.2", {"position": v(-22, -45.52) * mm});
            skLineSegment(sketch, "E12.5.0.3", {"start": v(-19.5, -45.52) * mm, "end": v(5.5, -45.52) * mm});
            skPoint(sketch, "E12.5.0.4", {"position": v(8, -45.52) * mm});
            skPoint(sketch, "E12.5.0.5", {"position": v(8, -50.52) * mm});
            skArc(sketch, "E12.5.0.6", {"start": v(-22, -48.02) * mm, "mid": v(-21.27, -49.78) * mm, "end": v(-19.5, -50.52) * mm});
            skArc(sketch, "E12.5.0.7", {"start": v(5.5, -50.52) * mm, "mid": v(7.26, -49.78) * mm, "end": v(8, -48.02) * mm});
            skArc(sketch, "E12.5.0.8", {"start": v(-19.5, -45.52) * mm, "mid": v(-21.27, -46.25) * mm, "end": v(-22, -48.02) * mm});
            skArc(sketch, "E12.5.0.9", {"start": v(8, -48.02) * mm, "mid": v(7.26, -46.25) * mm, "end": v(5.5, -45.52) * mm});
            skLineSegment(sketch, "E12.5.1.0", {"start": v(-19.5, -30.52) * mm, "end": v(5.5, -30.52) * mm});
            skPoint(sketch, "E12.5.1.1", {"position": v(-22, -30.52) * mm});
            skPoint(sketch, "E12.5.1.2", {"position": v(-22, -25.52) * mm});
            skLineSegment(sketch, "E12.5.1.3", {"start": v(-19.5, -25.52) * mm, "end": v(5.5, -25.52) * mm});
            skPoint(sketch, "E12.5.1.4", {"position": v(8, -25.52) * mm});
            skPoint(sketch, "E12.5.1.5", {"position": v(8, -30.52) * mm});
            skArc(sketch, "E12.5.1.6", {"start": v(-22, -28.02) * mm, "mid": v(-21.27, -29.78) * mm, "end": v(-19.5, -30.52) * mm});
            skArc(sketch, "E12.5.1.7", {"start": v(5.5, -30.52) * mm, "mid": v(7.26, -29.78) * mm, "end": v(8, -28.02) * mm});
            skArc(sketch, "E12.5.1.8", {"start": v(-19.5, -25.52) * mm, "mid": v(-21.27, -26.25) * mm, "end": v(-22, -28.02) * mm});
            skArc(sketch, "E12.5.1.9", {"start": v(8, -28.02) * mm, "mid": v(7.26, -26.25) * mm, "end": v(5.5, -25.52) * mm});
            skLineSegment(sketch, "E12.5.2.0", {"start": v(-19.5, -10.52) * mm, "end": v(5.5, -10.52) * mm});
            skPoint(sketch, "E12.5.2.1", {"position": v(-22, -10.52) * mm});
            skPoint(sketch, "E12.5.2.2", {"position": v(-22, -5.52) * mm});
            skLineSegment(sketch, "E12.5.2.3", {"start": v(-19.5, -5.52) * mm, "end": v(5.5, -5.52) * mm});
            skPoint(sketch, "E12.5.2.4", {"position": v(8, -5.52) * mm});
            skPoint(sketch, "E12.5.2.5", {"position": v(8, -10.52) * mm});
            skArc(sketch, "E12.5.2.6", {"start": v(-22, -8.02) * mm, "mid": v(-21.27, -9.78) * mm, "end": v(-19.5, -10.52) * mm});
            skArc(sketch, "E12.5.2.7", {"start": v(5.5, -10.52) * mm, "mid": v(7.26, -9.78) * mm, "end": v(8, -8.02) * mm});
            skArc(sketch, "E12.5.2.8", {"start": v(-19.5, -5.52) * mm, "mid": v(-21.27, -6.25) * mm, "end": v(-22, -8.02) * mm});
            skArc(sketch, "E12.5.2.9", {"start": v(8, -8.02) * mm, "mid": v(7.26, -6.25) * mm, "end": v(5.5, -5.52) * mm});
            skLineSegment(sketch, "E12.5.3.0", {"start": v(-19.5, 9.48) * mm, "end": v(5.5, 9.48) * mm});
            skPoint(sketch, "E12.5.3.1", {"position": v(-22, 9.48) * mm});
            skPoint(sketch, "E12.5.3.2", {"position": v(-22, 14.48) * mm});
            skLineSegment(sketch, "E12.5.3.3", {"start": v(-19.5, 14.48) * mm, "end": v(5.5, 14.48) * mm});
            skPoint(sketch, "E12.5.3.4", {"position": v(8, 14.48) * mm});
            skPoint(sketch, "E12.5.3.5", {"position": v(8, 9.48) * mm});
            skArc(sketch, "E12.5.3.6", {"start": v(-22, 11.98) * mm, "mid": v(-21.27, 10.22) * mm, "end": v(-19.5, 9.48) * mm});
            skArc(sketch, "E12.5.3.7", {"start": v(5.5, 9.48) * mm, "mid": v(7.26, 10.22) * mm, "end": v(8, 11.98) * mm});
            skArc(sketch, "E12.5.3.8", {"start": v(-19.5, 14.48) * mm, "mid": v(-21.27, 13.75) * mm, "end": v(-22, 11.98) * mm});
            skArc(sketch, "E12.5.3.9", {"start": v(8, 11.98) * mm, "mid": v(7.26, 13.75) * mm, "end": v(5.5, 14.48) * mm});
            skLineSegment(sketch, "E12.5.4.0", {"start": v(-19.5, 29.48) * mm, "end": v(5.5, 29.48) * mm});
            skPoint(sketch, "E12.5.4.1", {"position": v(-22, 29.48) * mm});
            skPoint(sketch, "E12.5.4.2", {"position": v(-22, 34.48) * mm});
            skLineSegment(sketch, "E12.5.4.3", {"start": v(-19.5, 34.48) * mm, "end": v(5.5, 34.48) * mm});
            skPoint(sketch, "E12.5.4.4", {"position": v(8, 34.48) * mm});
            skPoint(sketch, "E12.5.4.5", {"position": v(8, 29.48) * mm});
            skArc(sketch, "E12.5.4.6", {"start": v(-22, 31.98) * mm, "mid": v(-21.27, 30.22) * mm, "end": v(-19.5, 29.48) * mm});
            skArc(sketch, "E12.5.4.7", {"start": v(5.5, 29.48) * mm, "mid": v(7.26, 30.22) * mm, "end": v(8, 31.98) * mm});
            skArc(sketch, "E12.5.4.8", {"start": v(-19.5, 34.48) * mm, "mid": v(-21.27, 33.75) * mm, "end": v(-22, 31.98) * mm});
            skArc(sketch, "E12.5.4.9", {"start": v(8, 31.98) * mm, "mid": v(7.26, 33.75) * mm, "end": v(5.5, 34.48) * mm});
            skLineSegment(sketch, "E12.5.5.0", {"start": v(-19.5, 49.48) * mm, "end": v(5.5, 49.48) * mm});
            skPoint(sketch, "E12.5.5.1", {"position": v(-22, 49.48) * mm});
            skPoint(sketch, "E12.5.5.2", {"position": v(-22, 54.48) * mm});
            skLineSegment(sketch, "E12.5.5.3", {"start": v(-19.5, 54.48) * mm, "end": v(5.5, 54.48) * mm});
            skPoint(sketch, "E12.5.5.4", {"position": v(8, 54.48) * mm});
            skPoint(sketch, "E12.5.5.5", {"position": v(8, 49.48) * mm});
            skArc(sketch, "E12.5.5.6", {"start": v(-22, 51.98) * mm, "mid": v(-21.27, 50.22) * mm, "end": v(-19.5, 49.48) * mm});
            skArc(sketch, "E12.5.5.7", {"start": v(5.5, 49.48) * mm, "mid": v(7.26, 50.22) * mm, "end": v(8, 51.98) * mm});
            skArc(sketch, "E12.5.5.8", {"start": v(-19.5, 54.48) * mm, "mid": v(-21.27, 53.75) * mm, "end": v(-22, 51.98) * mm});
            skArc(sketch, "E12.5.5.9", {"start": v(8, 51.98) * mm, "mid": v(7.26, 53.75) * mm, "end": v(5.5, 54.48) * mm});
            skLineSegment(sketch, "E12.6.0.0", {"start": v(15.5, -50.52) * mm, "end": v(40.5, -50.52) * mm});
            skPoint(sketch, "E12.6.0.1", {"position": v(13, -50.52) * mm});
            skPoint(sketch, "E12.6.0.2", {"position": v(13, -45.52) * mm});
            skLineSegment(sketch, "E12.6.0.3", {"start": v(15.5, -45.52) * mm, "end": v(40.5, -45.52) * mm});
            skPoint(sketch, "E12.6.0.4", {"position": v(43, -45.52) * mm});
            skPoint(sketch, "E12.6.0.5", {"position": v(43, -50.52) * mm});
            skArc(sketch, "E12.6.0.6", {"start": v(13, -48.02) * mm, "mid": v(13.73, -49.78) * mm, "end": v(15.5, -50.52) * mm});
            skArc(sketch, "E12.6.0.7", {"start": v(40.5, -50.52) * mm, "mid": v(42.26, -49.78) * mm, "end": v(43, -48.02) * mm});
            skArc(sketch, "E12.6.0.8", {"start": v(15.5, -45.52) * mm, "mid": v(13.73, -46.25) * mm, "end": v(13, -48.02) * mm});
            skArc(sketch, "E12.6.0.9", {"start": v(43, -48.02) * mm, "mid": v(42.26, -46.25) * mm, "end": v(40.5, -45.52) * mm});
            skLineSegment(sketch, "E12.6.1.0", {"start": v(15.5, -30.52) * mm, "end": v(40.5, -30.52) * mm});
            skPoint(sketch, "E12.6.1.1", {"position": v(13, -30.52) * mm});
            skPoint(sketch, "E12.6.1.2", {"position": v(13, -25.52) * mm});
            skLineSegment(sketch, "E12.6.1.3", {"start": v(15.5, -25.52) * mm, "end": v(40.5, -25.52) * mm});
            skPoint(sketch, "E12.6.1.4", {"position": v(43, -25.52) * mm});
            skPoint(sketch, "E12.6.1.5", {"position": v(43, -30.52) * mm});
            skArc(sketch, "E12.6.1.6", {"start": v(13, -28.02) * mm, "mid": v(13.73, -29.78) * mm, "end": v(15.5, -30.52) * mm});
            skArc(sketch, "E12.6.1.7", {"start": v(40.5, -30.52) * mm, "mid": v(42.26, -29.78) * mm, "end": v(43, -28.02) * mm});
            skArc(sketch, "E12.6.1.8", {"start": v(15.5, -25.52) * mm, "mid": v(13.73, -26.25) * mm, "end": v(13, -28.02) * mm});
            skArc(sketch, "E12.6.1.9", {"start": v(43, -28.02) * mm, "mid": v(42.26, -26.25) * mm, "end": v(40.5, -25.52) * mm});
            skLineSegment(sketch, "E12.6.2.0", {"start": v(15.5, -10.52) * mm, "end": v(40.5, -10.52) * mm});
            skPoint(sketch, "E12.6.2.1", {"position": v(13, -10.52) * mm});
            skPoint(sketch, "E12.6.2.2", {"position": v(13, -5.52) * mm});
            skLineSegment(sketch, "E12.6.2.3", {"start": v(15.5, -5.52) * mm, "end": v(40.5, -5.52) * mm});
            skPoint(sketch, "E12.6.2.4", {"position": v(43, -5.52) * mm});
            skPoint(sketch, "E12.6.2.5", {"position": v(43, -10.52) * mm});
            skArc(sketch, "E12.6.2.6", {"start": v(13, -8.02) * mm, "mid": v(13.73, -9.78) * mm, "end": v(15.5, -10.52) * mm});
            skArc(sketch, "E12.6.2.7", {"start": v(40.5, -10.52) * mm, "mid": v(42.26, -9.78) * mm, "end": v(43, -8.02) * mm});
            skArc(sketch, "E12.6.2.8", {"start": v(15.5, -5.52) * mm, "mid": v(13.73, -6.25) * mm, "end": v(13, -8.02) * mm});
            skArc(sketch, "E12.6.2.9", {"start": v(43, -8.02) * mm, "mid": v(42.26, -6.25) * mm, "end": v(40.5, -5.52) * mm});
            skLineSegment(sketch, "E12.6.3.0", {"start": v(15.5, 9.48) * mm, "end": v(40.5, 9.48) * mm});
            skPoint(sketch, "E12.6.3.1", {"position": v(13, 9.48) * mm});
            skPoint(sketch, "E12.6.3.2", {"position": v(13, 14.48) * mm});
            skLineSegment(sketch, "E12.6.3.3", {"start": v(15.5, 14.48) * mm, "end": v(40.5, 14.48) * mm});
            skPoint(sketch, "E12.6.3.4", {"position": v(43, 14.48) * mm});
            skPoint(sketch, "E12.6.3.5", {"position": v(43, 9.48) * mm});
            skArc(sketch, "E12.6.3.6", {"start": v(13, 11.98) * mm, "mid": v(13.73, 10.22) * mm, "end": v(15.5, 9.48) * mm});
            skArc(sketch, "E12.6.3.7", {"start": v(40.5, 9.48) * mm, "mid": v(42.26, 10.22) * mm, "end": v(43, 11.98) * mm});
            skArc(sketch, "E12.6.3.8", {"start": v(15.5, 14.48) * mm, "mid": v(13.73, 13.75) * mm, "end": v(13, 11.98) * mm});
            skArc(sketch, "E12.6.3.9", {"start": v(43, 11.98) * mm, "mid": v(42.26, 13.75) * mm, "end": v(40.5, 14.48) * mm});
            skLineSegment(sketch, "E12.6.4.0", {"start": v(15.5, 29.48) * mm, "end": v(40.5, 29.48) * mm});
            skPoint(sketch, "E12.6.4.1", {"position": v(13, 29.48) * mm});
            skPoint(sketch, "E12.6.4.2", {"position": v(13, 34.48) * mm});
            skLineSegment(sketch, "E12.6.4.3", {"start": v(15.5, 34.48) * mm, "end": v(40.5, 34.48) * mm});
            skPoint(sketch, "E12.6.4.4", {"position": v(43, 34.48) * mm});
            skPoint(sketch, "E12.6.4.5", {"position": v(43, 29.48) * mm});
            skArc(sketch, "E12.6.4.6", {"start": v(13, 31.98) * mm, "mid": v(13.73, 30.22) * mm, "end": v(15.5, 29.48) * mm});
            skArc(sketch, "E12.6.4.7", {"start": v(40.5, 29.48) * mm, "mid": v(42.26, 30.22) * mm, "end": v(43, 31.98) * mm});
            skArc(sketch, "E12.6.4.8", {"start": v(15.5, 34.48) * mm, "mid": v(13.73, 33.75) * mm, "end": v(13, 31.98) * mm});
            skArc(sketch, "E12.6.4.9", {"start": v(43, 31.98) * mm, "mid": v(42.26, 33.75) * mm, "end": v(40.5, 34.48) * mm});
            skLineSegment(sketch, "E12.6.5.0", {"start": v(15.5, 49.48) * mm, "end": v(40.5, 49.48) * mm});
            skPoint(sketch, "E12.6.5.1", {"position": v(13, 49.48) * mm});
            skPoint(sketch, "E12.6.5.2", {"position": v(13, 54.48) * mm});
            skLineSegment(sketch, "E12.6.5.3", {"start": v(15.5, 54.48) * mm, "end": v(40.5, 54.48) * mm});
            skPoint(sketch, "E12.6.5.4", {"position": v(43, 54.48) * mm});
            skPoint(sketch, "E12.6.5.5", {"position": v(43, 49.48) * mm});
            skArc(sketch, "E12.6.5.6", {"start": v(13, 51.98) * mm, "mid": v(13.73, 50.22) * mm, "end": v(15.5, 49.48) * mm});
            skArc(sketch, "E12.6.5.7", {"start": v(40.5, 49.48) * mm, "mid": v(42.26, 50.22) * mm, "end": v(43, 51.98) * mm});
            skArc(sketch, "E12.6.5.8", {"start": v(15.5, 54.48) * mm, "mid": v(13.73, 53.75) * mm, "end": v(13, 51.98) * mm});
            skArc(sketch, "E12.6.5.9", {"start": v(43, 51.98) * mm, "mid": v(42.26, 53.75) * mm, "end": v(40.5, 54.48) * mm});
            skLineSegment(sketch, "E12.7.0.0", {"start": v(50.5, -50.52) * mm, "end": v(75.5, -50.52) * mm});
            skPoint(sketch, "E12.7.0.1", {"position": v(48, -50.52) * mm});
            skPoint(sketch, "E12.7.0.2", {"position": v(48, -45.52) * mm});
            skLineSegment(sketch, "E12.7.0.3", {"start": v(50.5, -45.52) * mm, "end": v(75.5, -45.52) * mm});
            skPoint(sketch, "E12.7.0.4", {"position": v(78, -45.52) * mm});
            skPoint(sketch, "E12.7.0.5", {"position": v(78, -50.52) * mm});
            skArc(sketch, "E12.7.0.6", {"start": v(48, -48.02) * mm, "mid": v(48.73, -49.78) * mm, "end": v(50.5, -50.52) * mm});
            skArc(sketch, "E12.7.0.7", {"start": v(75.5, -50.52) * mm, "mid": v(77.26, -49.78) * mm, "end": v(78, -48.02) * mm});
            skArc(sketch, "E12.7.0.8", {"start": v(50.5, -45.52) * mm, "mid": v(48.73, -46.25) * mm, "end": v(48, -48.02) * mm});
            skArc(sketch, "E12.7.0.9", {"start": v(78, -48.02) * mm, "mid": v(77.26, -46.25) * mm, "end": v(75.5, -45.52) * mm});
            skLineSegment(sketch, "E12.7.1.0", {"start": v(50.5, -30.52) * mm, "end": v(75.5, -30.52) * mm});
            skPoint(sketch, "E12.7.1.1", {"position": v(48, -30.52) * mm});
            skPoint(sketch, "E12.7.1.2", {"position": v(48, -25.52) * mm});
            skLineSegment(sketch, "E12.7.1.3", {"start": v(50.5, -25.52) * mm, "end": v(75.5, -25.52) * mm});
            skPoint(sketch, "E12.7.1.4", {"position": v(78, -25.52) * mm});
            skPoint(sketch, "E12.7.1.5", {"position": v(78, -30.52) * mm});
            skArc(sketch, "E12.7.1.6", {"start": v(48, -28.02) * mm, "mid": v(48.73, -29.78) * mm, "end": v(50.5, -30.52) * mm});
            skArc(sketch, "E12.7.1.7", {"start": v(75.5, -30.52) * mm, "mid": v(77.26, -29.78) * mm, "end": v(78, -28.02) * mm});
            skArc(sketch, "E12.7.1.8", {"start": v(50.5, -25.52) * mm, "mid": v(48.73, -26.25) * mm, "end": v(48, -28.02) * mm});
            skArc(sketch, "E12.7.1.9", {"start": v(78, -28.02) * mm, "mid": v(77.26, -26.25) * mm, "end": v(75.5, -25.52) * mm});
            skLineSegment(sketch, "E12.7.2.0", {"start": v(50.5, -10.52) * mm, "end": v(75.5, -10.52) * mm});
            skPoint(sketch, "E12.7.2.1", {"position": v(48, -10.52) * mm});
            skPoint(sketch, "E12.7.2.2", {"position": v(48, -5.52) * mm});
            skLineSegment(sketch, "E12.7.2.3", {"start": v(50.5, -5.52) * mm, "end": v(75.5, -5.52) * mm});
            skPoint(sketch, "E12.7.2.4", {"position": v(78, -5.52) * mm});
            skPoint(sketch, "E12.7.2.5", {"position": v(78, -10.52) * mm});
            skArc(sketch, "E12.7.2.6", {"start": v(48, -8.02) * mm, "mid": v(48.73, -9.78) * mm, "end": v(50.5, -10.52) * mm});
            skArc(sketch, "E12.7.2.7", {"start": v(75.5, -10.52) * mm, "mid": v(77.26, -9.78) * mm, "end": v(78, -8.02) * mm});
            skArc(sketch, "E12.7.2.8", {"start": v(50.5, -5.52) * mm, "mid": v(48.73, -6.25) * mm, "end": v(48, -8.02) * mm});
            skArc(sketch, "E12.7.2.9", {"start": v(78, -8.02) * mm, "mid": v(77.26, -6.25) * mm, "end": v(75.5, -5.52) * mm});
            skLineSegment(sketch, "E12.7.3.0", {"start": v(50.5, 9.48) * mm, "end": v(75.5, 9.48) * mm});
            skPoint(sketch, "E12.7.3.1", {"position": v(48, 9.48) * mm});
            skPoint(sketch, "E12.7.3.2", {"position": v(48, 14.48) * mm});
            skLineSegment(sketch, "E12.7.3.3", {"start": v(50.5, 14.48) * mm, "end": v(75.5, 14.48) * mm});
            skPoint(sketch, "E12.7.3.4", {"position": v(78, 14.48) * mm});
            skPoint(sketch, "E12.7.3.5", {"position": v(78, 9.48) * mm});
            skArc(sketch, "E12.7.3.6", {"start": v(48, 11.98) * mm, "mid": v(48.73, 10.22) * mm, "end": v(50.5, 9.48) * mm});
            skArc(sketch, "E12.7.3.7", {"start": v(75.5, 9.48) * mm, "mid": v(77.26, 10.22) * mm, "end": v(78, 11.98) * mm});
            skArc(sketch, "E12.7.3.8", {"start": v(50.5, 14.48) * mm, "mid": v(48.73, 13.75) * mm, "end": v(48, 11.98) * mm});
            skArc(sketch, "E12.7.3.9", {"start": v(78, 11.98) * mm, "mid": v(77.26, 13.75) * mm, "end": v(75.5, 14.48) * mm});
            skLineSegment(sketch, "E12.7.4.0", {"start": v(50.5, 29.48) * mm, "end": v(75.5, 29.48) * mm});
            skPoint(sketch, "E12.7.4.1", {"position": v(48, 29.48) * mm});
            skPoint(sketch, "E12.7.4.2", {"position": v(48, 34.48) * mm});
            skLineSegment(sketch, "E12.7.4.3", {"start": v(50.5, 34.48) * mm, "end": v(75.5, 34.48) * mm});
            skPoint(sketch, "E12.7.4.4", {"position": v(78, 34.48) * mm});
            skPoint(sketch, "E12.7.4.5", {"position": v(78, 29.48) * mm});
            skArc(sketch, "E12.7.4.6", {"start": v(48, 31.98) * mm, "mid": v(48.73, 30.22) * mm, "end": v(50.5, 29.48) * mm});
            skArc(sketch, "E12.7.4.7", {"start": v(75.5, 29.48) * mm, "mid": v(77.26, 30.22) * mm, "end": v(78, 31.98) * mm});
            skArc(sketch, "E12.7.4.8", {"start": v(50.5, 34.48) * mm, "mid": v(48.73, 33.75) * mm, "end": v(48, 31.98) * mm});
            skArc(sketch, "E12.7.4.9", {"start": v(78, 31.98) * mm, "mid": v(77.26, 33.75) * mm, "end": v(75.5, 34.48) * mm});
            skLineSegment(sketch, "E12.7.5.0", {"start": v(50.5, 49.48) * mm, "end": v(75.5, 49.48) * mm});
            skPoint(sketch, "E12.7.5.1", {"position": v(48, 49.48) * mm});
            skPoint(sketch, "E12.7.5.2", {"position": v(48, 54.48) * mm});
            skLineSegment(sketch, "E12.7.5.3", {"start": v(50.5, 54.48) * mm, "end": v(75.5, 54.48) * mm});
            skPoint(sketch, "E12.7.5.4", {"position": v(78, 54.48) * mm});
            skPoint(sketch, "E12.7.5.5", {"position": v(78, 49.48) * mm});
            skArc(sketch, "E12.7.5.6", {"start": v(48, 51.98) * mm, "mid": v(48.73, 50.22) * mm, "end": v(50.5, 49.48) * mm});
            skArc(sketch, "E12.7.5.7", {"start": v(75.5, 49.48) * mm, "mid": v(77.26, 50.22) * mm, "end": v(78, 51.98) * mm});
            skArc(sketch, "E12.7.5.8", {"start": v(50.5, 54.48) * mm, "mid": v(48.73, 53.75) * mm, "end": v(48, 51.98) * mm});
            skArc(sketch, "E12.7.5.9", {"start": v(78, 51.98) * mm, "mid": v(77.26, 53.75) * mm, "end": v(75.5, 54.48) * mm});
            skLineSegment(sketch, "E12.8.0.0", {"start": v(85.5, -50.52) * mm, "end": v(110.5, -50.52) * mm});
            skPoint(sketch, "E12.8.0.1", {"position": v(83, -50.52) * mm});
            skPoint(sketch, "E12.8.0.2", {"position": v(83, -45.52) * mm});
            skLineSegment(sketch, "E12.8.0.3", {"start": v(85.5, -45.52) * mm, "end": v(110.5, -45.52) * mm});
            skPoint(sketch, "E12.8.0.4", {"position": v(113, -45.52) * mm});
            skPoint(sketch, "E12.8.0.5", {"position": v(113, -50.52) * mm});
            skArc(sketch, "E12.8.0.6", {"start": v(83, -48.02) * mm, "mid": v(83.73, -49.78) * mm, "end": v(85.5, -50.52) * mm});
            skArc(sketch, "E12.8.0.7", {"start": v(110.5, -50.52) * mm, "mid": v(112.26, -49.78) * mm, "end": v(113, -48.02) * mm});
            skArc(sketch, "E12.8.0.8", {"start": v(85.5, -45.52) * mm, "mid": v(83.73, -46.25) * mm, "end": v(83, -48.02) * mm});
            skArc(sketch, "E12.8.0.9", {"start": v(113, -48.02) * mm, "mid": v(112.26, -46.25) * mm, "end": v(110.5, -45.52) * mm});
            skLineSegment(sketch, "E12.8.1.0", {"start": v(85.5, -30.52) * mm, "end": v(110.5, -30.52) * mm});
            skPoint(sketch, "E12.8.1.1", {"position": v(83, -30.52) * mm});
            skPoint(sketch, "E12.8.1.2", {"position": v(83, -25.52) * mm});
            skLineSegment(sketch, "E12.8.1.3", {"start": v(85.5, -25.52) * mm, "end": v(110.5, -25.52) * mm});
            skPoint(sketch, "E12.8.1.4", {"position": v(113, -25.52) * mm});
            skPoint(sketch, "E12.8.1.5", {"position": v(113, -30.52) * mm});
            skArc(sketch, "E12.8.1.6", {"start": v(83, -28.02) * mm, "mid": v(83.73, -29.78) * mm, "end": v(85.5, -30.52) * mm});
            skArc(sketch, "E12.8.1.7", {"start": v(110.5, -30.52) * mm, "mid": v(112.26, -29.78) * mm, "end": v(113, -28.02) * mm});
            skArc(sketch, "E12.8.1.8", {"start": v(85.5, -25.52) * mm, "mid": v(83.73, -26.25) * mm, "end": v(83, -28.02) * mm});
            skArc(sketch, "E12.8.1.9", {"start": v(113, -28.02) * mm, "mid": v(112.26, -26.25) * mm, "end": v(110.5, -25.52) * mm});
            skLineSegment(sketch, "E12.8.2.0", {"start": v(85.5, -10.52) * mm, "end": v(110.5, -10.52) * mm});
            skPoint(sketch, "E12.8.2.1", {"position": v(83, -10.52) * mm});
            skPoint(sketch, "E12.8.2.2", {"position": v(83, -5.52) * mm});
            skLineSegment(sketch, "E12.8.2.3", {"start": v(85.5, -5.52) * mm, "end": v(110.5, -5.52) * mm});
            skPoint(sketch, "E12.8.2.4", {"position": v(113, -5.52) * mm});
            skPoint(sketch, "E12.8.2.5", {"position": v(113, -10.52) * mm});
            skArc(sketch, "E12.8.2.6", {"start": v(83, -8.02) * mm, "mid": v(83.73, -9.78) * mm, "end": v(85.5, -10.52) * mm});
            skArc(sketch, "E12.8.2.7", {"start": v(110.5, -10.52) * mm, "mid": v(112.26, -9.78) * mm, "end": v(113, -8.02) * mm});
            skArc(sketch, "E12.8.2.8", {"start": v(85.5, -5.52) * mm, "mid": v(83.73, -6.25) * mm, "end": v(83, -8.02) * mm});
            skArc(sketch, "E12.8.2.9", {"start": v(113, -8.02) * mm, "mid": v(112.26, -6.25) * mm, "end": v(110.5, -5.52) * mm});
            skLineSegment(sketch, "E12.8.3.0", {"start": v(85.5, 9.48) * mm, "end": v(110.5, 9.48) * mm});
            skPoint(sketch, "E12.8.3.1", {"position": v(83, 9.48) * mm});
            skPoint(sketch, "E12.8.3.2", {"position": v(83, 14.48) * mm});
            skLineSegment(sketch, "E12.8.3.3", {"start": v(85.5, 14.48) * mm, "end": v(110.5, 14.48) * mm});
            skPoint(sketch, "E12.8.3.4", {"position": v(113, 14.48) * mm});
            skPoint(sketch, "E12.8.3.5", {"position": v(113, 9.48) * mm});
            skArc(sketch, "E12.8.3.6", {"start": v(83, 11.98) * mm, "mid": v(83.73, 10.22) * mm, "end": v(85.5, 9.48) * mm});
            skArc(sketch, "E12.8.3.7", {"start": v(110.5, 9.48) * mm, "mid": v(112.26, 10.22) * mm, "end": v(113, 11.98) * mm});
            skArc(sketch, "E12.8.3.8", {"start": v(85.5, 14.48) * mm, "mid": v(83.73, 13.75) * mm, "end": v(83, 11.98) * mm});
            skArc(sketch, "E12.8.3.9", {"start": v(113, 11.98) * mm, "mid": v(112.26, 13.75) * mm, "end": v(110.5, 14.48) * mm});
            skLineSegment(sketch, "E12.8.4.0", {"start": v(85.5, 29.48) * mm, "end": v(110.5, 29.48) * mm});
            skPoint(sketch, "E12.8.4.1", {"position": v(83, 29.48) * mm});
            skPoint(sketch, "E12.8.4.2", {"position": v(83, 34.48) * mm});
            skLineSegment(sketch, "E12.8.4.3", {"start": v(85.5, 34.48) * mm, "end": v(110.5, 34.48) * mm});
            skPoint(sketch, "E12.8.4.4", {"position": v(113, 34.48) * mm});
            skPoint(sketch, "E12.8.4.5", {"position": v(113, 29.48) * mm});
            skArc(sketch, "E12.8.4.6", {"start": v(83, 31.98) * mm, "mid": v(83.73, 30.22) * mm, "end": v(85.5, 29.48) * mm});
            skArc(sketch, "E12.8.4.7", {"start": v(110.5, 29.48) * mm, "mid": v(112.26, 30.22) * mm, "end": v(113, 31.98) * mm});
            skArc(sketch, "E12.8.4.8", {"start": v(85.5, 34.48) * mm, "mid": v(83.73, 33.75) * mm, "end": v(83, 31.98) * mm});
            skArc(sketch, "E12.8.4.9", {"start": v(113, 31.98) * mm, "mid": v(112.26, 33.75) * mm, "end": v(110.5, 34.48) * mm});
            skLineSegment(sketch, "E12.8.5.0", {"start": v(85.5, 49.48) * mm, "end": v(110.5, 49.48) * mm});
            skPoint(sketch, "E12.8.5.1", {"position": v(83, 49.48) * mm});
            skPoint(sketch, "E12.8.5.2", {"position": v(83, 54.48) * mm});
            skLineSegment(sketch, "E12.8.5.3", {"start": v(85.5, 54.48) * mm, "end": v(110.5, 54.48) * mm});
            skPoint(sketch, "E12.8.5.4", {"position": v(113, 54.48) * mm});
            skPoint(sketch, "E12.8.5.5", {"position": v(113, 49.48) * mm});
            skArc(sketch, "E12.8.5.6", {"start": v(83, 51.98) * mm, "mid": v(83.73, 50.22) * mm, "end": v(85.5, 49.48) * mm});
            skArc(sketch, "E12.8.5.7", {"start": v(110.5, 49.48) * mm, "mid": v(112.26, 50.22) * mm, "end": v(113, 51.98) * mm});
            skArc(sketch, "E12.8.5.8", {"start": v(85.5, 54.48) * mm, "mid": v(83.73, 53.75) * mm, "end": v(83, 51.98) * mm});
            skArc(sketch, "E12.8.5.9", {"start": v(113, 51.98) * mm, "mid": v(112.26, 53.75) * mm, "end": v(110.5, 54.48) * mm});
            skLineSegment(sketch, "E12.9.0.0", {"start": v(120.5, -50.52) * mm, "end": v(145.5, -50.52) * mm});
            skPoint(sketch, "E12.9.0.1", {"position": v(118, -50.52) * mm});
            skPoint(sketch, "E12.9.0.2", {"position": v(118, -45.52) * mm});
            skLineSegment(sketch, "E12.9.0.3", {"start": v(120.5, -45.52) * mm, "end": v(145.5, -45.52) * mm});
            skPoint(sketch, "E12.9.0.4", {"position": v(148, -45.52) * mm});
            skPoint(sketch, "E12.9.0.5", {"position": v(148, -50.52) * mm});
            skArc(sketch, "E12.9.0.6", {"start": v(118, -48.02) * mm, "mid": v(118.73, -49.78) * mm, "end": v(120.5, -50.52) * mm});
            skArc(sketch, "E12.9.0.7", {"start": v(145.5, -50.52) * mm, "mid": v(147.26, -49.78) * mm, "end": v(148, -48.02) * mm});
            skArc(sketch, "E12.9.0.8", {"start": v(120.5, -45.52) * mm, "mid": v(118.73, -46.25) * mm, "end": v(118, -48.02) * mm});
            skArc(sketch, "E12.9.0.9", {"start": v(148, -48.02) * mm, "mid": v(147.26, -46.25) * mm, "end": v(145.5, -45.52) * mm});
            skLineSegment(sketch, "E12.9.1.0", {"start": v(120.5, -30.52) * mm, "end": v(145.5, -30.52) * mm});
            skPoint(sketch, "E12.9.1.1", {"position": v(118, -30.52) * mm});
            skPoint(sketch, "E12.9.1.2", {"position": v(118, -25.52) * mm});
            skLineSegment(sketch, "E12.9.1.3", {"start": v(120.5, -25.52) * mm, "end": v(145.5, -25.52) * mm});
            skPoint(sketch, "E12.9.1.4", {"position": v(148, -25.52) * mm});
            skPoint(sketch, "E12.9.1.5", {"position": v(148, -30.52) * mm});
            skArc(sketch, "E12.9.1.6", {"start": v(118, -28.02) * mm, "mid": v(118.73, -29.78) * mm, "end": v(120.5, -30.52) * mm});
            skArc(sketch, "E12.9.1.7", {"start": v(145.5, -30.52) * mm, "mid": v(147.26, -29.78) * mm, "end": v(148, -28.02) * mm});
            skArc(sketch, "E12.9.1.8", {"start": v(120.5, -25.52) * mm, "mid": v(118.73, -26.25) * mm, "end": v(118, -28.02) * mm});
            skArc(sketch, "E12.9.1.9", {"start": v(148, -28.02) * mm, "mid": v(147.26, -26.25) * mm, "end": v(145.5, -25.52) * mm});
            skLineSegment(sketch, "E12.9.2.0", {"start": v(120.5, -10.52) * mm, "end": v(145.5, -10.52) * mm});
            skPoint(sketch, "E12.9.2.1", {"position": v(118, -10.52) * mm});
            skPoint(sketch, "E12.9.2.2", {"position": v(118, -5.52) * mm});
            skLineSegment(sketch, "E12.9.2.3", {"start": v(120.5, -5.52) * mm, "end": v(145.5, -5.52) * mm});
            skPoint(sketch, "E12.9.2.4", {"position": v(148, -5.52) * mm});
            skPoint(sketch, "E12.9.2.5", {"position": v(148, -10.52) * mm});
            skArc(sketch, "E12.9.2.6", {"start": v(118, -8.02) * mm, "mid": v(118.73, -9.78) * mm, "end": v(120.5, -10.52) * mm});
            skArc(sketch, "E12.9.2.7", {"start": v(145.5, -10.52) * mm, "mid": v(147.26, -9.78) * mm, "end": v(148, -8.02) * mm});
            skArc(sketch, "E12.9.2.8", {"start": v(120.5, -5.52) * mm, "mid": v(118.73, -6.25) * mm, "end": v(118, -8.02) * mm});
            skArc(sketch, "E12.9.2.9", {"start": v(148, -8.02) * mm, "mid": v(147.26, -6.25) * mm, "end": v(145.5, -5.52) * mm});
            skLineSegment(sketch, "E12.9.3.0", {"start": v(120.5, 9.48) * mm, "end": v(145.5, 9.48) * mm});
            skPoint(sketch, "E12.9.3.1", {"position": v(118, 9.48) * mm});
            skPoint(sketch, "E12.9.3.2", {"position": v(118, 14.48) * mm});
            skLineSegment(sketch, "E12.9.3.3", {"start": v(120.5, 14.48) * mm, "end": v(145.5, 14.48) * mm});
            skPoint(sketch, "E12.9.3.4", {"position": v(148, 14.48) * mm});
            skPoint(sketch, "E12.9.3.5", {"position": v(148, 9.48) * mm});
            skArc(sketch, "E12.9.3.6", {"start": v(118, 11.98) * mm, "mid": v(118.73, 10.22) * mm, "end": v(120.5, 9.48) * mm});
            skArc(sketch, "E12.9.3.7", {"start": v(145.5, 9.48) * mm, "mid": v(147.26, 10.22) * mm, "end": v(148, 11.98) * mm});
            skArc(sketch, "E12.9.3.8", {"start": v(120.5, 14.48) * mm, "mid": v(118.73, 13.75) * mm, "end": v(118, 11.98) * mm});
            skArc(sketch, "E12.9.3.9", {"start": v(148, 11.98) * mm, "mid": v(147.26, 13.75) * mm, "end": v(145.5, 14.48) * mm});
            skLineSegment(sketch, "E12.9.4.0", {"start": v(120.5, 29.48) * mm, "end": v(145.5, 29.48) * mm});
            skPoint(sketch, "E12.9.4.1", {"position": v(118, 29.48) * mm});
            skPoint(sketch, "E12.9.4.2", {"position": v(118, 34.48) * mm});
            skLineSegment(sketch, "E12.9.4.3", {"start": v(120.5, 34.48) * mm, "end": v(145.5, 34.48) * mm});
            skPoint(sketch, "E12.9.4.4", {"position": v(148, 34.48) * mm});
            skPoint(sketch, "E12.9.4.5", {"position": v(148, 29.48) * mm});
            skArc(sketch, "E12.9.4.6", {"start": v(118, 31.98) * mm, "mid": v(118.73, 30.22) * mm, "end": v(120.5, 29.48) * mm});
            skArc(sketch, "E12.9.4.7", {"start": v(145.5, 29.48) * mm, "mid": v(147.26, 30.22) * mm, "end": v(148, 31.98) * mm});
            skArc(sketch, "E12.9.4.8", {"start": v(120.5, 34.48) * mm, "mid": v(118.73, 33.75) * mm, "end": v(118, 31.98) * mm});
            skArc(sketch, "E12.9.4.9", {"start": v(148, 31.98) * mm, "mid": v(147.26, 33.75) * mm, "end": v(145.5, 34.48) * mm});
            skLineSegment(sketch, "E12.9.5.0", {"start": v(120.5, 49.48) * mm, "end": v(145.5, 49.48) * mm});
            skPoint(sketch, "E12.9.5.1", {"position": v(118, 49.48) * mm});
            skPoint(sketch, "E12.9.5.2", {"position": v(118, 54.48) * mm});
            skLineSegment(sketch, "E12.9.5.3", {"start": v(120.5, 54.48) * mm, "end": v(145.5, 54.48) * mm});
            skPoint(sketch, "E12.9.5.4", {"position": v(148, 54.48) * mm});
            skPoint(sketch, "E12.9.5.5", {"position": v(148, 49.48) * mm});
            skArc(sketch, "E12.9.5.6", {"start": v(118, 51.98) * mm, "mid": v(118.73, 50.22) * mm, "end": v(120.5, 49.48) * mm});
            skArc(sketch, "E12.9.5.7", {"start": v(145.5, 49.48) * mm, "mid": v(147.26, 50.22) * mm, "end": v(148, 51.98) * mm});
            skArc(sketch, "E12.9.5.8", {"start": v(120.5, 54.48) * mm, "mid": v(118.73, 53.75) * mm, "end": v(118, 51.98) * mm});
            skArc(sketch, "E12.9.5.9", {"start": v(148, 51.98) * mm, "mid": v(147.26, 53.75) * mm, "end": v(145.5, 54.48) * mm});
            skLineSegment(sketch, "E12.10.0.0", {"start": v(155.5, -50.52) * mm, "end": v(180.5, -50.52) * mm});
            skPoint(sketch, "E12.10.0.1", {"position": v(153, -50.52) * mm});
            skPoint(sketch, "E12.10.0.2", {"position": v(153, -45.52) * mm});
            skLineSegment(sketch, "E12.10.0.3", {"start": v(155.5, -45.52) * mm, "end": v(180.5, -45.52) * mm});
            skPoint(sketch, "E12.10.0.4", {"position": v(183, -45.52) * mm});
            skPoint(sketch, "E12.10.0.5", {"position": v(183, -50.52) * mm});
            skArc(sketch, "E12.10.0.6", {"start": v(153, -48.02) * mm, "mid": v(153.73, -49.78) * mm, "end": v(155.5, -50.52) * mm});
            skArc(sketch, "E12.10.0.7", {"start": v(180.5, -50.52) * mm, "mid": v(182.26, -49.78) * mm, "end": v(183, -48.02) * mm});
            skArc(sketch, "E12.10.0.8", {"start": v(155.5, -45.52) * mm, "mid": v(153.73, -46.25) * mm, "end": v(153, -48.02) * mm});
            skArc(sketch, "E12.10.0.9", {"start": v(183, -48.02) * mm, "mid": v(182.26, -46.25) * mm, "end": v(180.5, -45.52) * mm});
            skLineSegment(sketch, "E12.10.1.0", {"start": v(155.5, -30.52) * mm, "end": v(180.5, -30.52) * mm});
            skPoint(sketch, "E12.10.1.1", {"position": v(153, -30.52) * mm});
            skPoint(sketch, "E12.10.1.2", {"position": v(153, -25.52) * mm});
            skLineSegment(sketch, "E12.10.1.3", {"start": v(155.5, -25.52) * mm, "end": v(180.5, -25.52) * mm});
            skPoint(sketch, "E12.10.1.4", {"position": v(183, -25.52) * mm});
            skPoint(sketch, "E12.10.1.5", {"position": v(183, -30.52) * mm});
            skArc(sketch, "E12.10.1.6", {"start": v(153, -28.02) * mm, "mid": v(153.73, -29.78) * mm, "end": v(155.5, -30.52) * mm});
            skArc(sketch, "E12.10.1.7", {"start": v(180.5, -30.52) * mm, "mid": v(182.26, -29.78) * mm, "end": v(183, -28.02) * mm});
            skArc(sketch, "E12.10.1.8", {"start": v(155.5, -25.52) * mm, "mid": v(153.73, -26.25) * mm, "end": v(153, -28.02) * mm});
            skArc(sketch, "E12.10.1.9", {"start": v(183, -28.02) * mm, "mid": v(182.26, -26.25) * mm, "end": v(180.5, -25.52) * mm});
            skLineSegment(sketch, "E12.10.2.0", {"start": v(155.5, -10.52) * mm, "end": v(180.5, -10.52) * mm});
            skPoint(sketch, "E12.10.2.1", {"position": v(153, -10.52) * mm});
            skPoint(sketch, "E12.10.2.2", {"position": v(153, -5.52) * mm});
            skLineSegment(sketch, "E12.10.2.3", {"start": v(155.5, -5.52) * mm, "end": v(180.5, -5.52) * mm});
            skPoint(sketch, "E12.10.2.4", {"position": v(183, -5.52) * mm});
            skPoint(sketch, "E12.10.2.5", {"position": v(183, -10.52) * mm});
            skArc(sketch, "E12.10.2.6", {"start": v(153, -8.02) * mm, "mid": v(153.73, -9.78) * mm, "end": v(155.5, -10.52) * mm});
            skArc(sketch, "E12.10.2.7", {"start": v(180.5, -10.52) * mm, "mid": v(182.26, -9.78) * mm, "end": v(183, -8.02) * mm});
            skArc(sketch, "E12.10.2.8", {"start": v(155.5, -5.52) * mm, "mid": v(153.73, -6.25) * mm, "end": v(153, -8.02) * mm});
            skArc(sketch, "E12.10.2.9", {"start": v(183, -8.02) * mm, "mid": v(182.26, -6.25) * mm, "end": v(180.5, -5.52) * mm});
            skLineSegment(sketch, "E12.10.3.0", {"start": v(155.5, 9.48) * mm, "end": v(180.5, 9.48) * mm});
            skPoint(sketch, "E12.10.3.1", {"position": v(153, 9.48) * mm});
            skPoint(sketch, "E12.10.3.2", {"position": v(153, 14.48) * mm});
            skLineSegment(sketch, "E12.10.3.3", {"start": v(155.5, 14.48) * mm, "end": v(180.5, 14.48) * mm});
            skPoint(sketch, "E12.10.3.4", {"position": v(183, 14.48) * mm});
            skPoint(sketch, "E12.10.3.5", {"position": v(183, 9.48) * mm});
            skArc(sketch, "E12.10.3.6", {"start": v(153, 11.98) * mm, "mid": v(153.73, 10.22) * mm, "end": v(155.5, 9.48) * mm});
            skArc(sketch, "E12.10.3.7", {"start": v(180.5, 9.48) * mm, "mid": v(182.26, 10.22) * mm, "end": v(183, 11.98) * mm});
            skArc(sketch, "E12.10.3.8", {"start": v(155.5, 14.48) * mm, "mid": v(153.73, 13.75) * mm, "end": v(153, 11.98) * mm});
            skArc(sketch, "E12.10.3.9", {"start": v(183, 11.98) * mm, "mid": v(182.26, 13.75) * mm, "end": v(180.5, 14.48) * mm});
            skLineSegment(sketch, "E12.10.4.0", {"start": v(155.5, 29.48) * mm, "end": v(180.5, 29.48) * mm});
            skPoint(sketch, "E12.10.4.1", {"position": v(153, 29.48) * mm});
            skPoint(sketch, "E12.10.4.2", {"position": v(153, 34.48) * mm});
            skLineSegment(sketch, "E12.10.4.3", {"start": v(155.5, 34.48) * mm, "end": v(180.5, 34.48) * mm});
            skPoint(sketch, "E12.10.4.4", {"position": v(183, 34.48) * mm});
            skPoint(sketch, "E12.10.4.5", {"position": v(183, 29.48) * mm});
            skArc(sketch, "E12.10.4.6", {"start": v(153, 31.98) * mm, "mid": v(153.73, 30.22) * mm, "end": v(155.5, 29.48) * mm});
            skArc(sketch, "E12.10.4.7", {"start": v(180.5, 29.48) * mm, "mid": v(182.26, 30.22) * mm, "end": v(183, 31.98) * mm});
            skArc(sketch, "E12.10.4.8", {"start": v(155.5, 34.48) * mm, "mid": v(153.73, 33.75) * mm, "end": v(153, 31.98) * mm});
            skArc(sketch, "E12.10.4.9", {"start": v(183, 31.98) * mm, "mid": v(182.26, 33.75) * mm, "end": v(180.5, 34.48) * mm});
            skLineSegment(sketch, "E12.10.5.0", {"start": v(155.5, 49.48) * mm, "end": v(180.5, 49.48) * mm});
            skPoint(sketch, "E12.10.5.1", {"position": v(153, 49.48) * mm});
            skPoint(sketch, "E12.10.5.2", {"position": v(153, 54.48) * mm});
            skLineSegment(sketch, "E12.10.5.3", {"start": v(155.5, 54.48) * mm, "end": v(180.5, 54.48) * mm});
            skPoint(sketch, "E12.10.5.4", {"position": v(183, 54.48) * mm});
            skPoint(sketch, "E12.10.5.5", {"position": v(183, 49.48) * mm});
            skArc(sketch, "E12.10.5.6", {"start": v(153, 51.98) * mm, "mid": v(153.73, 50.22) * mm, "end": v(155.5, 49.48) * mm});
            skArc(sketch, "E12.10.5.7", {"start": v(180.5, 49.48) * mm, "mid": v(182.26, 50.22) * mm, "end": v(183, 51.98) * mm});
            skArc(sketch, "E12.10.5.8", {"start": v(155.5, 54.48) * mm, "mid": v(153.73, 53.75) * mm, "end": v(153, 51.98) * mm});
            skArc(sketch, "E12.10.5.9", {"start": v(183, 51.98) * mm, "mid": v(182.26, 53.75) * mm, "end": v(180.5, 54.48) * mm});
            skLineSegment(sketch, "E12.11.0.0", {"start": v(190.5, -50.52) * mm, "end": v(215.5, -50.52) * mm});
            skPoint(sketch, "E12.11.0.1", {"position": v(188, -50.52) * mm});
            skPoint(sketch, "E12.11.0.2", {"position": v(188, -45.52) * mm});
            skLineSegment(sketch, "E12.11.0.3", {"start": v(190.5, -45.52) * mm, "end": v(215.5, -45.52) * mm});
            skPoint(sketch, "E12.11.0.4", {"position": v(218, -45.52) * mm});
            skPoint(sketch, "E12.11.0.5", {"position": v(218, -50.52) * mm});
            skArc(sketch, "E12.11.0.6", {"start": v(188, -48.02) * mm, "mid": v(188.73, -49.78) * mm, "end": v(190.5, -50.52) * mm});
            skArc(sketch, "E12.11.0.7", {"start": v(215.5, -50.52) * mm, "mid": v(217.26, -49.78) * mm, "end": v(218, -48.02) * mm});
            skArc(sketch, "E12.11.0.8", {"start": v(190.5, -45.52) * mm, "mid": v(188.73, -46.25) * mm, "end": v(188, -48.02) * mm});
            skArc(sketch, "E12.11.0.9", {"start": v(218, -48.02) * mm, "mid": v(217.26, -46.25) * mm, "end": v(215.5, -45.52) * mm});
            skLineSegment(sketch, "E12.11.1.0", {"start": v(190.5, -30.52) * mm, "end": v(215.5, -30.52) * mm});
            skPoint(sketch, "E12.11.1.1", {"position": v(188, -30.52) * mm});
            skPoint(sketch, "E12.11.1.2", {"position": v(188, -25.52) * mm});
            skLineSegment(sketch, "E12.11.1.3", {"start": v(190.5, -25.52) * mm, "end": v(215.5, -25.52) * mm});
            skPoint(sketch, "E12.11.1.4", {"position": v(218, -25.52) * mm});
            skPoint(sketch, "E12.11.1.5", {"position": v(218, -30.52) * mm});
            skArc(sketch, "E12.11.1.6", {"start": v(188, -28.02) * mm, "mid": v(188.73, -29.78) * mm, "end": v(190.5, -30.52) * mm});
            skArc(sketch, "E12.11.1.7", {"start": v(215.5, -30.52) * mm, "mid": v(217.26, -29.78) * mm, "end": v(218, -28.02) * mm});
            skArc(sketch, "E12.11.1.8", {"start": v(190.5, -25.52) * mm, "mid": v(188.73, -26.25) * mm, "end": v(188, -28.02) * mm});
            skArc(sketch, "E12.11.1.9", {"start": v(218, -28.02) * mm, "mid": v(217.26, -26.25) * mm, "end": v(215.5, -25.52) * mm});
            skLineSegment(sketch, "E12.11.2.0", {"start": v(190.5, -10.52) * mm, "end": v(215.5, -10.52) * mm});
            skPoint(sketch, "E12.11.2.1", {"position": v(188, -10.52) * mm});
            skPoint(sketch, "E12.11.2.2", {"position": v(188, -5.52) * mm});
            skLineSegment(sketch, "E12.11.2.3", {"start": v(190.5, -5.52) * mm, "end": v(215.5, -5.52) * mm});
            skPoint(sketch, "E12.11.2.4", {"position": v(218, -5.52) * mm});
            skPoint(sketch, "E12.11.2.5", {"position": v(218, -10.52) * mm});
            skArc(sketch, "E12.11.2.6", {"start": v(188, -8.02) * mm, "mid": v(188.73, -9.78) * mm, "end": v(190.5, -10.52) * mm});
            skArc(sketch, "E12.11.2.7", {"start": v(215.5, -10.52) * mm, "mid": v(217.26, -9.78) * mm, "end": v(218, -8.02) * mm});
            skArc(sketch, "E12.11.2.8", {"start": v(190.5, -5.52) * mm, "mid": v(188.73, -6.25) * mm, "end": v(188, -8.02) * mm});
            skArc(sketch, "E12.11.2.9", {"start": v(218, -8.02) * mm, "mid": v(217.26, -6.25) * mm, "end": v(215.5, -5.52) * mm});
            skLineSegment(sketch, "E12.11.3.0", {"start": v(190.5, 9.48) * mm, "end": v(215.5, 9.48) * mm});
            skPoint(sketch, "E12.11.3.1", {"position": v(188, 9.48) * mm});
            skPoint(sketch, "E12.11.3.2", {"position": v(188, 14.48) * mm});
            skLineSegment(sketch, "E12.11.3.3", {"start": v(190.5, 14.48) * mm, "end": v(215.5, 14.48) * mm});
            skPoint(sketch, "E12.11.3.4", {"position": v(218, 14.48) * mm});
            skPoint(sketch, "E12.11.3.5", {"position": v(218, 9.48) * mm});
            skArc(sketch, "E12.11.3.6", {"start": v(188, 11.98) * mm, "mid": v(188.73, 10.22) * mm, "end": v(190.5, 9.48) * mm});
            skArc(sketch, "E12.11.3.7", {"start": v(215.5, 9.48) * mm, "mid": v(217.26, 10.22) * mm, "end": v(218, 11.98) * mm});
            skArc(sketch, "E12.11.3.8", {"start": v(190.5, 14.48) * mm, "mid": v(188.73, 13.75) * mm, "end": v(188, 11.98) * mm});
            skArc(sketch, "E12.11.3.9", {"start": v(218, 11.98) * mm, "mid": v(217.26, 13.75) * mm, "end": v(215.5, 14.48) * mm});
            skLineSegment(sketch, "E12.11.4.0", {"start": v(190.5, 29.48) * mm, "end": v(215.5, 29.48) * mm});
            skPoint(sketch, "E12.11.4.1", {"position": v(188, 29.48) * mm});
            skPoint(sketch, "E12.11.4.2", {"position": v(188, 34.48) * mm});
            skLineSegment(sketch, "E12.11.4.3", {"start": v(190.5, 34.48) * mm, "end": v(215.5, 34.48) * mm});
            skPoint(sketch, "E12.11.4.4", {"position": v(218, 34.48) * mm});
            skPoint(sketch, "E12.11.4.5", {"position": v(218, 29.48) * mm});
            skArc(sketch, "E12.11.4.6", {"start": v(188, 31.98) * mm, "mid": v(188.73, 30.22) * mm, "end": v(190.5, 29.48) * mm});
            skArc(sketch, "E12.11.4.7", {"start": v(215.5, 29.48) * mm, "mid": v(217.26, 30.22) * mm, "end": v(218, 31.98) * mm});
            skArc(sketch, "E12.11.4.8", {"start": v(190.5, 34.48) * mm, "mid": v(188.73, 33.75) * mm, "end": v(188, 31.98) * mm});
            skArc(sketch, "E12.11.4.9", {"start": v(218, 31.98) * mm, "mid": v(217.26, 33.75) * mm, "end": v(215.5, 34.48) * mm});
            skLineSegment(sketch, "E12.11.5.0", {"start": v(190.5, 49.48) * mm, "end": v(215.5, 49.48) * mm});
            skPoint(sketch, "E12.11.5.1", {"position": v(188, 49.48) * mm});
            skPoint(sketch, "E12.11.5.2", {"position": v(188, 54.48) * mm});
            skLineSegment(sketch, "E12.11.5.3", {"start": v(190.5, 54.48) * mm, "end": v(215.5, 54.48) * mm});
            skPoint(sketch, "E12.11.5.4", {"position": v(218, 54.48) * mm});
            skPoint(sketch, "E12.11.5.5", {"position": v(218, 49.48) * mm});
            skArc(sketch, "E12.11.5.6", {"start": v(188, 51.98) * mm, "mid": v(188.73, 50.22) * mm, "end": v(190.5, 49.48) * mm});
            skArc(sketch, "E12.11.5.7", {"start": v(215.5, 49.48) * mm, "mid": v(217.26, 50.22) * mm, "end": v(218, 51.98) * mm});
            skArc(sketch, "E12.11.5.8", {"start": v(190.5, 54.48) * mm, "mid": v(188.73, 53.75) * mm, "end": v(188, 51.98) * mm});
            skArc(sketch, "E12.11.5.9", {"start": v(218, 51.98) * mm, "mid": v(217.26, 53.75) * mm, "end": v(215.5, 54.48) * mm});
            skLineSegment(sketch, "E12.12.0.0", {"start": v(225.5, -50.52) * mm, "end": v(250.5, -50.52) * mm});
            skPoint(sketch, "E12.12.0.1", {"position": v(223, -50.52) * mm});
            skPoint(sketch, "E12.12.0.2", {"position": v(223, -45.52) * mm});
            skLineSegment(sketch, "E12.12.0.3", {"start": v(225.5, -45.52) * mm, "end": v(250.5, -45.52) * mm});
            skPoint(sketch, "E12.12.0.4", {"position": v(253, -45.52) * mm});
            skPoint(sketch, "E12.12.0.5", {"position": v(253, -50.52) * mm});
            skArc(sketch, "E12.12.0.6", {"start": v(223, -48.02) * mm, "mid": v(223.73, -49.78) * mm, "end": v(225.5, -50.52) * mm});
            skArc(sketch, "E12.12.0.7", {"start": v(250.5, -50.52) * mm, "mid": v(252.26, -49.78) * mm, "end": v(253, -48.02) * mm});
            skArc(sketch, "E12.12.0.8", {"start": v(225.5, -45.52) * mm, "mid": v(223.73, -46.25) * mm, "end": v(223, -48.02) * mm});
            skArc(sketch, "E12.12.0.9", {"start": v(253, -48.02) * mm, "mid": v(252.26, -46.25) * mm, "end": v(250.5, -45.52) * mm});
            skLineSegment(sketch, "E12.12.1.0", {"start": v(225.5, -30.52) * mm, "end": v(250.5, -30.52) * mm});
            skPoint(sketch, "E12.12.1.1", {"position": v(223, -30.52) * mm});
            skPoint(sketch, "E12.12.1.2", {"position": v(223, -25.52) * mm});
            skLineSegment(sketch, "E12.12.1.3", {"start": v(225.5, -25.52) * mm, "end": v(250.5, -25.52) * mm});
            skPoint(sketch, "E12.12.1.4", {"position": v(253, -25.52) * mm});
            skPoint(sketch, "E12.12.1.5", {"position": v(253, -30.52) * mm});
            skArc(sketch, "E12.12.1.6", {"start": v(223, -28.02) * mm, "mid": v(223.73, -29.78) * mm, "end": v(225.5, -30.52) * mm});
            skArc(sketch, "E12.12.1.7", {"start": v(250.5, -30.52) * mm, "mid": v(252.26, -29.78) * mm, "end": v(253, -28.02) * mm});
            skArc(sketch, "E12.12.1.8", {"start": v(225.5, -25.52) * mm, "mid": v(223.73, -26.25) * mm, "end": v(223, -28.02) * mm});
            skArc(sketch, "E12.12.1.9", {"start": v(253, -28.02) * mm, "mid": v(252.26, -26.25) * mm, "end": v(250.5, -25.52) * mm});
            skLineSegment(sketch, "E12.12.2.0", {"start": v(225.5, -10.52) * mm, "end": v(250.5, -10.52) * mm});
            skPoint(sketch, "E12.12.2.1", {"position": v(223, -10.52) * mm});
            skPoint(sketch, "E12.12.2.2", {"position": v(223, -5.52) * mm});
            skLineSegment(sketch, "E12.12.2.3", {"start": v(225.5, -5.52) * mm, "end": v(250.5, -5.52) * mm});
            skPoint(sketch, "E12.12.2.4", {"position": v(253, -5.52) * mm});
            skPoint(sketch, "E12.12.2.5", {"position": v(253, -10.52) * mm});
            skArc(sketch, "E12.12.2.6", {"start": v(223, -8.02) * mm, "mid": v(223.73, -9.78) * mm, "end": v(225.5, -10.52) * mm});
            skArc(sketch, "E12.12.2.7", {"start": v(250.5, -10.52) * mm, "mid": v(252.26, -9.78) * mm, "end": v(253, -8.02) * mm});
            skArc(sketch, "E12.12.2.8", {"start": v(225.5, -5.52) * mm, "mid": v(223.73, -6.25) * mm, "end": v(223, -8.02) * mm});
            skArc(sketch, "E12.12.2.9", {"start": v(253, -8.02) * mm, "mid": v(252.26, -6.25) * mm, "end": v(250.5, -5.52) * mm});
            skLineSegment(sketch, "E12.12.3.0", {"start": v(225.5, 9.48) * mm, "end": v(250.5, 9.48) * mm});
            skPoint(sketch, "E12.12.3.1", {"position": v(223, 9.48) * mm});
            skPoint(sketch, "E12.12.3.2", {"position": v(223, 14.48) * mm});
            skLineSegment(sketch, "E12.12.3.3", {"start": v(225.5, 14.48) * mm, "end": v(250.5, 14.48) * mm});
            skPoint(sketch, "E12.12.3.4", {"position": v(253, 14.48) * mm});
            skPoint(sketch, "E12.12.3.5", {"position": v(253, 9.48) * mm});
            skArc(sketch, "E12.12.3.6", {"start": v(223, 11.98) * mm, "mid": v(223.73, 10.22) * mm, "end": v(225.5, 9.48) * mm});
            skArc(sketch, "E12.12.3.7", {"start": v(250.5, 9.48) * mm, "mid": v(252.26, 10.22) * mm, "end": v(253, 11.98) * mm});
            skArc(sketch, "E12.12.3.8", {"start": v(225.5, 14.48) * mm, "mid": v(223.73, 13.75) * mm, "end": v(223, 11.98) * mm});
            skArc(sketch, "E12.12.3.9", {"start": v(253, 11.98) * mm, "mid": v(252.26, 13.75) * mm, "end": v(250.5, 14.48) * mm});
            skLineSegment(sketch, "E12.12.4.0", {"start": v(225.5, 29.48) * mm, "end": v(250.5, 29.48) * mm});
            skPoint(sketch, "E12.12.4.1", {"position": v(223, 29.48) * mm});
            skPoint(sketch, "E12.12.4.2", {"position": v(223, 34.48) * mm});
            skLineSegment(sketch, "E12.12.4.3", {"start": v(225.5, 34.48) * mm, "end": v(250.5, 34.48) * mm});
            skPoint(sketch, "E12.12.4.4", {"position": v(253, 34.48) * mm});
            skPoint(sketch, "E12.12.4.5", {"position": v(253, 29.48) * mm});
            skArc(sketch, "E12.12.4.6", {"start": v(223, 31.98) * mm, "mid": v(223.73, 30.22) * mm, "end": v(225.5, 29.48) * mm});
            skArc(sketch, "E12.12.4.7", {"start": v(250.5, 29.48) * mm, "mid": v(252.26, 30.22) * mm, "end": v(253, 31.98) * mm});
            skArc(sketch, "E12.12.4.8", {"start": v(225.5, 34.48) * mm, "mid": v(223.73, 33.75) * mm, "end": v(223, 31.98) * mm});
            skArc(sketch, "E12.12.4.9", {"start": v(253, 31.98) * mm, "mid": v(252.26, 33.75) * mm, "end": v(250.5, 34.48) * mm});
            skLineSegment(sketch, "E12.12.5.0", {"start": v(225.5, 49.48) * mm, "end": v(250.5, 49.48) * mm});
            skPoint(sketch, "E12.12.5.1", {"position": v(223, 49.48) * mm});
            skPoint(sketch, "E12.12.5.2", {"position": v(223, 54.48) * mm});
            skLineSegment(sketch, "E12.12.5.3", {"start": v(225.5, 54.48) * mm, "end": v(250.5, 54.48) * mm});
            skPoint(sketch, "E12.12.5.4", {"position": v(253, 54.48) * mm});
            skPoint(sketch, "E12.12.5.5", {"position": v(253, 49.48) * mm});
            skArc(sketch, "E12.12.5.6", {"start": v(223, 51.98) * mm, "mid": v(223.73, 50.22) * mm, "end": v(225.5, 49.48) * mm});
            skArc(sketch, "E12.12.5.7", {"start": v(250.5, 49.48) * mm, "mid": v(252.26, 50.22) * mm, "end": v(253, 51.98) * mm});
            skArc(sketch, "E12.12.5.8", {"start": v(225.5, 54.48) * mm, "mid": v(223.73, 53.75) * mm, "end": v(223, 51.98) * mm});
            skArc(sketch, "E12.12.5.9", {"start": v(253, 51.98) * mm, "mid": v(252.26, 53.75) * mm, "end": v(250.5, 54.48) * mm});
            skLineSegment(sketch, "E12.13.0.0", {"start": v(260.5, -50.52) * mm, "end": v(285.5, -50.52) * mm});
            skPoint(sketch, "E12.13.0.1", {"position": v(258, -50.52) * mm});
            skPoint(sketch, "E12.13.0.2", {"position": v(258, -45.52) * mm});
            skLineSegment(sketch, "E12.13.0.3", {"start": v(260.5, -45.52) * mm, "end": v(285.5, -45.52) * mm});
            skPoint(sketch, "E12.13.0.4", {"position": v(288, -45.52) * mm});
            skPoint(sketch, "E12.13.0.5", {"position": v(288, -50.52) * mm});
            skArc(sketch, "E12.13.0.6", {"start": v(258, -48.02) * mm, "mid": v(258.73, -49.78) * mm, "end": v(260.5, -50.52) * mm});
            skArc(sketch, "E12.13.0.7", {"start": v(285.5, -50.52) * mm, "mid": v(287.26, -49.78) * mm, "end": v(288, -48.02) * mm});
            skArc(sketch, "E12.13.0.8", {"start": v(260.5, -45.52) * mm, "mid": v(258.73, -46.25) * mm, "end": v(258, -48.02) * mm});
            skArc(sketch, "E12.13.0.9", {"start": v(288, -48.02) * mm, "mid": v(287.26, -46.25) * mm, "end": v(285.5, -45.52) * mm});
            skLineSegment(sketch, "E12.13.1.0", {"start": v(260.5, -30.52) * mm, "end": v(285.5, -30.52) * mm});
            skPoint(sketch, "E12.13.1.1", {"position": v(258, -30.52) * mm});
            skPoint(sketch, "E12.13.1.2", {"position": v(258, -25.52) * mm});
            skLineSegment(sketch, "E12.13.1.3", {"start": v(260.5, -25.52) * mm, "end": v(285.5, -25.52) * mm});
            skPoint(sketch, "E12.13.1.4", {"position": v(288, -25.52) * mm});
            skPoint(sketch, "E12.13.1.5", {"position": v(288, -30.52) * mm});
            skArc(sketch, "E12.13.1.6", {"start": v(258, -28.02) * mm, "mid": v(258.73, -29.78) * mm, "end": v(260.5, -30.52) * mm});
            skArc(sketch, "E12.13.1.7", {"start": v(285.5, -30.52) * mm, "mid": v(287.26, -29.78) * mm, "end": v(288, -28.02) * mm});
            skArc(sketch, "E12.13.1.8", {"start": v(260.5, -25.52) * mm, "mid": v(258.73, -26.25) * mm, "end": v(258, -28.02) * mm});
            skArc(sketch, "E12.13.1.9", {"start": v(288, -28.02) * mm, "mid": v(287.26, -26.25) * mm, "end": v(285.5, -25.52) * mm});
            skLineSegment(sketch, "E12.13.2.0", {"start": v(260.5, -10.52) * mm, "end": v(285.5, -10.52) * mm});
            skPoint(sketch, "E12.13.2.1", {"position": v(258, -10.52) * mm});
            skPoint(sketch, "E12.13.2.2", {"position": v(258, -5.52) * mm});
            skLineSegment(sketch, "E12.13.2.3", {"start": v(260.5, -5.52) * mm, "end": v(285.5, -5.52) * mm});
            skPoint(sketch, "E12.13.2.4", {"position": v(288, -5.52) * mm});
            skPoint(sketch, "E12.13.2.5", {"position": v(288, -10.52) * mm});
            skArc(sketch, "E12.13.2.6", {"start": v(258, -8.02) * mm, "mid": v(258.73, -9.78) * mm, "end": v(260.5, -10.52) * mm});
            skArc(sketch, "E12.13.2.7", {"start": v(285.5, -10.52) * mm, "mid": v(287.26, -9.78) * mm, "end": v(288, -8.02) * mm});
            skArc(sketch, "E12.13.2.8", {"start": v(260.5, -5.52) * mm, "mid": v(258.73, -6.25) * mm, "end": v(258, -8.02) * mm});
            skArc(sketch, "E12.13.2.9", {"start": v(288, -8.02) * mm, "mid": v(287.26, -6.25) * mm, "end": v(285.5, -5.52) * mm});
            skLineSegment(sketch, "E12.13.3.0", {"start": v(260.5, 9.48) * mm, "end": v(285.5, 9.48) * mm});
            skPoint(sketch, "E12.13.3.1", {"position": v(258, 9.48) * mm});
            skPoint(sketch, "E12.13.3.2", {"position": v(258, 14.48) * mm});
            skLineSegment(sketch, "E12.13.3.3", {"start": v(260.5, 14.48) * mm, "end": v(285.5, 14.48) * mm});
            skPoint(sketch, "E12.13.3.4", {"position": v(288, 14.48) * mm});
            skPoint(sketch, "E12.13.3.5", {"position": v(288, 9.48) * mm});
            skArc(sketch, "E12.13.3.6", {"start": v(258, 11.98) * mm, "mid": v(258.73, 10.22) * mm, "end": v(260.5, 9.48) * mm});
            skArc(sketch, "E12.13.3.7", {"start": v(285.5, 9.48) * mm, "mid": v(287.26, 10.22) * mm, "end": v(288, 11.98) * mm});
            skArc(sketch, "E12.13.3.8", {"start": v(260.5, 14.48) * mm, "mid": v(258.73, 13.75) * mm, "end": v(258, 11.98) * mm});
            skArc(sketch, "E12.13.3.9", {"start": v(288, 11.98) * mm, "mid": v(287.26, 13.75) * mm, "end": v(285.5, 14.48) * mm});
            skLineSegment(sketch, "E12.13.4.0", {"start": v(260.5, 29.48) * mm, "end": v(285.5, 29.48) * mm});
            skPoint(sketch, "E12.13.4.1", {"position": v(258, 29.48) * mm});
            skPoint(sketch, "E12.13.4.2", {"position": v(258, 34.48) * mm});
            skLineSegment(sketch, "E12.13.4.3", {"start": v(260.5, 34.48) * mm, "end": v(285.5, 34.48) * mm});
            skPoint(sketch, "E12.13.4.4", {"position": v(288, 34.48) * mm});
            skPoint(sketch, "E12.13.4.5", {"position": v(288, 29.48) * mm});
            skArc(sketch, "E12.13.4.6", {"start": v(258, 31.98) * mm, "mid": v(258.73, 30.22) * mm, "end": v(260.5, 29.48) * mm});
            skArc(sketch, "E12.13.4.7", {"start": v(285.5, 29.48) * mm, "mid": v(287.26, 30.22) * mm, "end": v(288, 31.98) * mm});
            skArc(sketch, "E12.13.4.8", {"start": v(260.5, 34.48) * mm, "mid": v(258.73, 33.75) * mm, "end": v(258, 31.98) * mm});
            skArc(sketch, "E12.13.4.9", {"start": v(288, 31.98) * mm, "mid": v(287.26, 33.75) * mm, "end": v(285.5, 34.48) * mm});
            skLineSegment(sketch, "E12.13.5.0", {"start": v(260.5, 49.48) * mm, "end": v(285.5, 49.48) * mm});
            skPoint(sketch, "E12.13.5.1", {"position": v(258, 49.48) * mm});
            skPoint(sketch, "E12.13.5.2", {"position": v(258, 54.48) * mm});
            skLineSegment(sketch, "E12.13.5.3", {"start": v(260.5, 54.48) * mm, "end": v(285.5, 54.48) * mm});
            skPoint(sketch, "E12.13.5.4", {"position": v(288, 54.48) * mm});
            skPoint(sketch, "E12.13.5.5", {"position": v(288, 49.48) * mm});
            skArc(sketch, "E12.13.5.6", {"start": v(258, 51.98) * mm, "mid": v(258.73, 50.22) * mm, "end": v(260.5, 49.48) * mm});
            skArc(sketch, "E12.13.5.7", {"start": v(285.5, 49.48) * mm, "mid": v(287.26, 50.22) * mm, "end": v(288, 51.98) * mm});
            skArc(sketch, "E12.13.5.8", {"start": v(260.5, 54.48) * mm, "mid": v(258.73, 53.75) * mm, "end": v(258, 51.98) * mm});
            skArc(sketch, "E12.13.5.9", {"start": v(288, 51.98) * mm, "mid": v(287.26, 53.75) * mm, "end": v(285.5, 54.48) * mm});
            skLineSegment(sketch, "E12.direction1", {"start": v(-197, -50.52) * mm, "end": v(-162, -50.52) * mm, "construction": true});
            skLineSegment(sketch, "E12.direction2", {"start": v(-197, -50.52) * mm, "end": v(-197, -30.52) * mm, "construction": true});
            skSolve(sketch);
        }
        {
            var Q0;
            Q0=makeQuery(id+"F4.imprint","IMPRINT",FACE,{"disambiguationData":[TD([[makeQuery(id+"F4.imprint","IMPRINT",EDGE,{"derivedFrom":sQuery(id+"F4.wireOp",EDGE,"E12.7.5.0")}),1.0]])]});
            var Q1;
            Q1=makeQuery(id+"F4.imprint","IMPRINT",FACE,{"disambiguationData":[TD([[makeQuery(id+"F4.imprint","IMPRINT",EDGE,{"derivedFrom":sQuery(id+"F4.wireOp",EDGE,"E12.4.5.0")}),1.0]])]});
            var Q2;
            Q2=makeQuery(id+"F4.imprint","IMPRINT",FACE,{"disambiguationData":[TD([[makeQuery(id+"F4.imprint","IMPRINT",EDGE,{"derivedFrom":sQuery(id+"F4.wireOp",EDGE,"E12.12.5.0")}),1.0]])]});
            var Q3;
            Q3=makeQuery(id+"F4.imprint","IMPRINT",FACE,{"disambiguationData":[TD([[makeQuery(id+"F4.imprint","IMPRINT",EDGE,{"derivedFrom":sQuery(id+"F4.wireOp",EDGE,"E12.2.5.0")}),1.0]])]});
            var Q4;
            Q4=makeQuery(id+"F4.imprint","IMPRINT",FACE,{"disambiguationData":[TD([[makeQuery(id+"F4.imprint","IMPRINT",EDGE,{"derivedFrom":sQuery(id+"F4.wireOp",EDGE,"E12.10.5.0")}),1.0]])]});
            var Q5;
            Q5=makeQuery(id+"F4.imprint","IMPRINT",FACE,{"disambiguationData":[TD([[makeQuery(id+"F4.imprint","IMPRINT",EDGE,{"derivedFrom":sQuery(id+"F4.wireOp",EDGE,"E12.5.5.0")}),1.0]])]});
            var Q6;
            Q6=makeQuery(id+"F4.imprint","IMPRINT",FACE,{"disambiguationData":[TD([[makeQuery(id+"F4.imprint","IMPRINT",EDGE,{"derivedFrom":sQuery(id+"F4.wireOp",EDGE,"E12.13.5.0")}),1.0]])]});
            var Q7;
            Q7=makeQuery(id+"F4.imprint","IMPRINT",FACE,{"disambiguationData":[TD([[makeQuery(id+"F4.imprint","IMPRINT",EDGE,{"derivedFrom":sQuery(id+"F4.wireOp",EDGE,"E12.8.5.0")}),1.0]])]});
            var Q8;
            Q8=makeQuery(id+"F4.imprint","IMPRINT",FACE,{"disambiguationData":[TD([[makeQuery(id+"F4.imprint","IMPRINT",EDGE,{"derivedFrom":sQuery(id+"F4.wireOp",EDGE,"E12.11.5.0")}),1.0]])]});
            var Q9;
            Q9=makeQuery(id+"F4.imprint","IMPRINT",FACE,{"disambiguationData":[TD([[makeQuery(id+"F4.imprint","IMPRINT",EDGE,{"derivedFrom":sQuery(id+"F4.wireOp",EDGE,"E12.3.5.0")}),1.0]])]});
            var Q10;
            Q10=makeQuery(id+"F4.imprint","IMPRINT",FACE,{"disambiguationData":[TD([[makeQuery(id+"F4.imprint","IMPRINT",EDGE,{"derivedFrom":sQuery(id+"F4.wireOp",EDGE,"E12.6.5.0")}),1.0]])]});
            var Q11;
            Q11=makeQuery(id+"F4.imprint","IMPRINT",FACE,{"disambiguationData":[TD([[makeQuery(id+"F4.imprint","IMPRINT",EDGE,{"derivedFrom":sQuery(id+"F4.wireOp",EDGE,"E12.9.5.0")}),1.0]])]});
            var Q12;
            Q12=makeQuery(id+"F4.imprint","IMPRINT",FACE,{"disambiguationData":[TD([[makeQuery(id+"F4.imprint","IMPRINT",EDGE,{"derivedFrom":sQuery(id+"F4.wireOp",EDGE,"E12.0.5.0")}),1.0]])]});
            var Q13;
            Q13=makeQuery(id+"F4.imprint","IMPRINT",FACE,{"disambiguationData":[TD([[makeQuery(id+"F4.imprint","IMPRINT",EDGE,{"derivedFrom":sQuery(id+"F4.wireOp",EDGE,"E12.1.5.0")}),1.0]])]});
            var Q14;
            Q14=makeQuery(id+"F4.imprint","IMPRINT",FACE,{"disambiguationData":[TD([[makeQuery(id+"F4.imprint","IMPRINT",EDGE,{"derivedFrom":sQuery(id+"F4.wireOp",EDGE,"E12.7.4.0")}),1.0]])]});
            var Q15;
            Q15=makeQuery(id+"F4.imprint","IMPRINT",FACE,{"disambiguationData":[TD([[makeQuery(id+"F4.imprint","IMPRINT",EDGE,{"derivedFrom":sQuery(id+"F4.wireOp",EDGE,"E12.2.4.0")}),1.0]])]});
            var Q16;
            Q16=makeQuery(id+"F4.imprint","IMPRINT",FACE,{"disambiguationData":[TD([[makeQuery(id+"F4.imprint","IMPRINT",EDGE,{"derivedFrom":sQuery(id+"F4.wireOp",EDGE,"E12.10.4.0")}),1.0]])]});
            var Q17;
            Q17=makeQuery(id+"F4.imprint","IMPRINT",FACE,{"disambiguationData":[TD([[makeQuery(id+"F4.imprint","IMPRINT",EDGE,{"derivedFrom":sQuery(id+"F4.wireOp",EDGE,"E12.5.4.0")}),1.0]])]});
            var Q18;
            Q18=makeQuery(id+"F4.imprint","IMPRINT",FACE,{"disambiguationData":[TD([[makeQuery(id+"F4.imprint","IMPRINT",EDGE,{"derivedFrom":sQuery(id+"F4.wireOp",EDGE,"E12.13.4.0")}),1.0]])]});
            var Q19;
            Q19=makeQuery(id+"F4.imprint","IMPRINT",FACE,{"disambiguationData":[TD([[makeQuery(id+"F4.imprint","IMPRINT",EDGE,{"derivedFrom":sQuery(id+"F4.wireOp",EDGE,"E12.8.4.0")}),1.0]])]});
            var Q20;
            Q20=makeQuery(id+"F4.imprint","IMPRINT",FACE,{"disambiguationData":[TD([[makeQuery(id+"F4.imprint","IMPRINT",EDGE,{"derivedFrom":sQuery(id+"F4.wireOp",EDGE,"E12.11.4.0")}),1.0]])]});
            var Q21;
            Q21=makeQuery(id+"F4.imprint","IMPRINT",FACE,{"disambiguationData":[TD([[makeQuery(id+"F4.imprint","IMPRINT",EDGE,{"derivedFrom":sQuery(id+"F4.wireOp",EDGE,"E12.3.4.0")}),1.0]])]});
            var Q22;
            Q22=makeQuery(id+"F4.imprint","IMPRINT",FACE,{"disambiguationData":[TD([[makeQuery(id+"F4.imprint","IMPRINT",EDGE,{"derivedFrom":sQuery(id+"F4.wireOp",EDGE,"E12.6.4.0")}),1.0]])]});
            var Q23;
            Q23=makeQuery(id+"F4.imprint","IMPRINT",FACE,{"disambiguationData":[TD([[makeQuery(id+"F4.imprint","IMPRINT",EDGE,{"derivedFrom":sQuery(id+"F4.wireOp",EDGE,"E12.9.4.0")}),1.0]])]});
            var Q24;
            Q24=makeQuery(id+"F4.imprint","IMPRINT",FACE,{"disambiguationData":[TD([[makeQuery(id+"F4.imprint","IMPRINT",EDGE,{"derivedFrom":sQuery(id+"F4.wireOp",EDGE,"E12.12.4.0")}),1.0]])]});
            var Q25;
            Q25=makeQuery(id+"F4.imprint","IMPRINT",FACE,{"disambiguationData":[TD([[makeQuery(id+"F4.imprint","IMPRINT",EDGE,{"derivedFrom":sQuery(id+"F4.wireOp",EDGE,"E12.4.4.0")}),1.0]])]});
            var Q26;
            Q26=makeQuery(id+"F4.imprint","IMPRINT",FACE,{"disambiguationData":[TD([[makeQuery(id+"F4.imprint","IMPRINT",EDGE,{"derivedFrom":sQuery(id+"F4.wireOp",EDGE,"E12.0.4.0")}),1.0]])]});
            var Q27;
            Q27=makeQuery(id+"F4.imprint","IMPRINT",FACE,{"disambiguationData":[TD([[makeQuery(id+"F4.imprint","IMPRINT",EDGE,{"derivedFrom":sQuery(id+"F4.wireOp",EDGE,"E12.1.4.0")}),1.0]])]});
            var Q28;
            Q28=makeQuery(id+"F4.imprint","IMPRINT",FACE,{"disambiguationData":[TD([[makeQuery(id+"F4.imprint","IMPRINT",EDGE,{"derivedFrom":sQuery(id+"F4.wireOp",EDGE,"E12.10.3.0")}),1.0]])]});
            var Q29;
            Q29=makeQuery(id+"F4.imprint","IMPRINT",FACE,{"disambiguationData":[TD([[makeQuery(id+"F4.imprint","IMPRINT",EDGE,{"derivedFrom":sQuery(id+"F4.wireOp",EDGE,"E12.7.3.0")}),1.0]])]});
            var Q30;
            Q30=makeQuery(id+"F4.imprint","IMPRINT",FACE,{"disambiguationData":[TD([[makeQuery(id+"F4.imprint","IMPRINT",EDGE,{"derivedFrom":sQuery(id+"F4.wireOp",EDGE,"E12.5.3.0")}),1.0]])]});
            var Q31;
            Q31=makeQuery(id+"F4.imprint","IMPRINT",FACE,{"disambiguationData":[TD([[makeQuery(id+"F4.imprint","IMPRINT",EDGE,{"derivedFrom":sQuery(id+"F4.wireOp",EDGE,"E12.13.3.0")}),1.0]])]});
            var Q32;
            Q32=makeQuery(id+"F4.imprint","IMPRINT",FACE,{"disambiguationData":[TD([[makeQuery(id+"F4.imprint","IMPRINT",EDGE,{"derivedFrom":sQuery(id+"F4.wireOp",EDGE,"E12.8.3.0")}),1.0]])]});
            var Q33;
            Q33=makeQuery(id+"F4.imprint","IMPRINT",FACE,{"disambiguationData":[TD([[makeQuery(id+"F4.imprint","IMPRINT",EDGE,{"derivedFrom":sQuery(id+"F4.wireOp",EDGE,"E12.3.3.0")}),1.0]])]});
            var Q34;
            Q34=makeQuery(id+"F4.imprint","IMPRINT",FACE,{"disambiguationData":[TD([[makeQuery(id+"F4.imprint","IMPRINT",EDGE,{"derivedFrom":sQuery(id+"F4.wireOp",EDGE,"E12.11.3.0")}),1.0]])]});
            var Q35;
            Q35=makeQuery(id+"F4.imprint","IMPRINT",FACE,{"disambiguationData":[TD([[makeQuery(id+"F4.imprint","IMPRINT",EDGE,{"derivedFrom":sQuery(id+"F4.wireOp",EDGE,"E12.6.3.0")}),1.0]])]});
            var Q36;
            Q36=makeQuery(id+"F4.imprint","IMPRINT",FACE,{"disambiguationData":[TD([[makeQuery(id+"F4.imprint","IMPRINT",EDGE,{"derivedFrom":sQuery(id+"F4.wireOp",EDGE,"E12.9.3.0")}),1.0]])]});
            var Q37;
            Q37=makeQuery(id+"F4.imprint","IMPRINT",FACE,{"disambiguationData":[TD([[makeQuery(id+"F4.imprint","IMPRINT",EDGE,{"derivedFrom":sQuery(id+"F4.wireOp",EDGE,"E12.12.3.0")}),1.0]])]});
            var Q38;
            Q38=makeQuery(id+"F4.imprint","IMPRINT",FACE,{"disambiguationData":[TD([[makeQuery(id+"F4.imprint","IMPRINT",EDGE,{"derivedFrom":sQuery(id+"F4.wireOp",EDGE,"E12.4.3.0")}),1.0]])]});
            var Q39;
            Q39=makeQuery(id+"F4.imprint","IMPRINT",FACE,{"disambiguationData":[TD([[makeQuery(id+"F4.imprint","IMPRINT",EDGE,{"derivedFrom":sQuery(id+"F4.wireOp",EDGE,"E12.2.3.0")}),1.0]])]});
            var Q40;
            Q40=makeQuery(id+"F4.imprint","IMPRINT",FACE,{"disambiguationData":[TD([[makeQuery(id+"F4.imprint","IMPRINT",EDGE,{"derivedFrom":sQuery(id+"F4.wireOp",EDGE,"E12.0.3.0")}),1.0]])]});
            var Q41;
            Q41=makeQuery(id+"F4.imprint","IMPRINT",FACE,{"disambiguationData":[TD([[makeQuery(id+"F4.imprint","IMPRINT",EDGE,{"derivedFrom":sQuery(id+"F4.wireOp",EDGE,"E12.1.3.0")}),1.0]])]});
            var Q42;
            Q42=makeQuery(id+"F4.imprint","IMPRINT",FACE,{"disambiguationData":[TD([[makeQuery(id+"F4.imprint","IMPRINT",EDGE,{"derivedFrom":sQuery(id+"F4.wireOp",EDGE,"E12.10.2.0")}),1.0]])]});
            var Q43;
            Q43=makeQuery(id+"F4.imprint","IMPRINT",FACE,{"disambiguationData":[TD([[makeQuery(id+"F4.imprint","IMPRINT",EDGE,{"derivedFrom":sQuery(id+"F4.wireOp",EDGE,"E12.5.2.0")}),1.0]])]});
            var Q44;
            Q44=makeQuery(id+"F4.imprint","IMPRINT",FACE,{"disambiguationData":[TD([[makeQuery(id+"F4.imprint","IMPRINT",EDGE,{"derivedFrom":sQuery(id+"F4.wireOp",EDGE,"E12.13.2.0")}),1.0]])]});
            var Q45;
            Q45=makeQuery(id+"F4.imprint","IMPRINT",FACE,{"disambiguationData":[TD([[makeQuery(id+"F4.imprint","IMPRINT",EDGE,{"derivedFrom":sQuery(id+"F4.wireOp",EDGE,"E12.8.2.0")}),1.0]])]});
            var Q46;
            Q46=makeQuery(id+"F4.imprint","IMPRINT",FACE,{"disambiguationData":[TD([[makeQuery(id+"F4.imprint","IMPRINT",EDGE,{"derivedFrom":sQuery(id+"F4.wireOp",EDGE,"E12.3.2.0")}),1.0]])]});
            var Q47;
            Q47=makeQuery(id+"F4.imprint","IMPRINT",FACE,{"disambiguationData":[TD([[makeQuery(id+"F4.imprint","IMPRINT",EDGE,{"derivedFrom":sQuery(id+"F4.wireOp",EDGE,"E12.11.2.0")}),1.0]])]});
            var Q48;
            Q48=makeQuery(id+"F4.imprint","IMPRINT",FACE,{"disambiguationData":[TD([[makeQuery(id+"F4.imprint","IMPRINT",EDGE,{"derivedFrom":sQuery(id+"F4.wireOp",EDGE,"E12.6.2.0")}),1.0]])]});
            var Q49;
            Q49=makeQuery(id+"F4.imprint","IMPRINT",FACE,{"disambiguationData":[TD([[makeQuery(id+"F4.imprint","IMPRINT",EDGE,{"derivedFrom":sQuery(id+"F4.wireOp",EDGE,"E12.9.2.0")}),1.0]])]});
            var Q50;
            Q50=makeQuery(id+"F4.imprint","IMPRINT",FACE,{"disambiguationData":[TD([[makeQuery(id+"F4.imprint","IMPRINT",EDGE,{"derivedFrom":sQuery(id+"F4.wireOp",EDGE,"E12.12.2.0")}),1.0]])]});
            var Q51;
            Q51=makeQuery(id+"F4.imprint","IMPRINT",FACE,{"disambiguationData":[TD([[makeQuery(id+"F4.imprint","IMPRINT",EDGE,{"derivedFrom":sQuery(id+"F4.wireOp",EDGE,"E12.4.2.0")}),1.0]])]});
            var Q52;
            Q52=makeQuery(id+"F4.imprint","IMPRINT",FACE,{"disambiguationData":[TD([[makeQuery(id+"F4.imprint","IMPRINT",EDGE,{"derivedFrom":sQuery(id+"F4.wireOp",EDGE,"E12.7.2.0")}),1.0]])]});
            var Q53;
            Q53=makeQuery(id+"F4.imprint","IMPRINT",FACE,{"disambiguationData":[TD([[makeQuery(id+"F4.imprint","IMPRINT",EDGE,{"derivedFrom":sQuery(id+"F4.wireOp",EDGE,"E12.2.2.0")}),1.0]])]});
            var Q54;
            Q54=makeQuery(id+"F4.imprint","IMPRINT",FACE,{"disambiguationData":[TD([[makeQuery(id+"F4.imprint","IMPRINT",EDGE,{"derivedFrom":sQuery(id+"F4.wireOp",EDGE,"E12.0.2.0")}),1.0]])]});
            var Q55;
            Q55=makeQuery(id+"F4.imprint","IMPRINT",FACE,{"disambiguationData":[TD([[makeQuery(id+"F4.imprint","IMPRINT",EDGE,{"derivedFrom":sQuery(id+"F4.wireOp",EDGE,"E12.1.2.0")}),1.0]])]});
            var Q56;
            Q56=makeQuery(id+"F4.imprint","IMPRINT",FACE,{"disambiguationData":[TD([[makeQuery(id+"F4.imprint","IMPRINT",EDGE,{"derivedFrom":sQuery(id+"F4.wireOp",EDGE,"E12.5.1.0")}),1.0]])]});
            var Q57;
            Q57=makeQuery(id+"F4.imprint","IMPRINT",FACE,{"disambiguationData":[TD([[makeQuery(id+"F4.imprint","IMPRINT",EDGE,{"derivedFrom":sQuery(id+"F4.wireOp",EDGE,"E12.13.1.0")}),1.0]])]});
            var Q58;
            Q58=makeQuery(id+"F4.imprint","IMPRINT",FACE,{"disambiguationData":[TD([[makeQuery(id+"F4.imprint","IMPRINT",EDGE,{"derivedFrom":sQuery(id+"F4.wireOp",EDGE,"E12.10.1.0")}),1.0]])]});
            var Q59;
            Q59=makeQuery(id+"F4.imprint","IMPRINT",FACE,{"disambiguationData":[TD([[makeQuery(id+"F4.imprint","IMPRINT",EDGE,{"derivedFrom":sQuery(id+"F4.wireOp",EDGE,"E12.8.1.0")}),1.0]])]});
            var Q60;
            Q60=makeQuery(id+"F4.imprint","IMPRINT",FACE,{"disambiguationData":[TD([[makeQuery(id+"F4.imprint","IMPRINT",EDGE,{"derivedFrom":sQuery(id+"F4.wireOp",EDGE,"E12.3.1.0")}),1.0]])]});
            var Q61;
            Q61=makeQuery(id+"F4.imprint","IMPRINT",FACE,{"disambiguationData":[TD([[makeQuery(id+"F4.imprint","IMPRINT",EDGE,{"derivedFrom":sQuery(id+"F4.wireOp",EDGE,"E12.11.1.0")}),1.0]])]});
            var Q62;
            Q62=makeQuery(id+"F4.imprint","IMPRINT",FACE,{"disambiguationData":[TD([[makeQuery(id+"F4.imprint","IMPRINT",EDGE,{"derivedFrom":sQuery(id+"F4.wireOp",EDGE,"E12.6.1.0")}),1.0]])]});
            var Q63;
            Q63=makeQuery(id+"F4.imprint","IMPRINT",FACE,{"disambiguationData":[TD([[makeQuery(id+"F4.imprint","IMPRINT",EDGE,{"derivedFrom":sQuery(id+"F4.wireOp",EDGE,"E12.9.1.0")}),1.0]])]});
            var Q64;
            Q64=makeQuery(id+"F4.imprint","IMPRINT",FACE,{"disambiguationData":[TD([[makeQuery(id+"F4.imprint","IMPRINT",EDGE,{"derivedFrom":sQuery(id+"F4.wireOp",EDGE,"E12.12.1.0")}),1.0]])]});
            var Q65;
            Q65=makeQuery(id+"F4.imprint","IMPRINT",FACE,{"disambiguationData":[TD([[makeQuery(id+"F4.imprint","IMPRINT",EDGE,{"derivedFrom":sQuery(id+"F4.wireOp",EDGE,"E12.4.1.0")}),1.0]])]});
            var Q66;
            Q66=makeQuery(id+"F4.imprint","IMPRINT",FACE,{"disambiguationData":[TD([[makeQuery(id+"F4.imprint","IMPRINT",EDGE,{"derivedFrom":sQuery(id+"F4.wireOp",EDGE,"E12.7.1.0")}),1.0]])]});
            var Q67;
            Q67=makeQuery(id+"F4.imprint","IMPRINT",FACE,{"disambiguationData":[TD([[makeQuery(id+"F4.imprint","IMPRINT",EDGE,{"derivedFrom":sQuery(id+"F4.wireOp",EDGE,"E12.2.1.0")}),1.0]])]});
            var Q68;
            Q68=makeQuery(id+"F4.imprint","IMPRINT",FACE,{"disambiguationData":[TD([[makeQuery(id+"F4.imprint","IMPRINT",EDGE,{"derivedFrom":sQuery(id+"F4.wireOp",EDGE,"E12.0.1.0")}),1.0]])]});
            var Q69;
            Q69=makeQuery(id+"F4.imprint","IMPRINT",FACE,{"disambiguationData":[TD([[makeQuery(id+"F4.imprint","IMPRINT",EDGE,{"derivedFrom":sQuery(id+"F4.wireOp",EDGE,"E12.1.1.0")}),1.0]])]});
            var Q70;
            Q70=makeQuery(id+"F4.imprint","IMPRINT",FACE,{"disambiguationData":[TD([[makeQuery(id+"F4.imprint","IMPRINT",EDGE,{"derivedFrom":sQuery(id+"F4.wireOp",EDGE,"E12.5.0.0")}),1.0]])]});
            var Q71;
            Q71=makeQuery(id+"F4.imprint","IMPRINT",FACE,{"disambiguationData":[TD([[makeQuery(id+"F4.imprint","IMPRINT",EDGE,{"derivedFrom":sQuery(id+"F4.wireOp",EDGE,"E12.13.0.0")}),1.0]])]});
            var Q72;
            Q72=makeQuery(id+"F4.imprint","IMPRINT",FACE,{"disambiguationData":[TD([[makeQuery(id+"F4.imprint","IMPRINT",EDGE,{"derivedFrom":sQuery(id+"F4.wireOp",EDGE,"E12.8.0.0")}),1.0]])]});
            var Q73;
            Q73=makeQuery(id+"F4.imprint","IMPRINT",FACE,{"disambiguationData":[TD([[makeQuery(id+"F4.imprint","IMPRINT",EDGE,{"derivedFrom":sQuery(id+"F4.wireOp",EDGE,"E12.3.0.0")}),1.0]])]});
            var Q74;
            Q74=makeQuery(id+"F4.imprint","IMPRINT",FACE,{"disambiguationData":[TD([[makeQuery(id+"F4.imprint","IMPRINT",EDGE,{"derivedFrom":sQuery(id+"F4.wireOp",EDGE,"E12.11.0.0")}),1.0]])]});
            var Q75;
            Q75=makeQuery(id+"F4.imprint","IMPRINT",FACE,{"disambiguationData":[TD([[makeQuery(id+"F4.imprint","IMPRINT",EDGE,{"derivedFrom":sQuery(id+"F4.wireOp",EDGE,"E12.6.0.0")}),1.0]])]});
            var Q76;
            Q76=makeQuery(id+"F4.imprint","IMPRINT",FACE,{"disambiguationData":[TD([[makeQuery(id+"F4.imprint","IMPRINT",EDGE,{"derivedFrom":sQuery(id+"F4.wireOp",EDGE,"E12.9.0.0")}),1.0]])]});
            var Q77;
            Q77=makeQuery(id+"F4.imprint","IMPRINT",FACE,{"disambiguationData":[TD([[makeQuery(id+"F4.imprint","IMPRINT",EDGE,{"derivedFrom":sQuery(id+"F4.wireOp",EDGE,"E12.12.0.0")}),1.0]])]});
            var Q78;
            Q78=makeQuery(id+"F4.imprint","IMPRINT",FACE,{"disambiguationData":[TD([[makeQuery(id+"F4.imprint","IMPRINT",EDGE,{"derivedFrom":sQuery(id+"F4.wireOp",EDGE,"E12.4.0.0")}),1.0]])]});
            var Q79;
            Q79=makeQuery(id+"F4.imprint","IMPRINT",FACE,{"disambiguationData":[TD([[makeQuery(id+"F4.imprint","IMPRINT",EDGE,{"derivedFrom":sQuery(id+"F4.wireOp",EDGE,"E12.7.0.0")}),1.0]])]});
            var Q80;
            Q80=makeQuery(id+"F4.imprint","IMPRINT",FACE,{"disambiguationData":[TD([[makeQuery(id+"F4.imprint","IMPRINT",EDGE,{"derivedFrom":sQuery(id+"F4.wireOp",EDGE,"E12.10.0.0")}),1.0]])]});
            var Q81;
            Q81=makeQuery(id+"F4.imprint","IMPRINT",FACE,{"disambiguationData":[TD([[makeQuery(id+"F4.imprint","IMPRINT",EDGE,{"derivedFrom":sQuery(id+"F4.wireOp",EDGE,"E7.bottom")}),-1.0]])]});
            var Q82;
            Q82=makeQuery(id+"F4.imprint","IMPRINT",FACE,{"disambiguationData":[TD([[makeQuery(id+"F4.imprint","IMPRINT",EDGE,{"derivedFrom":sQuery(id+"F4.wireOp",EDGE,"E12.1.0.0")}),1.0]])]});
            var Q83;
            Q83=makeQuery(id+"F4.imprint","IMPRINT",FACE,{"disambiguationData":[TD([[makeQuery(id+"F4.imprint","IMPRINT",EDGE,{"derivedFrom":sQuery(id+"F4.wireOp",EDGE,"E12.2.0.0")}),1.0]])]});
            extrude(context, id + "F5", {"entities" : qUnion([Q0, Q1, Q2, Q3, Q4, Q5, Q6, Q7, Q8, Q9, Q10, Q11, Q12, Q13, Q14, Q15, Q16, Q17, Q18, Q19, Q20, Q21, Q22, Q23, Q24, Q25, Q26, Q27, Q28, Q29, Q30, Q31, Q32, Q33, Q34, Q35, Q36, Q37, Q38, Q39, Q40, Q41, Q42, Q43, Q44, Q45, Q46, Q47, Q48, Q49, Q50, Q51, Q52, Q53, Q54, Q55, Q56, Q57, Q58, Q59, Q60, Q61, Q62, Q63, Q64, Q65, Q66, Q67, Q68, Q69, Q70, Q71, Q72, Q73, Q74, Q75, Q76, Q77, Q78, Q79, Q80, Q81, Q82, Q83]), "operationType" : NewBodyOperationType.REMOVE, "oppositeDirection" : true, "depth" : 0.5 * mm, "offsetDistance" : 25 * mm});
        }
        {
            var Q0;
            Q0=makeQuery(id+"F1.opExtrude","CAP_EDGE",EDGE,{"disambiguationData":[OSD([sQuery(id+"F0.wireOp",EDGE,"E0.right")])],"isStart":false});
            var Q1;
            Q1=makeQuery(id+"F1.opExtrude","CAP_EDGE",EDGE,{"disambiguationData":[OSD([sQuery(id+"F0.wireOp",EDGE,"E0.top")])],"isStart":false});
            var Q2;
            Q2=makeQuery(id+"F1.opExtrude","CAP_EDGE",EDGE,{"disambiguationData":[OSD([sQuery(id+"F0.wireOp",EDGE,"E0.bottom")])],"isStart":false});
            var Q3;
            Q3=makeQuery(id+"F1.opExtrude","CAP_EDGE",EDGE,{"disambiguationData":[OSD([sQuery(id+"F0.wireOp",EDGE,"E0.left")])],"isStart":false});
            fillet(context, id + "F6", {"entities" : qUnion([Q0, Q1, Q2, Q3]), "radius" : 5 * mm, "tangentPropagation" : true, "allowEdgeOverflow" : false});
        }
    });
